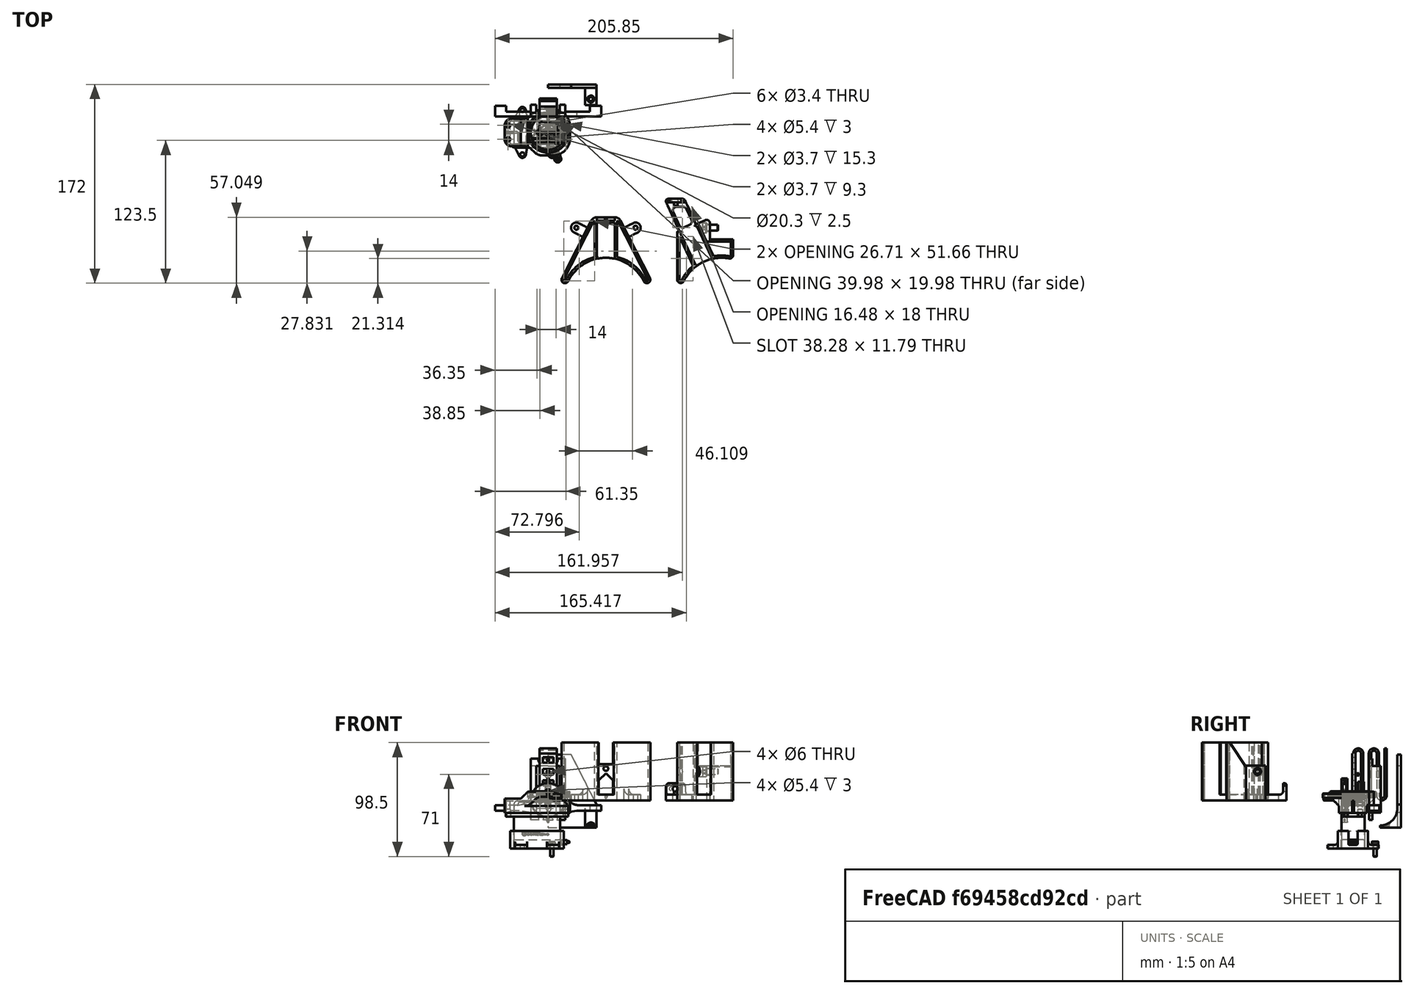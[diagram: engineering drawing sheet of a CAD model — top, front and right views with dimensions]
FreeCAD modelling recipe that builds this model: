
FCSTD DOCUMENT  (FreeCAD 1.0R39109 (Git))
Label: OuterCanMover
License: All rights reserved
LicenseURL: https://en.wikipedia.org/wiki/All_rights_reserved
objects: Sketcher::SketchObject×79, PartDesign::Pocket×47, PartDesign::Pad×34, PartDesign::Body×20, App::Part×11, App::Link×9, PartDesign::Mirrored×9, App::LinkElement×8, PartDesign::Fillet×7, PartDesign::PolarPattern×7, Part::Feature×6, PartDesign::Groove×5, PartDesign::LinearPattern×4, Part::FeaturePython×4, Mesh::Feature×3, PartDesign::Chamfer×3, PartDesign::Revolution×2, PartDesign::SubShapeBinder×1, PartDesign::MultiTransform×1
note: 525 computed .brp shape members not serialized (recipe doc carries the construction recipe); baked Part::Feature solids carry a one-line shape summary decoded from their .brp

FEATURE [Sketcher::SketchObject] Sketch
  ArcFitTolerance = 1e-06
  AttachmentSupport = -> [XY_Plane]
  FullyConstrained = true
  MakeInternals = false
  MapMode = 5
  sketch-geometry (18):
    g0: Circle [constr] CenterX=0 CenterY=-62.5 CenterZ=0 NormalX=0 NormalY=0 NormalZ=1 AngleXU=0 Radius=36.25
    g1: LineSegment [constr] StartX=-10 StartY=10 StartZ=0 EndX=-10 EndY=-10 EndZ=0
    g2: LineSegment [constr] StartX=-10 StartY=-10 StartZ=0 EndX=10 EndY=-10 EndZ=0
    g3: LineSegment [constr] StartX=10 StartY=-10 StartZ=0 EndX=10 EndY=10 EndZ=0
    g4: LineSegment [constr] StartX=10 StartY=10 StartZ=0 EndX=-10 EndY=10 EndZ=0
    g5: ArcOfCircle CenterX=0 CenterY=-62.5 CenterZ=0 NormalX=0 NormalY=0 NormalZ=1 AngleXU=0 Radius=36.5 StartAngle=1.39264 EndAngle=2.6779
    g6: LineSegment StartX=10 StartY=-10 StartZ=0 EndX=-10 EndY=-10 EndZ=0
    g7: LineSegment StartX=-10 StartY=-10 StartZ=0 EndX=-10 EndY=10 EndZ=0
    g8: LineSegment StartX=-14 StartY=14 StartZ=0 EndX=-23.3291 EndY=14 EndZ=0
    g9: LineSegment StartX=-38.3291 StartY=-1 StartZ=0 EndX=-38.3291 EndY=-44.8335 EndZ=0
    g10: ArcOfCircle CenterX=-14 CenterY=10 CenterZ=0 NormalX=0 NormalY=0 NormalZ=1 AngleXU=0 Radius=4 StartAngle=0 EndAngle=1.5708
    g11: GeomPoint [constr] X=-10 Y=14 Z=0
    g12: LineSegment StartX=10 StartY=-10 StartZ=0 EndX=10 EndY=-23.6252 EndZ=0
    g13: ArcOfCircle CenterX=-35.3291 CenterY=-44.8335 CenterZ=0 NormalX=0 NormalY=0 NormalZ=1 AngleXU=0 Radius=3 StartAngle=3.14159 EndAngle=5.81949
    g14: ArcOfCircle CenterX=7 CenterY=-23.6252 CenterZ=0 NormalX=0 NormalY=0 NormalZ=1 AngleXU=0 Radius=3 StartAngle=4.53423 EndAngle=6.28319
    g15: LineSegment [constr] StartX=-38.3291 StartY=14 StartZ=0 EndX=-16.3503 EndY=-29.8669 EndZ=0
    g16: ArcOfCircle CenterX=-23.3291 CenterY=-1 CenterZ=0 NormalX=0 NormalY=0 NormalZ=1 AngleXU=0 Radius=15 StartAngle=1.5708 EndAngle=3.14159
    g17: GeomPoint [constr] X=-38.3291 Y=14 Z=0
  constraints (44):
    c: Coincident(g1,g2)
    c: Coincident(g2,g3)
    c: Coincident(g3,g4)
    c: Vertical(g1)
    c: Vertical(g3)
    c: Horizontal(g2)
    c: Horizontal(g4)
    c: Symmetric(g1,g2,g-1)
    c: Equal(g4,g3)
    c: Coincident(g5,g0)
    c: DistanceY(g3,g3) = 20
    c: Diameter(g0) = 72.5
    c: Coincident(g7,g6)
    c: Vertical(g7)
    c: Horizontal(g8)
    c: Vertical(g9)
    c: Coincident(g1,g4)
    c: Distance(g11,g1) = 4
    c: PointOnObject(g11,g7)
    c: PointOnObject(g11,g8)
    c: Tangent(g7,g10) = -1.5708
    c: Tangent(g8,g10) = -1.5708
    c: Radius(g10) = 4
    c: PointOnObject(g0,g-2)
    c: DistanceY(g0,g-1) = 62.5
    c: Coincident(g12,g6)
    c: Vertical(g12)
    c: Coincident(g1,g6)
    c: Tangent(g9,g13) = -1.5708
    c: Tangent(g5,g13) = 1.5708
    c: Tangent(g5,g14) = 1.5708
    c: Tangent(g12,g14) = 1.5708
    c: Equal(g14,g13)
    c: Radius(g13) = 3
    c: Coincident(g15,g17)
    c: PointOnObject(g15,g5)
    c: Symmetric(g14,g13,g15)
    c: Coincident(g6,g2)
    c: PointOnObject(g17,g8)
    c: PointOnObject(g17,g9)
    c: Tangent(g8,g16) = -1.5708
    c: Tangent(g9,g16) = -1.5708
    c: Radius(g16) = 15
    c: Diameter(g5) = 73
FEATURE [PartDesign::Pad] Pad
  Direction = (0,0,1)
  Length = 50
  Length2 = 10
  Profile = -> Sketch
  ReferenceAxis = -> Sketch [N_Axis]
  Suppressed = false
  Type = 0
FEATURE [Sketcher::SketchObject] Sketch001
  ArcFitTolerance = 1e-06
  AttachmentOffset = pos=(0,0,5) rot=(0,0,1;0rad)
  AttachmentSupport = -> [XY_Plane]
  ExternalGeometry = -> [Pad]
  FullyConstrained = true
  MakeInternals = false
  MapMode = 5
  Placement = pos=(0,0,5) rot=(0,0,1;0rad)
  sketch-geometry (25):
    g0: LineSegment [constr] StartX=-44.1685 StartY=14 StartZ=0 EndX=-35.9616 EndY=-3.59975 EndZ=0
    g1: LineSegment StartX=-8.60751 StartY=-25.8214 StartZ=0 EndX=-21.3706 EndY=1.54911 EndZ=0
    g2: LineSegment StartX=-44.1685 StartY=14 StartZ=0 EndX=-27.1765 EndY=14 EndZ=0
    g3: ArcOfCircle CenterX=0 CenterY=-62.5 CenterZ=0 NormalX=0 NormalY=0 NormalZ=1 AngleXU=0 Radius=36.5 StartAngle=1.82252 EndAngle=2.19174
    g4: LineSegment [constr] StartX=0 StartY=-62.5 StartZ=0 EndX=-35.6725 EndY=14 EndZ=0
    g5: LineSegment StartX=-22.5646 StartY=-32.3297 StartZ=0 EndX=-21.6583 EndY=-31.9071 EndZ=0
    g6: LineSegment StartX=-8.60751 StartY=-25.8214 StartZ=0 EndX=-9.51381 EndY=-26.244 EndZ=0
    g7: LineSegment StartX=-21.6583 StartY=-31.9071 StartZ=0 EndX=-21.2357 EndY=-32.8134 EndZ=0
    g8: LineSegment StartX=-9.51381 StartY=-26.244 StartZ=0 EndX=-9.0912 EndY=-27.1503 EndZ=0
    g9: LineSegment [constr] StartX=-22.5646 StartY=-32.3297 StartZ=0 EndX=-8.60751 EndY=-25.8214 EndZ=0
    g10: LineSegment StartX=-35.9616 StartY=-3.59975 StartZ=0 EndX=-34.6022 EndY=-2.96583 EndZ=0
    g11: LineSegment StartX=-21.3706 StartY=1.54911 StartZ=0 EndX=-22.73 EndY=0.915178 EndZ=0
    g12: LineSegment StartX=-34.6022 StartY=-2.96583 StartZ=0 EndX=-33.9683 EndY=-4.32529 EndZ=0
    g13: LineSegment StartX=-23.364 StartY=2.27464 StartZ=0 EndX=-22.73 EndY=0.915178 EndZ=0
    g14: LineSegment StartX=-35.3277 StartY=-4.95922 StartZ=0 EndX=-22.5646 EndY=-32.3297 EndZ=0
    g15: LineSegment [constr] StartX=-22.0045 StartY=2.90857 StartZ=0 EndX=-27.1765 EndY=14 EndZ=0
    g16: LineSegment StartX=-23.364 StartY=2.27464 StartZ=0 EndX=-22.0045 EndY=2.90857 EndZ=0
    g17: LineSegment StartX=-33.9683 StartY=-4.32529 StartZ=0 EndX=-35.3277 EndY=-4.95922 EndZ=0
    g18: LineSegment [constr] StartX=-35.9616 StartY=-3.59975 StartZ=0 EndX=-35.3277 EndY=-4.95922 EndZ=0
    g19: LineSegment [constr] StartX=-22.0045 StartY=2.90857 StartZ=0 EndX=-21.3706 EndY=1.54911 EndZ=0
    g20: ArcOfCircle CenterX=-20.8978 CenterY=10 CenterZ=0 NormalX=0 NormalY=0 NormalZ=1 AngleXU=0 Radius=4 StartAngle=1.5708 EndAngle=3.57792
    g21: LineSegment StartX=-38.3291 StartY=-4.12459 StartZ=0 EndX=-44.1685 EndY=14 EndZ=0
    g22: LineSegment StartX=-24.523 StartY=8.30953 StartZ=0 EndX=-22.0045 EndY=2.90857 EndZ=0
    g23: LineSegment StartX=-27.1765 StartY=14 StartZ=0 EndX=-20.8978 EndY=14 EndZ=0
    g24: ArcOfCircle CenterX=-37.0872 CenterY=-4.12459 CenterZ=0 NormalX=0 NormalY=0 NormalZ=1 AngleXU=0 Radius=1.2419 StartAngle=0.436322 EndAngle=3.14159
  constraints (64):
    c: PointOnObject(g15,g-3)
    c: Coincident(g2,g15)
    c: Parallel(g1,g0)
    c: Coincident(g3,g-5)
    c: Angle(g-2,g1) = 0.436332
    c: Coincident(g4,g3)
    c: Parallel(g4,g1)
    c: Coincident(g2,g0)
    c: Horizontal(g2)
    c: Symmetric(g0,g15,g4)
    c: Coincident(g7,g5)
    c: Coincident(g8,g6)
    c: Coincident(g3,g8)
    c: Symmetric(g6,g5,g4)
    c: Coincident(g9,g5)
    c: Coincident(g9,g6)
    c: PointOnObject(g6,g9)
    c: PointOnObject(g5,g9)
    c: Perpendicular(g5,g7)
    c: Perpendicular(g6,g8)
    c: Coincident(g3,g7)
    c: PointOnObject(g3,g-5)
    c: Distance(g7,g7) = 1
    c: Distance(g5,g5) = 1
    c: Coincident(g14,g5)
    c: Coincident(g1,g6)
    c: Distance(g1,g14) = 15.4
    c: PointOnObject(g16,g15)
    c: Distance(g17,g10) = 1.5
    c: Symmetric(g12,g13,g4)
    c: Perpendicular(g0,g10) = 1.5708
    c: PointOnObject(g14,g11)
    c: Perpendicular(g1,g11) = 1.5708
    c: PointOnObject(g15,g16)
    c: Coincident(g11,g13)
    c: Coincident(g17,g12)
    c: Perpendicular(g10,g12) = 4.71239
    c: Perpendicular(g12,g17)
    c: Perpendicular(g15,g16)
    c: Parallel(g15,g1)
    c: Coincident(g18,g0)
    c: Coincident(g18,g17)
    c: Coincident(g19,g15)
    c: Coincident(g19,g1)
    c: Parallel(g19,g15)
    c: Coincident(g13,g16)
    c: Parallel(g18,g0)
    c: Coincident(g14,g17)
    c: Equal(g11,g17)
    c: Distance(g14,g5) = 30.2
    c: Parallel(g1,g14)
    c: Distance(g10,g10) = 1.5
    c: PointOnObject(g20,g15)
    c: PointOnObject(g20,g-3)
    c: Coincident(g21,g0)
    c: Coincident(g22,g16)
    c: Coincident(g23,g2)
    c: Tangent(g22,g20) = -1.5708
    c: Tangent(g23,g20) = 1.5708
    c: Radius(g20) = 4
    c: Tangent(g24,g-4) = -1.5708
    c: Coincident(g21,g24)
    c: Coincident(g24,g0)
    c: Tangent(g24,g18)
FEATURE [PartDesign::Pocket] Pocket
  BaseFeature = -> Pad
  Direction = (0,0,-1)
  Length = 5
  Length2 = 5
  Profile = -> Sketch001
  ReferenceAxis = -> Sketch001 [N_Axis]
  Reversed = true
  Suppressed = false
  Type = 1
FEATURE [Sketcher::SketchObject] Sketch002
  ArcFitTolerance = 1e-06
  AttachmentSupport = -> [YZ_Plane002]
  FullyConstrained = true
  MakeInternals = false
  MapMode = 5
  Placement = pos=(0,0,0) rot=(0.57735,0.57735,0.57735;2.0944rad)
  sketch-geometry (24):
    g0: LineSegment StartX=0 StartY=0 StartZ=0 EndX=0 EndY=40.625 EndZ=0
    g1: LineSegment StartX=0 StartY=0 StartZ=0 EndX=2 EndY=0 EndZ=0
    g2: LineSegment StartX=2 StartY=0 StartZ=0 EndX=2 EndY=40.625 EndZ=0
    g3: LineSegment StartX=6.75 StartY=40.625 StartZ=0 EndX=6.75 EndY=4.375 EndZ=0
    g4: LineSegment StartX=8.75 StartY=40.625 StartZ=0 EndX=8.75 EndY=4.375 EndZ=0
    g5: LineSegment StartX=13.5 StartY=40.625 StartZ=0 EndX=13.5 EndY=4.375 EndZ=0
    g6: LineSegment StartX=15.5 StartY=40.625 StartZ=0 EndX=15.5 EndY=4.375 EndZ=0
    g7: ArcOfCircle CenterX=4.375 CenterY=40.625 CenterZ=0 NormalX=0 NormalY=0 NormalZ=1 AngleXU=0 Radius=4.375 StartAngle=-9e-16 EndAngle=3.14159
    g8: ArcOfCircle CenterX=4.375 CenterY=40.625 CenterZ=0 NormalX=0 NormalY=0 NormalZ=1 AngleXU=0 Radius=2.375 StartAngle=4e-16 EndAngle=3.14159
    g9: ArcOfCircle CenterX=11.125 CenterY=4.375 CenterZ=0 NormalX=0 NormalY=0 NormalZ=1 AngleXU=0 Radius=4.375 StartAngle=3.14159 EndAngle=6.28319
    g10: ArcOfCircle CenterX=11.125 CenterY=4.375 CenterZ=0 NormalX=0 NormalY=0 NormalZ=1 AngleXU=0 Radius=2.375 StartAngle=3.14159 EndAngle=6.28319
    g11: ArcOfCircle CenterX=17.875 CenterY=40.625 CenterZ=0 NormalX=0 NormalY=0 NormalZ=1 AngleXU=0 Radius=4.375 StartAngle=3e-16 EndAngle=3.14159
    g12: ArcOfCircle CenterX=17.875 CenterY=40.625 CenterZ=0 NormalX=0 NormalY=0 NormalZ=1 AngleXU=0 Radius=2.375 StartAngle=8e-16 EndAngle=3.14159
    g13: LineSegment StartX=20.25 StartY=40.625 StartZ=0 EndX=20.25 EndY=4.375 EndZ=0
    g14: LineSegment StartX=22.25 StartY=40.625 StartZ=0 EndX=22.25 EndY=4.375 EndZ=0
    g15: LineSegment [constr] StartX=0 StartY=45 StartZ=0 EndX=29 EndY=45 EndZ=0
    g16: LineSegment [constr] StartX=0 StartY=0 StartZ=0 EndX=29 EndY=0 EndZ=0
    g17: LineSegment [constr] StartX=0 StartY=4.375 StartZ=0 EndX=29 EndY=4.375 EndZ=0
    g18: LineSegment [constr] StartX=0 StartY=40.625 StartZ=0 EndX=29 EndY=40.625 EndZ=0
    g19: ArcOfCircle CenterX=24.625 CenterY=4.375 CenterZ=0 NormalX=0 NormalY=0 NormalZ=1 AngleXU=0 Radius=4.375 StartAngle=3.14159 EndAngle=6.28319
    g20: ArcOfCircle CenterX=24.625 CenterY=4.375 CenterZ=0 NormalX=0 NormalY=0 NormalZ=1 AngleXU=0 Radius=2.375 StartAngle=3.14159 EndAngle=6.28319
    g21: LineSegment StartX=27 StartY=4.375 StartZ=0 EndX=27 EndY=45 EndZ=0
    g22: LineSegment StartX=29 StartY=4.375 StartZ=0 EndX=29 EndY=45 EndZ=0
    g23: LineSegment StartX=27 StartY=45 StartZ=0 EndX=29 EndY=45 EndZ=0
  constraints (60):
    c: PointOnObject(g0,g-2)
    c: Coincident(g1,g0)
    c: Horizontal(g1)
    c: Coincident(g2,g1)
    c: Vertical(g2)
    c: Vertical(g3)
    c: Vertical(g4)
    c: Vertical(g5)
    c: Vertical(g6)
    c: Tangent(g8,g2) = 1.5708
    c: Tangent(g8,g3) = 1.5708
    c: Tangent(g9,g3) = -1.5708
    c: Tangent(g7,g4) = 1.5708
    c: Tangent(g7,g0) = 1.5708
    c: Tangent(g10,g4) = -1.5708
    c: Tangent(g10,g5) = 1.5708
    c: Tangent(g9,g6) = 1.5708
    c: Tangent(g12,g6) = -1.5708
    c: Tangent(g11,g5) = -1.5708
    c: Vertical(g13)
    c: Vertical(g14)
    c: Tangent(g14,g11) = 1.5708
    c: Tangent(g13,g12) = 1.5708
    c: Horizontal(g15)
    c: Coincident(g16,g0)
    c: Horizontal(g16)
    c: Horizontal(g17)
    c: Coincident(g18,g0)
    c: Horizontal(g18)
    c: Coincident(g11,g12)
    c: PointOnObject(g11,g18)
    c: PointOnObject(g9,g17)
    c: Coincident(g9,g10)
    c: Coincident(g7,g8)
    c: Tangent(g15,g7)
    c: Tangent(g15,g11)
    c: Tangent(g9,g16)
    c: PointOnObject(g19,g17)
    c: Coincident(g20,g19)
    c: Vertical(g21)
    c: Coincident(g23,g21)
    c: Coincident(g23,g22)
    c: Horizontal(g23)
    c: PointOnObject(g21,g15)
    c: Tangent(g21,g20) = -1.5708
    c: Tangent(g22,g19) = -1.5708
    c: Tangent(g19,g16)
    c: Tangent(g20,g14) = -1.5708
    c: Coincident(g19,g17)
    c: Vertical(g17,g18)
    c: Vertical(g18,g15)
    c: Vertical(g15,g16)
    c: Tangent(g19,g13) = -1.5708
    c: Equal(g10,g8)
    c: DistanceY(g0,g15) = 45
    c: Coincident(g0,g-1)
    c: PointOnObject(g15,g-2)
    c: Distance(g1,g1) = 2
    c: DistanceX(g15,g15) = 29
    c: Vertical(g17,g0)
FEATURE [PartDesign::Pad] Pad001
  Direction = (1,0,0)
  Length = 15
  Length2 = 10
  Midplane = true
  Placement = pos=(0,0,0) rot=(1,1,1;2.0944rad)
  Profile = -> Sketch002
  ReferenceAxis = -> Sketch002 [N_Axis]
  Suppressed = false
  Type = 0
FEATURE [Sketcher::SketchObject] Sketch003
  ArcFitTolerance = 1e-06
  AttachmentOffset = pos=(0,0,-3) rot=(0,0,1;0rad)
  AttachmentSupport = -> [XZ_Plane002]
  ExternalGeometry = -> [Pad001]
  FullyConstrained = true
  MakeInternals = false
  MapMode = 5
  Placement = pos=(0,3,-7e-16) rot=(1,0,0;1.5708rad)
  sketch-geometry (2):
    g0: Circle CenterX=0 CenterY=22.5 CenterZ=0 NormalX=0 NormalY=0 NormalZ=1 AngleXU=0 Radius=3
    g1: GeomPoint X=0 Y=45 Z=0
  constraints (4):
    c: PointOnObject(g0,g-2)
    c: PointOnObject(g1,g-3)
    c: Symmetric(g1,g-1,g0)
    c: Diameter(g0) = 6
FEATURE [PartDesign::Pocket] Pocket001
  BaseFeature = -> Pad001
  Direction = (0,1,-2e-16)
  Length = 5
  Length2 = 5
  Placement = pos=(0,0,0) rot=(1,1,1;2.0944rad)
  Profile = -> Sketch003
  ReferenceAxis = -> Sketch003 [N_Axis]
  Suppressed = false
  Type = 1
FEATURE [Sketcher::SketchObject] Sketch004
  ArcFitTolerance = 1e-06
  AttachmentSupport = -> [XY_Plane003]
  FullyConstrained = true
  MakeInternals = false
  MapMode = 5
  sketch-geometry (4):
    g0: LineSegment StartX=4.5 StartY=-2.25 StartZ=0 EndX=4.5 EndY=2.25 EndZ=0
    g1: LineSegment StartX=4.5 StartY=2.25 StartZ=0 EndX=-4.5 EndY=2.25 EndZ=0
    g2: LineSegment StartX=-4.5 StartY=2.25 StartZ=0 EndX=-4.5 EndY=-2.25 EndZ=0
    g3: LineSegment StartX=-4.5 StartY=-2.25 StartZ=0 EndX=4.5 EndY=-2.25 EndZ=0
  constraints (11):
    c: Coincident(g0,g1)
    c: Coincident(g1,g2)
    c: Coincident(g2,g3)
    c: Coincident(g3,g0)
    c: Vertical(g0)
    c: Vertical(g2)
    c: Horizontal(g1)
    c: Horizontal(g3)
    c: Symmetric(g1,g0,g-1)
    c: DistanceX(g1,g1) = 9
    c: Distance(g2,g2) = 4.5
FEATURE [PartDesign::Pad] Pad002
  Direction = (0,0,1)
  Length = 2.5
  Length2 = 10
  Profile = -> Sketch004
  ReferenceAxis = -> Sketch004 [N_Axis]
  Suppressed = false
  Type = 0
FEATURE [PartDesign::Body] Body002  label="aimant"
  AllowCompound = false
  Group = -> [Sketch004,Pad002]
  Origin = -> Origin003
  Tip = -> Pad002
FEATURE [App::LinkElement] Link_i0
  LinkedObject = -> Body002
  _LinkOwner = 3722
FEATURE [App::LinkElement] Link_i1
  LinkPlacement = pos=(0,10,0) rot=(0,0,1;0rad)
  LinkedObject = -> Body002
  Placement = pos=(0,10,0) rot=(0,0,1;0rad)
  _LinkOwner = 3722
FEATURE [App::LinkElement] Link_i2
  LinkPlacement = pos=(0,20,0) rot=(0,0,1;0rad)
  LinkedObject = -> Body002
  Placement = pos=(0,20,0) rot=(0,0,1;0rad)
  _LinkOwner = 3722
FEATURE [App::LinkElement] Link_i3
  LinkPlacement = pos=(0,30,0) rot=(0,0,1;0rad)
  LinkedObject = -> Body002
  Placement = pos=(0,30,0) rot=(0,0,1;0rad)
  _LinkOwner = 3722
FEATURE [App::Link] Link  label="aimant001"
  ElementCount = 4
  ElementList = -> [Link_i0,Link_i1,Link_i2,Link_i3]
  LinkPlacement = pos=(-2.28509e-05,1,5.00001) rot=(1,0,0;1.5708rad)
  LinkedObject = -> Body002
  Placement = pos=(-2.28509e-05,1,5.00001) rot=(1,0,0;1.5708rad)
FEATURE [PartDesign::Pad] Pad003
  BaseFeature = -> Pocket001
  Direction = (-4e-16,-1,2e-16)
  Length = 1
  Length2 = 10
  Placement = pos=(0,0,0) rot=(1,1,1;2.0944rad)
  Profile = -> Pocket001 [Face9]
  Suppressed = false
  Type = 0
FEATURE [Sketcher::SketchObject] Sketch005
  ArcFitTolerance = 1e-06
  AttachmentOffset = pos=(0,0,1.5) rot=(0,0,1;0rad)
  AttachmentSupport = -> [XZ_Plane002]
  FullyConstrained = true
  MakeInternals = false
  MapMode = 5
  Placement = pos=(0,-1.5,3e-16) rot=(1,0,0;1.5708rad)
  sketch-geometry (6):
    g0: LineSegment StartX=-4.6 StartY=2.65 StartZ=0 EndX=4.6 EndY=2.65 EndZ=0
    g1: LineSegment StartX=4.6 StartY=2.65 StartZ=0 EndX=4.6 EndY=7.35 EndZ=0
    g2: LineSegment StartX=4.6 StartY=7.35 StartZ=0 EndX=-4.6 EndY=7.35 EndZ=0
    g3: LineSegment StartX=-4.6 StartY=7.35 StartZ=0 EndX=-4.6 EndY=2.65 EndZ=0
    g4: GeomPoint X=0 Y=5 Z=0
    g5: Circle CenterX=0 CenterY=5 CenterZ=0 NormalX=0 NormalY=0 NormalZ=1 AngleXU=0 Radius=1
  constraints (15):
    c: Coincident(g0,g1)
    c: Coincident(g1,g2)
    c: Coincident(g2,g3)
    c: Coincident(g3,g0)
    c: Horizontal(g2)
    c: Vertical(g1)
    c: Vertical(g3)
    c: Distance(g1,g3) = 9.2
    c: Distance(g0,g2) = 4.7
    c: PointOnObject(g4,g-2)
    c: Symmetric(g1,g0,g4)
    c: Horizontal(g0)
    c: DistanceY(g-1,g4) = 5
    c: Diameter(g5) = 2
    c: Coincident(g5,g4)
FEATURE [PartDesign::Pocket] Pocket002
  BaseFeature = -> Pad003
  Direction = (0,1,-2e-16)
  Length = 3
  Length2 = 5
  Placement = pos=(0,0,0) rot=(1,1,1;2.0944rad)
  Profile = -> Sketch005
  ReferenceAxis = -> Sketch005 [N_Axis]
  Suppressed = false
  Type = 0
FEATURE [PartDesign::LinearPattern] LinearPattern
  BaseFeature = -> Pocket002
  Direction = -> Sketch005 [V_Axis]
  Length = 30
  Mode = 0
  Occurrences = 4
  Offset = 10
  Originals = -> [Pocket002]
  Placement = pos=(0,0,0) rot=(1,1,1;2.0944rad)
  Suppressed = false
  TransformMode = 0
FEATURE [PartDesign::Pocket] Pocket003
  BaseFeature = -> LinearPattern
  Direction = (0,1,-2e-16)
  Length = 8
  Length2 = 5
  Placement = pos=(0,0,0) rot=(1,1,1;2.0944rad)
  Profile = -> Sketch005 [Edge5]
  ReferenceAxis = -> Sketch005 [N_Axis]
  Suppressed = false
  Type = 0
FEATURE [PartDesign::LinearPattern] LinearPattern001
  BaseFeature = -> Pocket003
  Direction = -> Sketch005 [V_Axis]
  Length = 30
  Mode = 0
  Occurrences = 4
  Offset = 10
  Originals = -> [Pocket003]
  Placement = pos=(0,0,0) rot=(1,1,1;2.0944rad)
  Suppressed = false
  TransformMode = 0
FEATURE [Sketcher::SketchObject] Sketch006
  ArcFitTolerance = 1e-06
  AttachmentOffset = pos=(0,0,-2) rot=(0,0,1;0rad)
  AttachmentSupport = -> [XZ_Plane002]
  FullyConstrained = true
  MakeInternals = false
  MapMode = 5
  Placement = pos=(0,2,-4e-16) rot=(1,0,0;1.5708rad)
  sketch-geometry (1):
    g0: Circle CenterX=-1.5 CenterY=22.5 CenterZ=0 NormalX=0 NormalY=0 NormalZ=1 AngleXU=0 Radius=0.75
  constraints (3):
    c: Diameter(g0) = 1.5
    c: Distance(g0,g-2) = 1.5
    c: DistanceY(g-1,g0) = 22.5
FEATURE [Sketcher::SketchObject] Sketch007
  ArcFitTolerance = 1e-06
  AttachmentSupport = -> [Pocket]
  FullyConstrained = true
  MakeInternals = false
  MapMode = 5
  Placement = pos=(-10,0,0) rot=(0.57735,0.57735,0.57735;2.0944rad)
  sketch-geometry (1):
    g0: Circle CenterX=0 CenterY=25 CenterZ=0 NormalX=0 NormalY=0 NormalZ=1 AngleXU=0 Radius=3
  constraints (3):
    c: PointOnObject(g0,g-2)
    c: Diameter(g0) = 6
    c: DistanceY(g-1,g0) = 25
FEATURE [PartDesign::Pocket] Pocket004  label="vis1"
  BaseFeature = -> Pocket
  Direction = (-1,0,0)
  Length = 12
  Length2 = 5
  Profile = -> Sketch007
  ReferenceAxis = -> Sketch007 [N_Axis]
  Suppressed = false
  Type = 0
FEATURE [Sketcher::SketchObject] Sketch008
  ArcFitTolerance = 1e-06
  AttachmentOffset = pos=(0,0,-3) rot=(0,0,1;0rad)
  AttachmentSupport = -> [Pocket004]
  FullyConstrained = true
  MakeInternals = false
  MapMode = 5
  Placement = pos=(-13,0,0) rot=(0.57735,0.57735,0.57735;2.0944rad)
  sketch-geometry (1):
    g0: Circle CenterX=0 CenterY=25 CenterZ=0 NormalX=0 NormalY=0 NormalZ=1 AngleXU=0 Radius=4.25
  constraints (3):
    c: Diameter(g0) = 8.5
    c: PointOnObject(g0,g-2)
    c: DistanceY(g-1,g0) = 25
FEATURE [PartDesign::Pocket] Pocket005  label="vis2"
  BaseFeature = -> Pocket004
  Direction = (-1,0,0)
  Length = 5
  Length2 = 5
  Profile = -> Sketch008
  ReferenceAxis = -> Sketch008 [N_Axis]
  Suppressed = false
  Type = 1
FEATURE [Sketcher::SketchObject] Sketch009
  ArcFitTolerance = 1e-06
  AttachmentSupport = -> [Pocket005]
  ExternalGeometry = -> [Pocket005]
  FullyConstrained = true
  MakeInternals = false
  MapMode = 5
  Placement = pos=(0,0,50) rot=(0,0,1;0rad)
  sketch-geometry (14):
    g0: LineSegment StartX=-36.3291 StartY=-7.54414 StartZ=0 EndX=-36.3291 EndY=-44.8335 EndZ=0
    g1: LineSegment StartX=-36.3291 StartY=-7.54414 StartZ=0 EndX=-24.5371 EndY=-32.8322 EndZ=0
    g2: ArcOfCircle CenterX=0 CenterY=-62.5 CenterZ=0 NormalX=0 NormalY=0 NormalZ=1 AngleXU=0 Radius=38.5 StartAngle=2.26182 EndAngle=2.6779
    g3: ArcOfCircle CenterX=-35.3291 CenterY=-44.8335 CenterZ=0 NormalX=0 NormalY=0 NormalZ=1 AngleXU=0 Radius=1 StartAngle=3.14159 EndAngle=5.81949
    g4: LineSegment StartX=-36.8069 StartY=-1.78714 StartZ=0 EndX=-22.8497 EndY=4.72118 EndZ=0
    g5: LineSegment StartX=-22.8497 StartY=4.72118 StartZ=0 EndX=-22.0045 EndY=2.90857 EndZ=0
    g6: LineSegment StartX=-22.0045 StartY=2.90857 StartZ=0 EndX=-35.9616 EndY=-3.59975 EndZ=0
    g7: LineSegment StartX=-35.9616 StartY=-3.59975 StartZ=0 EndX=-36.8069 EndY=-1.78714 EndZ=0
    g8: LineSegment [constr] StartX=-35.9616 StartY=-3.59975 StartZ=0 EndX=-37.7743 EndY=-4.44499 EndZ=0
    g9: ArcOfCircle CenterX=0 CenterY=-62.5 CenterZ=0 NormalX=0 NormalY=0 NormalZ=1 AngleXU=0 Radius=38.5 StartAngle=1.39264 EndAngle=1.75244
    g10: LineSegment StartX=-12.8458 StartY=-12 StartZ=0 EndX=-6.95473 EndY=-24.6334 EndZ=0
    g11: LineSegment StartX=8 StartY=-23.6252 StartZ=0 EndX=8 EndY=-12 EndZ=0
    g12: LineSegment StartX=8 StartY=-12 StartZ=0 EndX=-12.8458 EndY=-12 EndZ=0
    g13: ArcOfCircle CenterX=7 CenterY=-23.6252 CenterZ=0 NormalX=0 NormalY=0 NormalZ=1 AngleXU=0 Radius=1 StartAngle=4.53423 EndAngle=6.28319
  constraints (36):
    c: Vertical(g0)
    c: Coincident(g2,g1)
    c: Tangent(g3,g2) = 1.5708
    c: Tangent(g3,g0) = -1.5708
    c: Coincident(g5,g4)
    c: Coincident(g6,g5)
    c: Coincident(g7,g6)
    c: Coincident(g7,g4)
    c: Perpendicular(g4,g7)
    c: Perpendicular(g7,g6)
    c: Perpendicular(g5,g6)
    c: Coincident(g6,g-4)
    c: Coincident(g5,g-3)
    c: Coincident(g-6,g3)
    c: Perpendicular(g6,g1)
    c: Coincident(g1,g0)
    c: Distance(g0,g-6) = 2
    c: Coincident(g8,g6)
    c: Parallel(g8,g6)
    c: PointOnObject(g8,g1)
    c: Distance(g8,g8) = 2
    c: Coincident(g2,g-5)
    c: Coincident(g9,g2)
    c: Coincident(g11,g12)
    c: Coincident(g12,g10)
    c: Vertical(g11)
    c: Horizontal(g12)
    c: Coincident(g9,g10)
    c: Tangent(g9,g13) = 1.5708
    c: Tangent(g11,g13) = -1.5708
    c: Parallel(g10,g1)
    c: Coincident(g13,g-9)
    c: Distance(g11,g-9) = 2
    c: DistanceY(g11,g-8) = 2
    c: Distance(g10,g-10) = 2
    c: Distance(g5,g5) = 2
FEATURE [PartDesign::Pocket] Pocket006
  BaseFeature = -> Pocket005
  Direction = (0,0,-1)
  Length = 5
  Length2 = 5
  Profile = -> Sketch009
  ReferenceAxis = -> Sketch009 [N_Axis]
  Suppressed = false
  Type = 1
FEATURE [Part::FeaturePython] Screw  label="M5x10-Vis"  # WARN: FeaturePython — macro-defined, semantics opaque (R4)
  BaseObject = -> Body [Fillet.Edge111]
  Diameter = 3
  Invert = true
  LeftHanded = false
  Length = 1
  LengthCustom = 10
  MatchOuter = false
  OffsetAngle = 0
  Placement = pos=(137,-82.5,25) rot=(0,-1,0;1.5708rad)
  Thread = false
  Type = 37
FEATURE [PartDesign::Pocket] Pocket007
  BaseFeature = -> Pocket006
  Direction = (0,0,-1)
  Length = 5
  Length2 = 5
  Profile = -> Pocket006 [Face48]
  Suppressed = false
  Type = 0
FEATURE [Sketcher::SketchObject] Sketch010
  ArcFitTolerance = 1e-06
  AttachmentOffset = pos=(0,0,22.5) rot=(0,0,1;0rad)
  AttachmentSupport = -> [XY_Plane002]
  ExternalGeometry = -> [LinearPattern001]
  FullyConstrained = true
  MakeInternals = false
  MapMode = 5
  Placement = pos=(0,0,22.5) rot=(0,0,1;0rad)
  sketch-geometry (8):
    g0: LineSegment StartX=-3.5 StartY=2 StartZ=0 EndX=-0.5 EndY=5 EndZ=0
    g1: LineSegment StartX=-0.5 StartY=5 StartZ=0 EndX=0.5 EndY=5 EndZ=0
    g2: LineSegment StartX=0.5 StartY=5 StartZ=0 EndX=3.5 EndY=2 EndZ=0
    g3: LineSegment StartX=2 StartY=2 StartZ=0 EndX=0.5 EndY=3.5 EndZ=0
    g4: LineSegment StartX=0.5 StartY=3.5 StartZ=0 EndX=-0.5 EndY=3.5 EndZ=0
    g5: LineSegment StartX=-0.5 StartY=3.5 StartZ=0 EndX=-2 EndY=2 EndZ=0
    g6: LineSegment StartX=-3.5 StartY=2 StartZ=0 EndX=-2 EndY=2 EndZ=0
    g7: LineSegment StartX=2 StartY=2 StartZ=0 EndX=3.5 EndY=2 EndZ=0
  constraints (22):
    c: PointOnObject(g0,g-3)
    c: Coincident(g1,g0)
    c: Coincident(g2,g1)
    c: PointOnObject(g2,g-3)
    c: PointOnObject(g3,g-3)
    c: Coincident(g4,g3)
    c: Coincident(g5,g4)
    c: Coincident(g6,g0)
    c: PointOnObject(g6,g5)
    c: Horizontal(g6)
    c: Coincident(g7,g3)
    c: Coincident(g7,g2)
    c: Symmetric(g4,g3,g-2)
    c: Symmetric(g0,g1,g-2)
    c: Symmetric(g5,g3,g-2)
    c: Parallel(g0,g5)
    c: Parallel(g3,g2)
    c: Vertical(g0,g4)
    c: Distance(g0,g4) = 1.5
    c: Distance(g6,g6) = 1.5
    c: Distance(g4,g-3) = 1.5
    c: Distance(g4,g4) = 1
FEATURE [PartDesign::Pad] Pad004
  BaseFeature = -> LinearPattern001
  Direction = (0,0,1)
  Length = 2
  Length2 = 10
  Midplane = true
  Placement = pos=(0,0,0) rot=(1,1,1;2.0944rad)
  Profile = -> Sketch010
  ReferenceAxis = -> Sketch010 [N_Axis]
  Suppressed = false
  Type = 0
FEATURE [PartDesign::Body] Body001  label="ressort_d"
  AllowCompound = false
  Group = -> [Sketch002,Pad001,Sketch003,Pocket001,Pad003,Sketch005,Pocket002,LinearPattern,Pocket003,LinearPattern001,Sketch006,Sketch010,Pad004]
  Origin = -> Origin002
  Placement = pos=(0,0.2,0) rot=(0,0,1;0rad)
  Tip = -> Pad004
FEATURE [App::Part] Part001  label="ressort"
  Group = -> [Body001,Link]
  Origin = -> Origin004
  Placement = pos=(134,-110.7,50) rot=(-0.21644,0.976296,0;3.14159rad)
FEATURE [Mesh::Feature] open_tin_can
  Placement = pos=(150,-145,-3.18e-14) rot=(-1,0,0;1.5708rad)
FEATURE [Sketcher::SketchObject] Sketch011
  ArcFitTolerance = 1e-06
  AttachmentSupport = -> [Pocket007]
  ExternalGeometry = -> [Pocket007,Sketch009]
  FullyConstrained = true
  MakeInternals = false
  MapMode = 5
  Placement = pos=(0,0,50) rot=(0,0,1;0rad)
  sketch-geometry (10):
    g0: ArcOfCircle CenterX=-20.8978 CenterY=10 CenterZ=0 NormalX=0 NormalY=0 NormalZ=1 AngleXU=0 Radius=4 StartAngle=1.5708 EndAngle=3.57792
    g1: ArcOfCircle CenterX=-14 CenterY=10 CenterZ=0 NormalX=0 NormalY=0 NormalZ=1 AngleXU=0 Radius=4 StartAngle=0 EndAngle=1.5708
    g2: LineSegment StartX=-24.523 StartY=8.30953 StartZ=0 EndX=-22.0045 EndY=2.90857 EndZ=0
    g3: LineSegment StartX=-10 StartY=-10 StartZ=0 EndX=-10 EndY=10 EndZ=0
    g4: LineSegment StartX=-14 StartY=14 StartZ=0 EndX=-20.8978 EndY=14 EndZ=0
    g5: LineSegment StartX=-22.0045 StartY=2.90857 StartZ=0 EndX=-20.1919 EndY=3.7538 EndZ=0
    g6: LineSegment StartX=-20.1919 StartY=3.7538 StartZ=0 EndX=-12.8458 EndY=-12 EndZ=0
    g7: LineSegment StartX=8 StartY=-10 StartZ=0 EndX=-10 EndY=-10 EndZ=0
    g8: LineSegment StartX=-12.8458 StartY=-12 StartZ=0 EndX=8 EndY=-12 EndZ=0
    g9: LineSegment StartX=8 StartY=-12 StartZ=0 EndX=8 EndY=-10 EndZ=0
  constraints (22):
    c: Coincident(g0,g-6)
    c: Coincident(g1,g-5)
    c: Tangent(g4,g0) = -1.5708
    c: Tangent(g4,g1) = -1.5708
    c: Tangent(g3,g1) = -1.5708
    c: Tangent(g2,g0) = -1.5708
    c: Coincident(g0,g-6)
    c: Coincident(g5,g2)
    c: Coincident(g6,g5)
    c: Perpendicular(g2,g5)
    c: Perpendicular(g5,g6)
    c: Coincident(g2,g-9)
    c: Coincident(g6,g-7)
    c: Coincident(g8,g9)
    c: Coincident(g9,g7)
    c: Horizontal(g7)
    c: Horizontal(g8)
    c: Vertical(g9)
    c: Coincident(g8,g6)
    c: Coincident(g7,g3)
    c: Coincident(g3,g-4)
    c: DistanceX(g7,g7) = 18
FEATURE [PartDesign::Pocket] Pocket008
  BaseFeature = -> Pocket007
  Direction = (0,0,-1)
  Length = 20
  Length2 = 5
  Profile = -> Sketch011
  ReferenceAxis = -> Sketch011 [N_Axis]
  Suppressed = false
  Type = 0
FEATURE [Sketcher::SketchObject] Sketch012
  ArcFitTolerance = 1e-06
  AttachmentSupport = -> [Pocket008]
  ExternalGeometry = -> [Pocket008,Sketch009]
  FullyConstrained = true
  MakeInternals = false
  MapMode = 5
  Placement = pos=(0,0,30) rot=(0,0,1;0rad)
  sketch-geometry (4):
    g0: LineSegment StartX=-27.1765 StartY=14 StartZ=0 EndX=-22.0045 EndY=2.90857 EndZ=0
    g1: LineSegment StartX=-22.0045 StartY=2.90857 StartZ=0 EndX=-10 EndY=8.50636 EndZ=0
    g2: LineSegment StartX=-10 StartY=8.50636 StartZ=0 EndX=-10 EndY=14 EndZ=0
    g3: LineSegment StartX=-10 StartY=14 StartZ=0 EndX=-27.1765 EndY=14 EndZ=0
  constraints (11):
    c: Coincident(g0,g1)
    c: Coincident(g1,g2)
    c: Coincident(g2,g3)
    c: Coincident(g3,g0)
    c: Vertical(g2)
    c: Horizontal(g3)
    c: Coincident(g0,g-4)
    c: Perpendicular(g0,g1)
    c: PointOnObject(g-3,g0)
    c: PointOnObject(g-5,g3)
    c: PointOnObject(g-6,g2)
FEATURE [PartDesign::Pocket] Pocket009
  BaseFeature = -> Pocket008
  Direction = (0,0,-1)
  Length = 5
  Length2 = 5
  Profile = -> Sketch012
  ReferenceAxis = -> Sketch012 [N_Axis]
  Suppressed = false
  Type = 1
FEATURE [PartDesign::Fillet] Fillet
  Base = -> Pocket009 [Edge83]
  BaseFeature = -> Pocket009
  Radius = 3
  SupportTransform = false
  Suppressed = false
  UseAllEdges = false
FEATURE [PartDesign::Chamfer] Chamfer
  Angle = 45
  Base = -> Fillet [Edge42]
  BaseFeature = -> Fillet
  ChamferType = 1
  FlipDirection = false
  Size = 21
  Size2 = 14
  SupportTransform = false
  Suppressed = false
  UseAllEdges = false
FEATURE [Part::Feature] Part__Feature  label="Lever 25T"
  Placement = pos=(0,0,0) rot=(-1,0,0;1.5708rad)
  shape: bbox 18.84 x 33.03 x 6.019 mm, 125 faces (baked)
FEATURE [Part::Feature] Part__Feature001  label="Axis Servo"
  Placement = pos=(0,0,0) rot=(-1,0,0;1.5708rad)
  shape: bbox 5 x 5 x 8 mm, 5 faces (baked)
FEATURE [Part::Feature] Part__Feature002  label="Servo DS3218MG"
  Placement = pos=(0,0,0) rot=(-1,0,0;1.5708rad)
  shape: bbox 55 x 20 x 41 mm, 772 faces (baked)
FEATURE [Part::FeaturePython] Screw002  label="M2x5-Vis"  # WARN: FeaturePython — macro-defined, semantics opaque (R4)
  BaseObject = -> Body003 [Edge6]
  Diameter = 2
  Invert = true
  LeftHanded = false
  Length = 10
  LengthCustom = 5
  MatchOuter = false
  OffsetAngle = 0
  Placement = pos=(0,1e-15,4.8) rot=(0,0,1;0rad)
  Thread = false
  Type = 76
FEATURE [Sketcher::SketchObject] Sketch013
  ArcFitTolerance = 0
  AttachmentSupport = -> [XZ_Plane006]
  FullyConstrained = true
  MakeInternals = false
  MapMode = 5
  Placement = pos=(0,0,0) rot=(1,0,0;1.5708rad)
  expr: Constraints[19] = 19.8 / 2
  sketch-geometry (8):
    g0: LineSegment StartX=2.5 StartY=3.4 StartZ=0 EndX=2.5 EndY=0 EndZ=0
    g1: LineSegment StartX=2.5 StartY=0 StartZ=0 EndX=4.2 EndY=0 EndZ=0
    g2: LineSegment StartX=4.2 StartY=0 StartZ=0 EndX=4.2 EndY=2 EndZ=0
    g3: LineSegment StartX=4.2 StartY=2 StartZ=0 EndX=9.9 EndY=2 EndZ=0
    g4: LineSegment StartX=9.9 StartY=2 StartZ=0 EndX=9.9 EndY=4.4 EndZ=0
    g5: LineSegment StartX=9.9 StartY=4.4 StartZ=0 EndX=1.5 EndY=4.4 EndZ=0
    g6: LineSegment StartX=1.5 StartY=4.4 StartZ=0 EndX=1.5 EndY=3.4 EndZ=0
    g7: LineSegment StartX=1.5 StartY=3.4 StartZ=0 EndX=2.5 EndY=3.4 EndZ=0
  constraints (24):
    c: PointOnObject(g0,g-1)
    c: Vertical(g0)
    c: Coincident(g1,g0)
    c: PointOnObject(g1,g-1)
    c: Coincident(g2,g1)
    c: Vertical(g2)
    c: Coincident(g3,g2)
    c: Horizontal(g3)
    c: Coincident(g4,g3)
    c: Vertical(g4)
    c: Coincident(g5,g4)
    c: Horizontal(g5)
    c: Coincident(g6,g5)
    c: Coincident(g7,g6)
    c: Coincident(g7,g0)
    c: Horizontal(g7)
    c: Vertical(g6)
    c: DistanceY(g4,g4) = 2.4
    c: DistanceY(g2,g2) = 2
    c: DistanceX(g-1,g4) = 9.9
    c: DistanceX(g-1,g6) = 1.5
    c: DistanceY(g0,g0) = 3.4
    c: DistanceX(g-1,g0) = 2.5
    c: DistanceX(g1,g1) = 1.7
FEATURE [PartDesign::Revolution] Revolution
  Angle = 360
  Angle2 = 60
  Axis = (0,2e-16,1)
  Base = (0,0,0)
  Placement = pos=(0,0,0) rot=(1,0,0;1.5708rad)
  Profile = -> Sketch013
  ReferenceAxis = -> Sketch013 [V_Axis]
  Reversed = true
  Suppressed = false
  Type = 0
FEATURE [Sketcher::SketchObject] Sketch014
  ArcFitTolerance = 0
  AttachmentSupport = -> [XY_Plane006]
  FullyConstrained = true
  MakeInternals = false
  MapMode = 5
  sketch-geometry (1):
    g0: Circle CenterX=-7 CenterY=0 CenterZ=0 NormalX=0 NormalY=0 NormalZ=1 AngleXU=0 Radius=1.2
  constraints (3):
    c: PointOnObject(g0,g-1)
    c: Diameter(g0) = 2.4
    c: DistanceX(g0,g-1) = 7
FEATURE [PartDesign::Pocket] Pocket010
  BaseFeature = -> Revolution
  Direction = (0,0,-1)
  Length = 5
  Length2 = 5
  Midplane = true
  Placement = pos=(0,0,0) rot=(1,0,0;1.5708rad)
  Profile = -> Sketch014
  ReferenceAxis = -> Sketch014 [N_Axis]
  Suppressed = false
  Type = 1
FEATURE [PartDesign::PolarPattern] PolarPattern
  Angle = 360
  Axis = -> Sketch014 [N_Axis]
  BaseFeature = -> Pocket010
  Mode = 0
  Occurrences = 4
  Offset = 120
  Originals = -> [Pocket010]
  Placement = pos=(0,0,0) rot=(1,0,0;1.5708rad)
  Suppressed = false
  TransformMode = 0
FEATURE [PartDesign::Body] Body003  label="Corps"
  AllowCompound = false
  Group = -> [Sketch013,Revolution,Sketch014,Pocket010,PolarPattern]
  Origin = -> Origin006
  Placement = pos=(0,0,0.4) rot=(0,0,1;0rad)
  Tip = -> PolarPattern
FEATURE [App::Part] Part002  label="servo_DS3218MG"
  Group = -> [Part__Feature,Part__Feature001,Part__Feature002,Body003,Screw002]
  Origin = -> Origin005
  Placement = pos=(0,0,0) rot=(-0.57735,-0.57735,0.57735;4.18879rad)
FEATURE [Sketcher::SketchObject] Sketch015
  ArcFitTolerance = 1e-06
  AttachmentSupport = -> [XZ_Plane008]
  FullyConstrained = true
  MakeInternals = false
  MapMode = 5
  Placement = pos=(0,0,0) rot=(1,0,0;1.5708rad)
  expr: Constraints[2] = 5.5
  expr: Constraints[5] = 3.4
  sketch-geometry (6):
    g0: Circle CenterX=0 CenterY=0 CenterZ=0 NormalX=0 NormalY=0 NormalZ=1 AngleXU=0 Radius=15
    g1: Circle CenterX=0 CenterY=0 CenterZ=0 NormalX=0 NormalY=0 NormalZ=1 AngleXU=0 Radius=2.75
    g2: Circle CenterX=0 CenterY=7 CenterZ=0 NormalX=0 NormalY=0 NormalZ=1 AngleXU=0 Radius=1.7
    g3: Circle CenterX=-7 CenterY=0 CenterZ=0 NormalX=0 NormalY=0 NormalZ=1 AngleXU=0 Radius=1.7
    g4: Circle CenterX=0 CenterY=-7 CenterZ=0 NormalX=0 NormalY=0 NormalZ=1 AngleXU=0 Radius=1.7
    g5: Circle CenterX=7 CenterY=0 CenterZ=0 NormalX=0 NormalY=0 NormalZ=1 AngleXU=0 Radius=1.7
  constraints (14):
    c: Diameter(g0) = 30
    c: Coincident(g0,g-1)
    c: Diameter(g1) = 5.5
    c: Coincident(g1,g0)
    c: PointOnObject(g2,g-2)
    c: Diameter(g2) = 3.4
    c: DistanceY(g-1,g2) = 7
    c: PointOnObject(g3,g-1)
    c: Symmetric(g5,g3,g0)
    c: Symmetric(g2,g4,g0)
    c: DistanceX(g3,g-1) = 7
    c: Equal(g5,g4)
    c: Equal(g4,g3)
    c: Equal(g3,g2)
FEATURE [PartDesign::Pad] Pad005
  Direction = (0,-1,2e-16)
  Length = 5
  Length2 = 10
  Placement = pos=(0,0,0) rot=(1,0,0;1.5708rad)
  Profile = -> Sketch015
  ReferenceAxis = -> Sketch015 [N_Axis]
  Suppressed = false
  Type = 0
FEATURE [Sketcher::SketchObject] Sketch016
  ArcFitTolerance = 1e-06
  AttachmentOffset = pos=(0,0,2) rot=(0,0,1;0rad)
  AttachmentSupport = -> [XZ_Plane008]
  FullyConstrained = true
  MakeInternals = false
  MapMode = 5
  Placement = pos=(0,-2,4e-16) rot=(1,0,0;1.5708rad)
  expr: Constraints[1] = 2.7 * 2
  sketch-geometry (1):
    g0: Circle CenterX=0 CenterY=7 CenterZ=0 NormalX=0 NormalY=0 NormalZ=1 AngleXU=0 Radius=2.7
  constraints (3):
    c: PointOnObject(g0,g-2)
    c: Diameter(g0) = 5.4
    c: DistanceY(g-1,g0) = 7
FEATURE [PartDesign::Pocket] Pocket011
  BaseFeature = -> Pad005
  Direction = (0,1,-2e-16)
  Length = 1
  Length2 = 5
  Placement = pos=(0,0,0) rot=(1,0,0;1.5708rad)
  Profile = -> Sketch016
  ReferenceAxis = -> Sketch016 [N_Axis]
  Reversed = true
  Suppressed = false
  Type = 1
FEATURE [PartDesign::Pad] Pad006
  BaseFeature = -> Chamfer
  Direction = (-0.422618,0.906308,0)
  Length = 40
  Length2 = 10
  Profile = -> Chamfer [Face15]
  Suppressed = false
  Type = 0
FEATURE [Sketcher::SketchObject] Sketch017
  ArcFitTolerance = 1e-06
  AttachmentOffset = pos=(0,0,25) rot=(0,0,1;0rad)
  AttachmentSupport = -> [XZ_Plane]
  ExternalGeometry = -> [Pad006]
  FullyConstrained = true
  MakeInternals = false
  MapMode = 5
  Placement = pos=(0,25,-5.6e-15) rot=(0,0.707107,0.707107;3.14159rad)
  sketch-geometry (4):
    g0: LineSegment StartX=22.8664 StartY=5 StartZ=0 EndX=22.8664 EndY=7.1e-15 EndZ=0
    g1: LineSegment StartX=22.8664 StartY=7.1e-15 StartZ=0 EndX=52.8664 EndY=7.1e-15 EndZ=0
    g2: LineSegment StartX=52.8664 StartY=7.1e-15 StartZ=0 EndX=52.8664 EndY=5 EndZ=0
    g3: LineSegment StartX=52.8664 StartY=5 StartZ=0 EndX=22.8664 EndY=5 EndZ=0
  constraints (10):
    c: Coincident(g0,g1)
    c: Coincident(g1,g2)
    c: Coincident(g2,g3)
    c: Coincident(g3,g0)
    c: Vertical(g0)
    c: Horizontal(g1)
    c: Horizontal(g3)
    c: Coincident(g1,g-3)
    c: Coincident(g2,g-3)
    c: DistanceX(g3,g3) = 30
FEATURE [PartDesign::Pocket] Pocket012
  BaseFeature = -> Pad006
  Direction = (0,-1,2e-16)
  Length = 5
  Length2 = 5
  Profile = -> Sketch017
  ReferenceAxis = -> Sketch017 [N_Axis]
  Reversed = true
  Suppressed = false
  Type = 0
FEATURE [Sketcher::SketchObject] Sketch018
  ArcFitTolerance = 1e-06
  AttachmentOffset = pos=(0,0,5) rot=(0,0,1;0rad)
  AttachmentSupport = -> [XY_Plane]
  ExternalGeometry = -> [Pocket012]
  FullyConstrained = true
  MakeInternals = false
  MapMode = 5
  Placement = pos=(0,0,5) rot=(0,0,1;0rad)
  sketch-geometry (4):
    g0: LineSegment StartX=-49.2979 StartY=25 StartZ=0 EndX=-47.899 EndY=22 EndZ=0
    g1: LineSegment StartX=-49.2979 StartY=25 StartZ=0 EndX=-32.3059 EndY=25 EndZ=0
    g2: LineSegment StartX=-32.3059 StartY=25 StartZ=0 EndX=-30.907 EndY=22 EndZ=0
    g3: LineSegment StartX=-30.907 StartY=22 StartZ=0 EndX=-47.899 EndY=22 EndZ=0
  constraints (10):
    c: Coincident(g0,g-5)
    c: PointOnObject(g0,g-5)
    c: Coincident(g1,g0)
    c: Coincident(g1,g-4)
    c: Coincident(g2,g1)
    c: Coincident(g3,g2)
    c: Coincident(g3,g0)
    c: Parallel(g3,g1)
    c: Parallel(g2,g0)
    c: DistanceY(g2,g2) = 3
FEATURE [PartDesign::Pad] Pad007
  BaseFeature = -> Pocket012
  Direction = (0,0,1)
  Length = 10
  Length2 = 10
  Profile = -> Sketch018
  ReferenceAxis = -> Sketch018 [N_Axis]
  Suppressed = false
  Type = 0
FEATURE [Sketcher::SketchObject] Sketch019
  ArcFitTolerance = 1e-06
  AttachmentOffset = pos=(-40,10,-23) rot=(0,1,0;0.436332rad)
  AttachmentSupport = -> [XZ_Plane]
  FullyConstrained = false
  MakeInternals = false
  MapMode = 5
  Placement = pos=(-40,23,10) rot=(0.954201,0.211541,0.211541;1.61766rad)
  sketch-geometry (2):
    g0: Circle CenterX=0 CenterY=0 CenterZ=0 NormalX=0 NormalY=0 NormalZ=1 AngleXU=0 Radius=2.5
    g1: LineSegment [constr] StartX=-9 StartY=3.11249 StartZ=0 EndX=-9 EndY=-2.45643 EndZ=0
  constraints (4):
    c: Coincident(g0,g-1)
    c: Diameter(g0) = 5
    c: Vertical(g1)
    c: Distance(g1,g-2) = 9
FEATURE [PartDesign::Groove] Groove
  Angle = 360
  Angle2 = 60
  Axis = (0,-1e-15,-5.56892)
  Base = (-48.1568,19.1964,13.1125)
  BaseFeature = -> Pad007
  Profile = -> Sketch019
  ReferenceAxis = -> Sketch019 [Axis]
  Reversed = true
  Suppressed = false
  Type = 0
FEATURE [Sketcher::SketchObject] Sketch020
  ArcFitTolerance = 1e-06
  AttachmentOffset = pos=(0,0,0) rot=(0,0,1;0.436332rad)
  AttachmentSupport = -> [Groove]
  ExternalGeometry = -> [Groove]
  FullyConstrained = true
  MakeInternals = false
  MapMode = 5
  Placement = pos=(0,0,5) rot=(0,0,1;0.436332rad)
  sketch-geometry (8):
    g0: ArcOfCircle CenterX=-29.1136 CenterY=30.1818 CenterZ=0 NormalX=0 NormalY=0 NormalZ=1 AngleXU=0 Radius=3 StartAngle=1.13446 EndAngle=3.14159
    g1: ArcOfCircle CenterX=-23.7136 CenterY=27.6637 CenterZ=0 NormalX=0 NormalY=0 NormalZ=1 AngleXU=0 Radius=3 StartAngle=0 EndAngle=1.13446
    g2: ArcOfCircle CenterX=-29.1136 CenterY=16.9356 CenterZ=0 NormalX=0 NormalY=0 NormalZ=1 AngleXU=0 Radius=3 StartAngle=3.14159 EndAngle=4.71239
    g3: ArcOfCircle CenterX=-23.7136 CenterY=16.9356 CenterZ=0 NormalX=0 NormalY=0 NormalZ=1 AngleXU=0 Radius=3 StartAngle=4.71239 EndAngle=6.28319
    g4: LineSegment StartX=-32.1136 StartY=30.1818 StartZ=0 EndX=-32.1136 EndY=16.9356 EndZ=0
    g5: LineSegment StartX=-29.1136 StartY=13.9356 StartZ=0 EndX=-23.7136 EndY=13.9356 EndZ=0
    g6: LineSegment StartX=-20.7136 StartY=16.9356 StartZ=0 EndX=-20.7136 EndY=27.6637 EndZ=0
    g7: LineSegment StartX=-22.4458 StartY=30.3826 StartZ=0 EndX=-27.8458 EndY=32.9007 EndZ=0
  constraints (20):
    c: Tangent(g7,g0) = -1.5708
    c: Vertical(g4)
    c: Vertical(g6)
    c: Horizontal(g5)
    c: Tangent(g5,g2) = -1.5708
    c: Tangent(g4,g2) = -1.5708
    c: Tangent(g5,g3) = -1.5708
    c: Tangent(g6,g3) = -1.5708
    c: Tangent(g6,g1) = -1.5708
    c: Tangent(g7,g1) = -1.5708
    c: DistanceX(g1,g-4) = 2
    c: Distance(g0,g-3) = 2
    c: Angle(g7,g-1) = 0.436332
    c: Tangent(g4,g0) = -1.5708
    c: Equal(g0,g1)
    c: Equal(g1,g3)
    c: Equal(g3,g2)
    c: Radius(g2) = 3
    c: DistanceY(g-4,g3) = 2
    c: DistanceY(g0,g-3) = 10
FEATURE [PartDesign::Pocket] Pocket013
  BaseFeature = -> Groove
  Direction = (0,0,-1)
  Length = 5
  Length2 = 5
  Profile = -> Sketch020
  ReferenceAxis = -> Sketch020 [N_Axis]
  Suppressed = false
  Type = 0
FEATURE [PartDesign::Fillet] Fillet001
  Base = -> Pocket013 [Edge179,Edge185,Edge188]
  BaseFeature = -> Pocket013
  Radius = 3
  SupportTransform = false
  Suppressed = false
  UseAllEdges = false
FEATURE [PartDesign::Fillet] Fillet002
  Base = -> Fillet001 [Edge36,Edge10]
  BaseFeature = -> Fillet001
  Radius = 2
  SupportTransform = false
  Suppressed = false
  UseAllEdges = false
FEATURE [PartDesign::Body] Body  label="Partie_fixe_d"
  AllowCompound = false
  Group = -> [Sketch,Pad,Sketch001,Pocket,Sketch007,Pocket004,Sketch008,Pocket005,Sketch009,Pocket006,Pocket007,Sketch011,Pocket008,Sketch012,Pocket009,Fillet,Chamfer,Pad006,Sketch017,Pocket012,Sketch018,Pad007,Sketch019,Groove,Sketch020,Pocket013,Fillet001,Fillet002]
  Origin = -> Origin
  Placement = pos=(150,-82.5,0) rot=(0,0,1;0rad)
  Tip = -> Fillet002
FEATURE [PartDesign::PolarPattern] PolarPattern001
  Angle = 360
  Axis = -> Sketch016 [N_Axis]
  BaseFeature = -> Pocket011
  Mode = 0
  Occurrences = 4
  Offset = 120
  Originals = -> [Pocket011]
  Placement = pos=(0,0,0) rot=(1,0,0;1.5708rad)
  Suppressed = false
  TransformMode = 0
FEATURE [Sketcher::SketchObject] Sketch021
  ArcFitTolerance = 1e-06
  AttachmentSupport = -> [YZ_Plane008]
  ExternalGeometry = -> [PolarPattern001]
  FullyConstrained = true
  MakeInternals = false
  MapMode = 5
  Placement = pos=(0,0,0) rot=(0.57735,0.57735,0.57735;2.0944rad)
  sketch-geometry (4):
    g0: ArcOfCircle CenterX=-2.5 CenterY=16 CenterZ=0 NormalX=0 NormalY=0 NormalZ=1 AngleXU=0 Radius=1.80278 StartAngle=3.7296 EndAngle=5.69518
    g1: LineSegment [constr] StartX=-5 StartY=15 StartZ=0 EndX=3.6e-15 EndY=15 EndZ=0
    g2: LineSegment [constr] StartX=-2.5 StartY=16 StartZ=0 EndX=-2.5 EndY=15 EndZ=0
    g3: LineSegment StartX=-4 StartY=15 StartZ=0 EndX=-1 EndY=15 EndZ=0
  constraints (11):
    c: Coincident(g1,g-3)
    c: Coincident(g1,g-4)
    c: PointOnObject(g0,g1)
    c: PointOnObject(g0,g1)
    c: Coincident(g2,g0)
    c: Symmetric(g1,g1,g2)
    c: Vertical(g2)
    c: DistanceY(g2,g2) = 1
    c: Coincident(g3,g0)
    c: Coincident(g3,g0)
    c: Distance(g1,g0) = 1
FEATURE [PartDesign::Groove] Groove001
  Angle = 360
  Angle2 = 60
  Axis = (1e-16,1,-1e-16)
  Base = (0,0,0)
  BaseFeature = -> PolarPattern001
  Placement = pos=(0,0,0) rot=(1,0,0;1.5708rad)
  Profile = -> Sketch021
  ReferenceAxis = -> Y_Axis008
  Reversed = true
  Suppressed = false
  Type = 0
FEATURE [Sketcher::SketchObject] Sketch022
  ArcFitTolerance = 1e-06
  AttachmentSupport = -> [Groove001]
  FullyConstrained = true
  MakeInternals = false
  MapMode = 5
  Placement = pos=(0,-5,0) rot=(1,0,0;1.5708rad)
  sketch-geometry (4):
    g0: ArcOfCircle CenterX=0 CenterY=18 CenterZ=0 NormalX=0 NormalY=0 NormalZ=1 AngleXU=0 Radius=1 StartAngle=0 EndAngle=3.14159
    g1: LineSegment StartX=-1 StartY=18 StartZ=0 EndX=-1 EndY=10 EndZ=0
    g2: LineSegment StartX=-1 StartY=10 StartZ=0 EndX=1 EndY=10 EndZ=0
    g3: LineSegment StartX=1 StartY=10 StartZ=0 EndX=1 EndY=18 EndZ=0
  constraints (11):
    c: PointOnObject(g0,g-2)
    c: Vertical(g1)
    c: Coincident(g2,g1)
    c: Horizontal(g2)
    c: Vertical(g3)
    c: Coincident(g2,g3)
    c: DistanceY(g-1,g0) = 18
    c: Tangent(g1,g0) = -1.5708
    c: Tangent(g3,g0) = -1.5708
    c: Distance(g2,g2) = 2
    c: DistanceY(g-1,g1) = 10
FEATURE [PartDesign::Pad] Pad008
  BaseFeature = -> Groove001
  Direction = (0,-1,2e-16)
  Length = 5
  Length2 = 10
  Placement = pos=(0,0,0) rot=(1,0,0;1.5708rad)
  Profile = -> Sketch022
  ReferenceAxis = -> Sketch022 [N_Axis]
  Reversed = true
  Suppressed = false
  Type = 0
FEATURE [Sketcher::SketchObject] Sketch023
  ArcFitTolerance = 1e-06
  AttachmentSupport = -> [Pad008]
  ExternalGeometry = -> [Pad008]
  FullyConstrained = true
  MakeInternals = false
  MapMode = 5
  Placement = pos=(1,0,0) rot=(0.707107,0,0.707107;3.14159rad)
  sketch-geometry (3):
    g0: GeomPoint X=19 Y=2.5 Z=0
    g1: GeomPoint X=19 Y=0 Z=0
    g2: Circle CenterX=17 CenterY=2.5 CenterZ=0 NormalX=0 NormalY=0 NormalZ=1 AngleXU=0 Radius=0.75
  constraints (6):
    c: PointOnObject(g1,g-1)
    c: Symmetric(g1,g-3,g0)
    c: Horizontal(g2,g0)
    c: DistanceX(g2,g-3) = 2
    c: Diameter(g2) = 1.5
    c: Vertical(g0,g1)
FEATURE [PartDesign::Pocket] Pocket014
  BaseFeature = -> Pad008
  Direction = (-1,0,2e-16)
  Length = 5
  Length2 = 5
  Placement = pos=(0,0,0) rot=(1,0,0;1.5708rad)
  Profile = -> Sketch023
  ReferenceAxis = -> Sketch023 [N_Axis]
  Suppressed = false
  Type = 0
FEATURE [PartDesign::PolarPattern] PolarPattern002
  Angle = 360
  Axis = -> Sketch022 [N_Axis]
  BaseFeature = -> Pocket014
  Mode = 0
  Occurrences = 2
  Offset = 120
  Originals = -> [Pad008,Pocket014]
  Placement = pos=(0,0,0) rot=(1,0,0;1.5708rad)
  Suppressed = false
  TransformMode = 0
FEATURE [PartDesign::Body] Body004  label="devidoire"
  AllowCompound = false
  Group = -> [Sketch015,Pad005,Sketch016,Pocket011,PolarPattern001,Sketch021,Groove001,Sketch022,Pad008,Sketch023,Pocket014,PolarPattern002]
  Origin = -> Origin008
  Placement = pos=(0,-4.8,0) rot=(0,0,1;0rad)
  Tip = -> PolarPattern002
FEATURE [Sketcher::SketchObject] Sketch024
  ArcFitTolerance = 1e-06
  AttachmentSupport = -> [XZ_Plane009]
  FullyConstrained = true
  MakeInternals = false
  MapMode = 5
  Placement = pos=(0,0,0) rot=(1,0,0;1.5708rad)
  sketch-geometry (18):
    g0: LineSegment StartX=-10.15 StartY=29.65 StartZ=0 EndX=-10.15 EndY=-10.65 EndZ=0
    g1: LineSegment [constr] StartX=-10.15 StartY=-10.65 StartZ=0 EndX=10.15 EndY=-10.65 EndZ=0
    g2: LineSegment [constr] StartX=10.15 StartY=-10.65 StartZ=0 EndX=10.15 EndY=29.65 EndZ=0
    g3: LineSegment [constr] StartX=10.15 StartY=29.65 StartZ=0 EndX=-10.15 EndY=29.65 EndZ=0
    g4: LineSegment StartX=-14.85 StartY=37 StartZ=0 EndX=-14.85 EndY=-18 EndZ=0
    g5: LineSegment [constr] StartX=-14.85 StartY=-18 StartZ=0 EndX=14.85 EndY=-18 EndZ=0
    g6: LineSegment [constr] StartX=14.85 StartY=-18 StartZ=0 EndX=14.85 EndY=37 EndZ=0
    g7: LineSegment [constr] StartX=14.85 StartY=37 StartZ=0 EndX=-14.85 EndY=37 EndZ=0
    g8: GeomPoint X=-10.15 Y=9.5 Z=0
    g9: GeomPoint X=-14.85 Y=9.5 Z=0
    g10: LineSegment StartX=-14.85 StartY=37 StartZ=0 EndX=0 EndY=37 EndZ=0
    g11: LineSegment StartX=0 StartY=37 StartZ=0 EndX=0 EndY=29.65 EndZ=0
    g12: LineSegment StartX=0 StartY=29.65 StartZ=0 EndX=-10.15 EndY=29.65 EndZ=0
    g13: LineSegment StartX=-10.15 StartY=-10.65 StartZ=0 EndX=0 EndY=-10.65 EndZ=0
    g14: LineSegment StartX=0 StartY=-18 StartZ=0 EndX=-14.85 EndY=-18 EndZ=0
    g15: Circle CenterX=-6 CenterY=34.45 CenterZ=0 NormalX=0 NormalY=0 NormalZ=1 AngleXU=0 Radius=2.25
    g16: Circle CenterX=-6 CenterY=-15.5 CenterZ=0 NormalX=0 NormalY=0 NormalZ=1 AngleXU=0 Radius=2.25
    g17: LineSegment StartX=0 StartY=-10.65 StartZ=0 EndX=0 EndY=-18 EndZ=0
  constraints (44):
    c: Coincident(g0,g1)
    c: Coincident(g1,g2)
    c: Coincident(g2,g3)
    c: Coincident(g3,g0)
    c: Vertical(g0)
    c: Vertical(g2)
    c: Horizontal(g1)
    c: Coincident(g4,g5)
    c: Coincident(g5,g6)
    c: Coincident(g6,g7)
    c: Coincident(g7,g4)
    c: Vertical(g4)
    c: Vertical(g6)
    c: Horizontal(g5)
    c: DistanceX(g7,g7) = 29.7
    c: Symmetric(g4,g6,g-2)
    c: Symmetric(g0,g2,g-2)
    c: DistanceX(g3,g3) = 20.3
    c: DistanceY(g0,g0) = 40.3
    c: Symmetric(g0,g0,g8)
    c: DistanceY(g-1,g8) = 9.5
    c: Symmetric(g4,g4,g9)
    c: Horizontal(g9,g8)
    c: DistanceY(g4,g4) = 55
    c: Coincident(g10,g4)
    c: PointOnObject(g10,g-2)
    c: Coincident(g11,g10)
    c: PointOnObject(g11,g-2)
    c: Coincident(g12,g11)
    c: Horizontal(g12)
    c: Coincident(g13,g0)
    c: Symmetric(g1,g1,g13)
    c: Symmetric(g5,g5,g14)
    c: Coincident(g14,g4)
    c: Horizontal(g10)
    c: Coincident(g0,g12)
    c: Diameter(g15) = 4.5
    c: DistanceY(g-1,g15) = 34.45
    c: DistanceX(g15,g-1) = 6
    c: Vertical(g16,g15)
    c: Equal(g15,g16)
    c: DistanceY(g16,g-1) = 15.5
    c: Coincident(g17,g13)
    c: Coincident(g17,g14)
FEATURE [PartDesign::Pad] Pad009
  Direction = (0,-1,2e-16)
  Length = 10
  Length2 = 10
  Placement = pos=(0,0,0) rot=(1,0,0;1.5708rad)
  Profile = -> Sketch024
  ReferenceAxis = -> Sketch024 [N_Axis]
  Reversed = true
  Suppressed = false
  Type = 0
FEATURE [Sketcher::SketchObject] Sketch025
  ArcFitTolerance = 1e-06
  AttachmentSupport = -> [Pad009]
  ExternalGeometry = -> [Pad009]
  FullyConstrained = true
  MakeInternals = false
  MapMode = 5
  Placement = pos=(-14.85,0,0) rot=(0.707107,0,-0.707107;3.14159rad)
  sketch-geometry (4):
    g0: LineSegment StartX=4.15 StartY=0 StartZ=0 EndX=4.15 EndY=-4 EndZ=0
    g1: LineSegment StartX=4.15 StartY=-4 StartZ=0 EndX=8.85 EndY=-4 EndZ=0
    g2: LineSegment StartX=8.85 StartY=-4 StartZ=0 EndX=8.85 EndY=0 EndZ=0
    g3: LineSegment StartX=8.85 StartY=0 StartZ=0 EndX=4.15 EndY=0 EndZ=0
  constraints (12):
    c: Coincident(g0,g1)
    c: Coincident(g1,g2)
    c: Coincident(g2,g3)
    c: Coincident(g3,g0)
    c: Vertical(g0)
    c: Vertical(g2)
    c: Horizontal(g1)
    c: Horizontal(g3)
    c: PointOnObject(g0,g-1)
    c: DistanceX(g3,g3) = 4.7
    c: DistanceY(g2,g2) = 4
    c: DistanceX(g2,g-3) = 9.15
FEATURE [PartDesign::Pad] Pad010
  BaseFeature = -> Pad009
  Direction = (-1,0,-2e-16)
  Length = 31
  Length2 = 10
  Placement = pos=(0,0,0) rot=(1,0,0;1.5708rad)
  Profile = -> Sketch025
  ReferenceAxis = -> Sketch025 [N_Axis]
  Suppressed = false
  Type = 0
FEATURE [Sketcher::SketchObject] Sketch026
  ArcFitTolerance = 1e-06
  AttachmentSupport = -> [Pad010]
  ExternalGeometry = -> [Pad010]
  FullyConstrained = true
  MakeInternals = false
  MapMode = 5
  Placement = pos=(0,4,-9e-16) rot=(-1,0,0;1.5708rad)
  sketch-geometry (4):
    g0: LineSegment StartX=-45.85 StartY=8.85 StartZ=0 EndX=-45.85 EndY=4.15 EndZ=0
    g1: LineSegment StartX=-45.85 StartY=4.15 StartZ=0 EndX=-36.15 EndY=4.15 EndZ=0
    g2: LineSegment StartX=-36.15 StartY=4.15 StartZ=0 EndX=-36.15 EndY=8.85 EndZ=0
    g3: LineSegment StartX=-36.15 StartY=8.85 StartZ=0 EndX=-45.85 EndY=8.85 EndZ=0
  constraints (10):
    c: Coincident(g0,g1)
    c: Coincident(g1,g2)
    c: Coincident(g2,g3)
    c: Coincident(g3,g0)
    c: Vertical(g2)
    c: Horizontal(g1)
    c: Horizontal(g3)
    c: Coincident(g0,g-3)
    c: Coincident(g0,g-3)
    c: DistanceX(g3,g3) = 9.7
FEATURE [PartDesign::Pad] Pad011
  BaseFeature = -> Pad010
  Direction = (0,1,2e-16)
  Length = 5
  Length2 = 10
  Placement = pos=(0,0,0) rot=(1,0,0;1.5708rad)
  Profile = -> Sketch026
  ReferenceAxis = -> Sketch026 [N_Axis]
  Suppressed = false
  Type = 0
FEATURE [Sketcher::SketchObject] Sketch027
  ArcFitTolerance = 1e-06
  AttachmentSupport = -> [Pad011]
  ExternalGeometry = -> [Pad011]
  FullyConstrained = true
  MakeInternals = false
  MapMode = 5
  Placement = pos=(0,10,0) rot=(-1,0,0;1.5708rad)
  sketch-geometry (8):
    g0: LineSegment StartX=-14.85 StartY=18 StartZ=0 EndX=-14.85 EndY=10.65 EndZ=0
    g1: LineSegment StartX=-14.85 StartY=10.65 StartZ=0 EndX=0 EndY=10.65 EndZ=0
    g2: LineSegment StartX=0 StartY=10.65 StartZ=0 EndX=0 EndY=18 EndZ=0
    g3: LineSegment StartX=0 StartY=18 StartZ=0 EndX=-14.85 EndY=18 EndZ=0
    g4: LineSegment StartX=-14.85 StartY=-37 StartZ=0 EndX=0 EndY=-37 EndZ=0
    g5: LineSegment StartX=0 StartY=-37 StartZ=0 EndX=0 EndY=-29.65 EndZ=0
    g6: LineSegment StartX=0 StartY=-29.65 StartZ=0 EndX=-14.85 EndY=-29.65 EndZ=0
    g7: LineSegment StartX=-14.85 StartY=-29.65 StartZ=0 EndX=-14.85 EndY=-37 EndZ=0
  constraints (21):
    c: Coincident(g0,g1)
    c: Coincident(g1,g2)
    c: Coincident(g2,g3)
    c: Coincident(g3,g0)
    c: Vertical(g0)
    c: Vertical(g2)
    c: Horizontal(g1)
    c: Horizontal(g3)
    c: Coincident(g0,g-3)
    c: PointOnObject(g1,g-2)
    c: PointOnObject(g-4,g1)
    c: Coincident(g4,g5)
    c: Coincident(g5,g6)
    c: Coincident(g6,g7)
    c: Coincident(g7,g4)
    c: Horizontal(g4)
    c: Horizontal(g6)
    c: Vertical(g5)
    c: Vertical(g7)
    c: Coincident(g4,g-6)
    c: Coincident(g5,g-5)
FEATURE [PartDesign::Pocket] Pocket015
  BaseFeature = -> Pad011
  Direction = (0,-1,-2e-16)
  Length = 7
  Length2 = 5
  Placement = pos=(0,0,0) rot=(1,0,0;1.5708rad)
  Profile = -> Sketch027
  ReferenceAxis = -> Sketch027 [N_Axis]
  Suppressed = false
  Type = 0
FEATURE [PartDesign::Pocket] Pocket016
  BaseFeature = -> Pocket015
  Direction = (0,-2e-16,-1)
  Length = 1
  Length2 = 5
  Placement = pos=(0,0,0) rot=(1,0,0;1.5708rad)
  Profile = -> Pocket015 [Face1]
  Suppressed = false
  Type = 0
FEATURE [PartDesign::Pocket] Pocket017
  BaseFeature = -> Pocket016
  Direction = (0,2e-16,1)
  Length = 1
  Length2 = 5
  Placement = pos=(0,0,0) rot=(1,0,0;1.5708rad)
  Profile = -> Pocket016 [Face4]
  Suppressed = false
  Type = 0
FEATURE [PartDesign::Fillet] Fillet003
  Base = -> Pocket017 [Edge17]
  BaseFeature = -> Pocket017
  Placement = pos=(0,0,0) rot=(1,0,0;1.5708rad)
  Radius = 12
  SupportTransform = false
  Suppressed = false
  UseAllEdges = false
FEATURE [PartDesign::Chamfer] Chamfer001
  Angle = 45
  Base = -> Fillet003 [Edge24]
  BaseFeature = -> Fillet003
  ChamferType = 1
  FlipDirection = false
  Placement = pos=(0,0,0) rot=(1,0,0;1.5708rad)
  Size = 1.7
  Size2 = 10
  SupportTransform = false
  Suppressed = false
  UseAllEdges = false
FEATURE [PartDesign::Mirrored] Mirrored
  BaseFeature = -> Chamfer001
  MirrorPlane = -> YZ_Plane009
  Placement = pos=(0,0,0) rot=(1,0,0;1.5708rad)
  Suppressed = false
  TransformMode = 1
FEATURE [PartDesign::Body] Body005  label="support_servo"
  AllowCompound = false
  Group = -> [Sketch024,Pad009,Sketch025,Pad010,Sketch026,Pad011,Sketch027,Pocket015,Pocket016,Pocket017,Fillet003,Chamfer001,Mirrored]
  Origin = -> Origin009
  Placement = pos=(0,13.9,0) rot=(0,0,1;0rad)
  Tip = -> Mirrored
FEATURE [App::Link] Link003  label="open_tin_can001"
  LinkPlacement = pos=(-100,0,0) rot=(0,0,1;0rad)
  LinkTransform = true
  LinkedObject = -> open_tin_can
  Placement = pos=(-100,0,0) rot=(0,0,1;0rad)
FEATURE [App::Part] Part  label="OuterCanMover_D"
  Group = -> [Body,Part001,open_tin_can,Screw,Link003]
  Origin = -> Origin001
  Placement = pos=(0,0,2) rot=(0,0,1;0rad)
FEATURE [App::LinkElement] Link_i004
  LinkedObject = -> Body008
  _LinkOwner = 3722
FEATURE [App::LinkElement] Link_i005
  LinkPlacement = pos=(0,10,0) rot=(0,0,1;0rad)
  LinkedObject = -> Body008
  Placement = pos=(0,10,0) rot=(0,0,1;0rad)
  _LinkOwner = 3722
FEATURE [App::LinkElement] Link_i006
  LinkPlacement = pos=(0,20,0) rot=(0,0,1;0rad)
  LinkedObject = -> Body008
  Placement = pos=(0,20,0) rot=(0,0,1;0rad)
  _LinkOwner = 3722
FEATURE [App::LinkElement] Link_i007
  LinkPlacement = pos=(0,30,0) rot=(0,0,1;0rad)
  LinkedObject = -> Body008
  Placement = pos=(0,30,0) rot=(0,0,1;0rad)
  _LinkOwner = 3722
FEATURE [App::Link] Link004  label="aimant003"
  ElementCount = 4
  ElementList = -> [Link_i004,Link_i005,Link_i006,Link_i007]
  LinkPlacement = pos=(-2.28509e-05,1,5.00001) rot=(1,0,0;1.5708rad)
  LinkedObject = -> Body008
  Placement = pos=(-2.28509e-05,1,5.00001) rot=(1,0,0;1.5708rad)
FEATURE [Sketcher::SketchObject] Sketch028
  ArcFitTolerance = 1e-06
  AttachmentSupport = -> [XY_Plane011]
  FullyConstrained = true
  MakeInternals = false
  MapMode = 5
  sketch-geometry (10):
    g0: Circle [constr] CenterX=0 CenterY=-62.5 CenterZ=0 NormalX=0 NormalY=0 NormalZ=1 AngleXU=0 Radius=36.25
    g1: ArcOfCircle CenterX=0 CenterY=-62.5 CenterZ=0 NormalX=0 NormalY=0 NormalZ=1 AngleXU=0 Radius=36.5 StartAngle=0.458985 EndAngle=2.68261
    g2: LineSegment StartX=8.05039 StartY=9 StartZ=0 EndX=-8.05039 EndY=9 EndZ=0
    g3: LineSegment StartX=-12.5 StartY=6.28057 StartZ=0 EndX=-38.0816 EndY=-43.6317 EndZ=0
    g4: ArcOfCircle CenterX=8.05039 CenterY=4 CenterZ=0 NormalX=0 NormalY=0 NormalZ=1 AngleXU=0 Radius=5 StartAngle=0.473623 EndAngle=1.5708
    g5: LineSegment StartX=12.5 StartY=6.28057 StartZ=0 EndX=38.0816 EndY=-43.6317 EndZ=0
    g6: ArcOfCircle CenterX=-35.4119 CenterY=-45 CenterZ=0 NormalX=0 NormalY=0 NormalZ=1 AngleXU=0 Radius=3 StartAngle=2.66797 EndAngle=5.8242
    g7: ArcOfCircle CenterX=35.4119 CenterY=-45 CenterZ=0 NormalX=0 NormalY=0 NormalZ=1 AngleXU=0 Radius=3 StartAngle=3.60058 EndAngle=6.75681
    g8: LineSegment [constr] StartX=-1.8e-15 StartY=9 StartZ=0 EndX=-1.8e-15 EndY=-26 EndZ=0
    g9: ArcOfCircle CenterX=-8.05039 CenterY=4 CenterZ=0 NormalX=0 NormalY=0 NormalZ=1 AngleXU=0 Radius=5 StartAngle=1.5708 EndAngle=2.66797
  constraints (25):
    c: Coincident(g1,g0)
    c: Diameter(g0) = 72.5
    c: Horizontal(g2)
    c: Tangent(g2,g4) = -1.5708
    c: PointOnObject(g0,g-2)
    c: DistanceY(g0,g-1) = 62.5
    c: Tangent(g3,g6) = -1.5708
    c: Tangent(g1,g6) = 1.5708
    c: Tangent(g1,g7) = 1.5708
    c: Tangent(g5,g7) = 1.5708
    c: Equal(g7,g6)
    c: Radius(g6) = 3
    c: PointOnObject(g8,g1)
    c: Symmetric(g7,g6,g8)
    c: Tangent(g2,g9) = -1.5708
    c: Tangent(g3,g9) = -1.5708
    c: Radius(g9) = 5
    c: Diameter(g1) = 73
    c: Tangent(g5,g4) = 1.5708
    c: Equal(g4,g9)
    c: Distance(g3,g4) = 25
    c: DistanceY(g8,g2) = 35
    c: DistanceY(g7,g-1) = 45
    c: Symmetric(g2,g2,g8)
    c: PointOnObject(g8,g2)
FEATURE [PartDesign::Pad] Pad012
  Direction = (0,0,1)
  Length = 50
  Length2 = 10
  Profile = -> Sketch028
  ReferenceAxis = -> Sketch028 [N_Axis]
  Suppressed = false
  Type = 0
FEATURE [Sketcher::SketchObject] Sketch029
  ArcFitTolerance = 1e-06
  AttachmentOffset = pos=(0,0,5) rot=(0,0,1;0rad)
  AttachmentSupport = -> [XY_Plane011]
  ExternalGeometry = -> [Pad012]
  FullyConstrained = true
  MakeInternals = false
  MapMode = 5
  Placement = pos=(0,0,5) rot=(0,0,1;0rad)
  sketch-geometry (22):
    g0: LineSegment [constr] StartX=-7.7 StartY=11.0798 StartZ=0 EndX=-7.7 EndY=6.0798 EndZ=0
    g1: LineSegment StartX=7.7 StartY=-25.6202 StartZ=0 EndX=7.7 EndY=4.5798 EndZ=0
    g2: LineSegment StartX=-7.7 StartY=11.0798 StartZ=0 EndX=7.7 EndY=11.0798 EndZ=0
    g3: ArcOfCircle CenterX=0 CenterY=-62.5 CenterZ=0 NormalX=0 NormalY=0 NormalZ=1 AngleXU=0 Radius=36.5 StartAngle=1.38619 EndAngle=1.7554
    g4: LineSegment [constr] StartX=0 StartY=-62.5 StartZ=0 EndX=0 EndY=11.0798 EndZ=0
    g5: LineSegment StartX=-7.7 StartY=-25.6202 StartZ=0 EndX=-6.7 EndY=-25.6202 EndZ=0
    g6: LineSegment StartX=7.7 StartY=-25.6202 StartZ=0 EndX=6.7 EndY=-25.6202 EndZ=0
    g7: LineSegment StartX=-6.7 StartY=-25.6202 StartZ=0 EndX=-6.7 EndY=-26.6202 EndZ=0
    g8: LineSegment StartX=6.7 StartY=-25.6202 StartZ=0 EndX=6.7 EndY=-26.6202 EndZ=0
    g9: LineSegment [constr] StartX=-7.7 StartY=-25.6202 StartZ=0 EndX=7.7 EndY=-25.6202 EndZ=0
    g10: LineSegment StartX=-7.7 StartY=6.0798 StartZ=0 EndX=-6.2 EndY=6.0798 EndZ=0
    g11: LineSegment StartX=7.7 StartY=4.5798 StartZ=0 EndX=6.2 EndY=4.5798 EndZ=0
    g12: LineSegment StartX=-6.2 StartY=6.0798 StartZ=0 EndX=-6.2 EndY=4.5798 EndZ=0
    g13: LineSegment StartX=6.2 StartY=6.0798 StartZ=0 EndX=6.2 EndY=4.5798 EndZ=0
    g14: LineSegment StartX=-7.7 StartY=4.5798 StartZ=0 EndX=-7.7 EndY=-25.6202 EndZ=0
    g15: LineSegment [constr] StartX=7.7 StartY=6.0798 StartZ=0 EndX=7.7 EndY=11.0798 EndZ=0
    g16: LineSegment StartX=6.2 StartY=6.0798 StartZ=0 EndX=7.7 EndY=6.0798 EndZ=0
    g17: LineSegment StartX=-6.2 StartY=4.5798 StartZ=0 EndX=-7.7 EndY=4.5798 EndZ=0
    g18: LineSegment [constr] StartX=-7.7 StartY=6.0798 StartZ=0 EndX=-7.7 EndY=4.5798 EndZ=0
    g19: LineSegment [constr] StartX=7.7 StartY=6.0798 StartZ=0 EndX=7.7 EndY=4.5798 EndZ=0
    g20: LineSegment StartX=7.7 StartY=11.0798 StartZ=0 EndX=7.7 EndY=6.0798 EndZ=0
    g21: LineSegment StartX=-7.7 StartY=11.0798 StartZ=0 EndX=-7.7 EndY=6.0798 EndZ=0
  constraints (56):
    c: Coincident(g2,g15)
    c: Parallel(g1,g0)
    c: Coincident(g4,g3)
    c: Parallel(g4,g1)
    c: Coincident(g2,g0)
    c: Horizontal(g2)
    c: Symmetric(g0,g15,g4)
    c: Coincident(g7,g5)
    c: Coincident(g8,g6)
    c: Coincident(g3,g8)
    c: Symmetric(g6,g5,g4)
    c: Coincident(g9,g5)
    c: Coincident(g9,g6)
    c: PointOnObject(g6,g9)
    c: PointOnObject(g5,g9)
    c: Perpendicular(g5,g7)
    c: Perpendicular(g6,g8)
    c: Coincident(g3,g7)
    c: Distance(g7,g7) = 1
    c: Distance(g5,g5) = 1
    c: Coincident(g14,g5)
    c: Coincident(g1,g6)
    c: Distance(g1,g14) = 15.4
    c: PointOnObject(g16,g15)
    c: Distance(g17,g10) = 1.5
    c: Symmetric(g12,g13,g4)
    c: Perpendicular(g0,g10) = 1.5708
    c: PointOnObject(g14,g11)
    c: Perpendicular(g1,g11) = 1.5708
    c: PointOnObject(g15,g16)
    c: Coincident(g11,g13)
    c: Coincident(g17,g12)
    c: Perpendicular(g10,g12) = 4.71239
    c: Perpendicular(g12,g17)
    c: Perpendicular(g15,g16)
    c: Parallel(g15,g1)
    c: Coincident(g18,g0)
    c: Coincident(g18,g17)
    c: Coincident(g19,g15)
    c: Coincident(g19,g1)
    c: Parallel(g19,g15)
    c: Coincident(g13,g16)
    c: Parallel(g18,g0)
    c: Coincident(g14,g17)
    c: Equal(g11,g17)
    c: Distance(g14,g5) = 30.2
    c: Parallel(g1,g14)
    c: Distance(g10,g10) = 1.5
    c: Coincident(g20,g16)
    c: Coincident(g2,g20)
    c: Coincident(g21,g0)
    c: Coincident(g21,g0)
    c: Vertical(g21)
    c: PointOnObject(g3,g-3)
    c: Distance(g21,g21) = 5
    c: Coincident(g3,g-3)
FEATURE [PartDesign::Pocket] Pocket018
  BaseFeature = -> Pad012
  Direction = (0,0,-1)
  Length = 5
  Length2 = 5
  Profile = -> Sketch029
  ReferenceAxis = -> Sketch029 [N_Axis]
  Reversed = true
  Suppressed = false
  Type = 1
FEATURE [Sketcher::SketchObject] Sketch030
  ArcFitTolerance = 1e-06
  AttachmentSupport = -> [YZ_Plane013]
  FullyConstrained = true
  MakeInternals = false
  MapMode = 5
  Placement = pos=(0,0,0) rot=(0.57735,0.57735,0.57735;2.0944rad)
  sketch-geometry (24):
    g0: LineSegment StartX=0 StartY=0 StartZ=0 EndX=0 EndY=40.625 EndZ=0
    g1: LineSegment StartX=0 StartY=0 StartZ=0 EndX=2 EndY=0 EndZ=0
    g2: LineSegment StartX=2 StartY=0 StartZ=0 EndX=2 EndY=40.625 EndZ=0
    g3: LineSegment StartX=6.75 StartY=40.625 StartZ=0 EndX=6.75 EndY=4.375 EndZ=0
    g4: LineSegment StartX=8.75 StartY=40.625 StartZ=0 EndX=8.75 EndY=4.375 EndZ=0
    g5: LineSegment StartX=13.5 StartY=40.625 StartZ=0 EndX=13.5 EndY=4.375 EndZ=0
    g6: LineSegment StartX=15.5 StartY=40.625 StartZ=0 EndX=15.5 EndY=4.375 EndZ=0
    g7: ArcOfCircle CenterX=4.375 CenterY=40.625 CenterZ=0 NormalX=0 NormalY=0 NormalZ=1 AngleXU=0 Radius=4.375 StartAngle=-9e-16 EndAngle=3.14159
    g8: ArcOfCircle CenterX=4.375 CenterY=40.625 CenterZ=0 NormalX=0 NormalY=0 NormalZ=1 AngleXU=0 Radius=2.375 StartAngle=4e-16 EndAngle=3.14159
    g9: ArcOfCircle CenterX=11.125 CenterY=4.375 CenterZ=0 NormalX=0 NormalY=0 NormalZ=1 AngleXU=0 Radius=4.375 StartAngle=3.14159 EndAngle=6.28319
    g10: ArcOfCircle CenterX=11.125 CenterY=4.375 CenterZ=0 NormalX=0 NormalY=0 NormalZ=1 AngleXU=0 Radius=2.375 StartAngle=3.14159 EndAngle=6.28319
    g11: ArcOfCircle CenterX=17.875 CenterY=40.625 CenterZ=0 NormalX=0 NormalY=0 NormalZ=1 AngleXU=0 Radius=4.375 StartAngle=3e-16 EndAngle=3.14159
    g12: ArcOfCircle CenterX=17.875 CenterY=40.625 CenterZ=0 NormalX=0 NormalY=0 NormalZ=1 AngleXU=0 Radius=2.375 StartAngle=8e-16 EndAngle=3.14159
    g13: LineSegment StartX=20.25 StartY=40.625 StartZ=0 EndX=20.25 EndY=4.375 EndZ=0
    g14: LineSegment StartX=22.25 StartY=40.625 StartZ=0 EndX=22.25 EndY=4.375 EndZ=0
    g15: LineSegment [constr] StartX=0 StartY=45 StartZ=0 EndX=29 EndY=45 EndZ=0
    g16: LineSegment [constr] StartX=0 StartY=0 StartZ=0 EndX=29 EndY=0 EndZ=0
    g17: LineSegment [constr] StartX=0 StartY=4.375 StartZ=0 EndX=29 EndY=4.375 EndZ=0
    g18: LineSegment [constr] StartX=0 StartY=40.625 StartZ=0 EndX=29 EndY=40.625 EndZ=0
    g19: ArcOfCircle CenterX=24.625 CenterY=4.375 CenterZ=0 NormalX=0 NormalY=0 NormalZ=1 AngleXU=0 Radius=4.375 StartAngle=3.14159 EndAngle=6.28319
    g20: ArcOfCircle CenterX=24.625 CenterY=4.375 CenterZ=0 NormalX=0 NormalY=0 NormalZ=1 AngleXU=0 Radius=2.375 StartAngle=3.14159 EndAngle=6.28319
    g21: LineSegment StartX=27 StartY=4.375 StartZ=0 EndX=27 EndY=45 EndZ=0
    g22: LineSegment StartX=29 StartY=4.375 StartZ=0 EndX=29 EndY=45 EndZ=0
    g23: LineSegment StartX=27 StartY=45 StartZ=0 EndX=29 EndY=45 EndZ=0
  constraints (60):
    c: PointOnObject(g0,g-2)
    c: Coincident(g1,g0)
    c: Horizontal(g1)
    c: Coincident(g2,g1)
    c: Vertical(g2)
    c: Vertical(g3)
    c: Vertical(g4)
    c: Vertical(g5)
    c: Vertical(g6)
    c: Tangent(g8,g2) = 1.5708
    c: Tangent(g8,g3) = 1.5708
    c: Tangent(g9,g3) = -1.5708
    c: Tangent(g7,g4) = 1.5708
    c: Tangent(g7,g0) = 1.5708
    c: Tangent(g10,g4) = -1.5708
    c: Tangent(g10,g5) = 1.5708
    c: Tangent(g9,g6) = 1.5708
    c: Tangent(g12,g6) = -1.5708
    c: Tangent(g11,g5) = -1.5708
    c: Vertical(g13)
    c: Vertical(g14)
    c: Tangent(g14,g11) = 1.5708
    c: Tangent(g13,g12) = 1.5708
    c: Horizontal(g15)
    c: Coincident(g16,g0)
    c: Horizontal(g16)
    c: Horizontal(g17)
    c: Coincident(g18,g0)
    c: Horizontal(g18)
    c: Coincident(g11,g12)
    c: PointOnObject(g11,g18)
    c: PointOnObject(g9,g17)
    c: Coincident(g9,g10)
    c: Coincident(g7,g8)
    c: Tangent(g15,g7)
    c: Tangent(g15,g11)
    c: Tangent(g9,g16)
    c: PointOnObject(g19,g17)
    c: Coincident(g20,g19)
    c: Vertical(g21)
    c: Coincident(g23,g21)
    c: Coincident(g23,g22)
    c: Horizontal(g23)
    c: PointOnObject(g21,g15)
    c: Tangent(g21,g20) = -1.5708
    c: Tangent(g22,g19) = -1.5708
    c: Tangent(g19,g16)
    c: Tangent(g20,g14) = -1.5708
    c: Coincident(g19,g17)
    c: Vertical(g17,g18)
    c: Vertical(g18,g15)
    c: Vertical(g15,g16)
    c: Tangent(g19,g13) = -1.5708
    c: Equal(g10,g8)
    c: DistanceY(g0,g15) = 45
    c: Coincident(g0,g-1)
    c: PointOnObject(g15,g-2)
    c: Distance(g1,g1) = 2
    c: DistanceX(g15,g15) = 29
    c: Vertical(g17,g0)
FEATURE [PartDesign::Pad] Pad013
  Direction = (1,0,0)
  Length = 15
  Length2 = 10
  Midplane = true
  Placement = pos=(0,0,0) rot=(1,1,1;2.0944rad)
  Profile = -> Sketch030
  ReferenceAxis = -> Sketch030 [N_Axis]
  Suppressed = false
  Type = 0
FEATURE [Sketcher::SketchObject] Sketch031
  ArcFitTolerance = 1e-06
  AttachmentOffset = pos=(0,0,-3) rot=(0,0,1;0rad)
  AttachmentSupport = -> [XZ_Plane013]
  ExternalGeometry = -> [Pad013]
  FullyConstrained = true
  MakeInternals = false
  MapMode = 5
  Placement = pos=(0,3,-7e-16) rot=(1,0,0;1.5708rad)
  sketch-geometry (2):
    g0: Circle CenterX=0 CenterY=22.5 CenterZ=0 NormalX=0 NormalY=0 NormalZ=1 AngleXU=0 Radius=3
    g1: GeomPoint X=0 Y=45 Z=0
  constraints (4):
    c: PointOnObject(g0,g-2)
    c: PointOnObject(g1,g-3)
    c: Symmetric(g1,g-1,g0)
    c: Diameter(g0) = 6
FEATURE [PartDesign::Pocket] Pocket019
  BaseFeature = -> Pad013
  Direction = (0,1,-2e-16)
  Length = 5
  Length2 = 5
  Placement = pos=(0,0,0) rot=(1,1,1;2.0944rad)
  Profile = -> Sketch031
  ReferenceAxis = -> Sketch031 [N_Axis]
  Suppressed = false
  Type = 1
FEATURE [PartDesign::Pad] Pad015
  BaseFeature = -> Pocket019
  Direction = (-4e-16,-1,2e-16)
  Length = 1
  Length2 = 10
  Placement = pos=(0,0,0) rot=(1,1,1;2.0944rad)
  Profile = -> Pocket019 [Face9]
  Suppressed = false
  Type = 0
FEATURE [Sketcher::SketchObject] Sketch032
  ArcFitTolerance = 1e-06
  AttachmentSupport = -> [XY_Plane014]
  FullyConstrained = true
  MakeInternals = false
  MapMode = 5
  sketch-geometry (4):
    g0: LineSegment StartX=4.5 StartY=-2.25 StartZ=0 EndX=4.5 EndY=2.25 EndZ=0
    g1: LineSegment StartX=4.5 StartY=2.25 StartZ=0 EndX=-4.5 EndY=2.25 EndZ=0
    g2: LineSegment StartX=-4.5 StartY=2.25 StartZ=0 EndX=-4.5 EndY=-2.25 EndZ=0
    g3: LineSegment StartX=-4.5 StartY=-2.25 StartZ=0 EndX=4.5 EndY=-2.25 EndZ=0
  constraints (11):
    c: Coincident(g0,g1)
    c: Coincident(g1,g2)
    c: Coincident(g2,g3)
    c: Coincident(g3,g0)
    c: Vertical(g0)
    c: Vertical(g2)
    c: Horizontal(g1)
    c: Horizontal(g3)
    c: Symmetric(g1,g0,g-1)
    c: DistanceX(g1,g1) = 9
    c: Distance(g2,g2) = 4.5
FEATURE [PartDesign::Pad] Pad014
  Direction = (0,0,1)
  Length = 2.5
  Length2 = 10
  Profile = -> Sketch032
  ReferenceAxis = -> Sketch032 [N_Axis]
  Suppressed = false
  Type = 0
FEATURE [PartDesign::Body] Body008  label="aimant002"
  AllowCompound = false
  Group = -> [Sketch032,Pad014]
  Origin = -> Origin014
  Tip = -> Pad014
FEATURE [Sketcher::SketchObject] Sketch033
  ArcFitTolerance = 1e-06
  AttachmentOffset = pos=(0,0,1.5) rot=(0,0,1;0rad)
  AttachmentSupport = -> [XZ_Plane013]
  FullyConstrained = true
  MakeInternals = false
  MapMode = 5
  Placement = pos=(0,-1.5,3e-16) rot=(1,0,0;1.5708rad)
  sketch-geometry (6):
    g0: LineSegment StartX=-4.6 StartY=2.65 StartZ=0 EndX=4.6 EndY=2.65 EndZ=0
    g1: LineSegment StartX=4.6 StartY=2.65 StartZ=0 EndX=4.6 EndY=7.35 EndZ=0
    g2: LineSegment StartX=4.6 StartY=7.35 StartZ=0 EndX=-4.6 EndY=7.35 EndZ=0
    g3: LineSegment StartX=-4.6 StartY=7.35 StartZ=0 EndX=-4.6 EndY=2.65 EndZ=0
    g4: GeomPoint X=0 Y=5 Z=0
    g5: Circle CenterX=0 CenterY=5 CenterZ=0 NormalX=0 NormalY=0 NormalZ=1 AngleXU=0 Radius=1
  constraints (15):
    c: Coincident(g0,g1)
    c: Coincident(g1,g2)
    c: Coincident(g2,g3)
    c: Coincident(g3,g0)
    c: Horizontal(g2)
    c: Vertical(g1)
    c: Vertical(g3)
    c: Distance(g1,g3) = 9.2
    c: Distance(g0,g2) = 4.7
    c: PointOnObject(g4,g-2)
    c: Symmetric(g1,g0,g4)
    c: Horizontal(g0)
    c: DistanceY(g-1,g4) = 5
    c: Diameter(g5) = 2
    c: Coincident(g5,g4)
FEATURE [PartDesign::Pocket] Pocket020
  BaseFeature = -> Pad015
  Direction = (0,1,-2e-16)
  Length = 3
  Length2 = 5
  Placement = pos=(0,0,0) rot=(1,1,1;2.0944rad)
  Profile = -> Sketch033
  ReferenceAxis = -> Sketch033 [N_Axis]
  Suppressed = false
  Type = 0
FEATURE [PartDesign::LinearPattern] LinearPattern002
  BaseFeature = -> Pocket020
  Direction = -> Sketch033 [V_Axis]
  Length = 30
  Mode = 0
  Occurrences = 4
  Offset = 10
  Originals = -> [Pocket020]
  Placement = pos=(0,0,0) rot=(1,1,1;2.0944rad)
  Suppressed = false
  TransformMode = 0
FEATURE [PartDesign::Pocket] Pocket021
  BaseFeature = -> LinearPattern002
  Direction = (0,1,-2e-16)
  Length = 8
  Length2 = 5
  Placement = pos=(0,0,0) rot=(1,1,1;2.0944rad)
  Profile = -> Sketch033 [Edge5]
  ReferenceAxis = -> Sketch033 [N_Axis]
  Suppressed = false
  Type = 0
FEATURE [PartDesign::LinearPattern] LinearPattern003
  BaseFeature = -> Pocket021
  Direction = -> Sketch033 [V_Axis]
  Length = 30
  Mode = 0
  Occurrences = 4
  Offset = 10
  Originals = -> [Pocket021]
  Placement = pos=(0,0,0) rot=(1,1,1;2.0944rad)
  Suppressed = false
  TransformMode = 0
FEATURE [Sketcher::SketchObject] Sketch034
  ArcFitTolerance = 1e-06
  AttachmentOffset = pos=(0,0,-2) rot=(0,0,1;0rad)
  AttachmentSupport = -> [XZ_Plane013]
  FullyConstrained = true
  MakeInternals = false
  MapMode = 5
  Placement = pos=(0,2,-4e-16) rot=(1,0,0;1.5708rad)
  sketch-geometry (1):
    g0: Circle CenterX=-1.5 CenterY=22.5 CenterZ=0 NormalX=0 NormalY=0 NormalZ=1 AngleXU=0 Radius=0.75
  constraints (3):
    c: Diameter(g0) = 1.5
    c: Distance(g0,g-2) = 1.5
    c: DistanceY(g-1,g0) = 22.5
FEATURE [Sketcher::SketchObject] Sketch038
  ArcFitTolerance = 1e-06
  AttachmentOffset = pos=(0,0,22.5) rot=(0,0,1;0rad)
  AttachmentSupport = -> [XY_Plane013]
  ExternalGeometry = -> [LinearPattern003]
  FullyConstrained = true
  MakeInternals = false
  MapMode = 5
  Placement = pos=(0,0,22.5) rot=(0,0,1;0rad)
  sketch-geometry (8):
    g0: LineSegment StartX=-3.5 StartY=2 StartZ=0 EndX=-0.5 EndY=5 EndZ=0
    g1: LineSegment StartX=-0.5 StartY=5 StartZ=0 EndX=0.5 EndY=5 EndZ=0
    g2: LineSegment StartX=0.5 StartY=5 StartZ=0 EndX=3.5 EndY=2 EndZ=0
    g3: LineSegment StartX=2 StartY=2 StartZ=0 EndX=0.5 EndY=3.5 EndZ=0
    g4: LineSegment StartX=0.5 StartY=3.5 StartZ=0 EndX=-0.5 EndY=3.5 EndZ=0
    g5: LineSegment StartX=-0.5 StartY=3.5 StartZ=0 EndX=-2 EndY=2 EndZ=0
    g6: LineSegment StartX=-3.5 StartY=2 StartZ=0 EndX=-2 EndY=2 EndZ=0
    g7: LineSegment StartX=2 StartY=2 StartZ=0 EndX=3.5 EndY=2 EndZ=0
  constraints (22):
    c: PointOnObject(g0,g-3)
    c: Coincident(g1,g0)
    c: Coincident(g2,g1)
    c: PointOnObject(g2,g-3)
    c: PointOnObject(g3,g-3)
    c: Coincident(g4,g3)
    c: Coincident(g5,g4)
    c: Coincident(g6,g0)
    c: PointOnObject(g6,g5)
    c: Horizontal(g6)
    c: Coincident(g7,g3)
    c: Coincident(g7,g2)
    c: Symmetric(g4,g3,g-2)
    c: Symmetric(g0,g1,g-2)
    c: Symmetric(g5,g3,g-2)
    c: Parallel(g0,g5)
    c: Parallel(g3,g2)
    c: Vertical(g0,g4)
    c: Distance(g0,g4) = 1.5
    c: Distance(g6,g6) = 1.5
    c: Distance(g4,g-3) = 1.5
    c: Distance(g4,g4) = 1
FEATURE [PartDesign::Pad] Pad016
  BaseFeature = -> LinearPattern003
  Direction = (0,0,1)
  Length = 2
  Length2 = 10
  Midplane = true
  Placement = pos=(0,0,0) rot=(1,1,1;2.0944rad)
  Profile = -> Sketch038
  ReferenceAxis = -> Sketch038 [N_Axis]
  Suppressed = false
  Type = 0
FEATURE [PartDesign::Body] Body007  label="ressort_d001"
  AllowCompound = false
  Group = -> [Sketch030,Pad013,Sketch031,Pocket019,Pad015,Sketch033,Pocket020,LinearPattern002,Pocket021,LinearPattern003,Sketch034,Sketch038,Pad016]
  Origin = -> Origin013
  Placement = pos=(0,0.2,0) rot=(0,0,1;0rad)
  Tip = -> Pad016
FEATURE [App::Part] Part006  label="ressort001"
  Group = -> [Body007,Link004]
  Origin = -> Origin015
  Placement = pos=(50,-107.2,50) rot=(0,1,0;3.14159rad)
FEATURE [Mesh::Feature] open_tin_can001  label="open_tin_can003"
  Placement = pos=(50,-145,0) rot=(-1,0,0;1.5708rad)
FEATURE [Sketcher::SketchObject] Sketch039
  ArcFitTolerance = 1e-06
  AttachmentSupport = -> [XZ_Plane016]
  FullyConstrained = true
  MakeInternals = false
  MapMode = 5
  Placement = pos=(0,0,0) rot=(1,0,0;1.5708rad)
  expr: Constraints[8] = 20.3 mm / 2
  sketch-geometry (10):
    g0: LineSegment StartX=0 StartY=-10.65 StartZ=0 EndX=10.15 EndY=-10.65 EndZ=0
    g1: LineSegment StartX=10.15 StartY=-10.65 StartZ=0 EndX=10.15 EndY=29.65 EndZ=0
    g2: LineSegment StartX=10.15 StartY=29.65 StartZ=0 EndX=0 EndY=29.65 EndZ=0
    g3: GeomPoint X=0 Y=9.5 Z=0
    g4: LineSegment StartX=0 StartY=39.65 StartZ=0 EndX=0 EndY=29.65 EndZ=0
    g5: LineSegment StartX=0 StartY=-23.65 StartZ=0 EndX=42 EndY=-23.65 EndZ=0
    g6: LineSegment StartX=42 StartY=-3.65 StartZ=0 EndX=20 EndY=39.65 EndZ=0
    g7: LineSegment StartX=20 StartY=39.65 StartZ=0 EndX=0 EndY=39.65 EndZ=0
    g8: LineSegment StartX=0 StartY=-10.65 StartZ=0 EndX=0 EndY=-23.65 EndZ=0
    g9: LineSegment StartX=42 StartY=-3.65 StartZ=0 EndX=42 EndY=-23.65 EndZ=0
  constraints (28):
    c: Coincident(g0,g1)
    c: Coincident(g1,g2)
    c: Vertical(g1)
    c: Horizontal(g0)
    c: PointOnObject(g3,g-2)
    c: Horizontal(g2)
    c: DistanceY(g-1,g3) = 9.5
    c: DistanceY(g1,g1) = 40.3
    c: DistanceX(g2,g2) = 10.15
    c: Coincident(g6,g7)
    c: Coincident(g7,g4)
    c: Vertical(g4)
    c: Horizontal(g5)
    c: Horizontal(g7)
    c: Symmetric(g2,g0,g3)
    c: Coincident(g4,g2)
    c: Coincident(g8,g0)
    c: Coincident(g8,g5)
    c: PointOnObject(g4,g-2)
    c: Vertical(g8)
    c: DistanceY(g8,g8) = 13
    c: DistanceY(g4,g4) = 10
    c: Distance(g5,g5) = 42
    c: DistanceX(g7,g7) = 20
    c: Coincident(g9,g6)
    c: Coincident(g9,g5)
    c: Vertical(g9)
    c: DistanceY(g9,g9) = 20
FEATURE [PartDesign::Pad] Pad017
  Direction = (0,-1,2e-16)
  Length = 3
  Length2 = 10
  Placement = pos=(0,0,0) rot=(1,0,0;1.5708rad)
  Profile = -> Sketch039
  ReferenceAxis = -> Sketch039 [N_Axis]
  Suppressed = false
  Type = 0
FEATURE [Sketcher::SketchObject] Sketch040
  ArcFitTolerance = 1e-06
  AttachmentSupport = -> [XY_Plane011]
  ExternalGeometry = -> [Pocket018]
  FullyConstrained = true
  MakeInternals = false
  MapMode = 5
  sketch-geometry (6):
    g0: LineSegment StartX=-10.7202 StartY=5.36834 StartZ=0 EndX=-36.3018 EndY=-44.5439 EndZ=0
    g1: ArcOfCircle CenterX=-35.4119 CenterY=-45 CenterZ=0 NormalX=0 NormalY=0 NormalZ=1 AngleXU=0 Radius=1 StartAngle=2.66797 EndAngle=5.8242
    g2: ArcOfCircle CenterX=0 CenterY=-62.5 CenterZ=0 NormalX=0 NormalY=0 NormalZ=1 AngleXU=0 Radius=38.5 StartAngle=1.82549 EndAngle=2.68261
    g3: LineSegment StartX=-9.7 StartY=-25.242 StartZ=0 EndX=-9.7 EndY=5.12214 EndZ=0
    g4: ArcOfCircle CenterX=-10.2398 CenterY=5.12214 CenterZ=0 NormalX=0 NormalY=0 NormalZ=1 AngleXU=0 Radius=0.539788 StartAngle=-5.51e-14 EndAngle=2.66797
    g5: LineSegment [constr] StartX=-12.5 StartY=6.28057 StartZ=0 EndX=-10.7202 EndY=5.36834 EndZ=0
  constraints (14):
    c: Tangent(g0,g1) = -1.5708
    c: Tangent(g1,g2) = 1.5708
    c: Coincident(g2,g3)
    c: Parallel(g0,g-3)
    c: Vertical(g3)
    c: Distance(g-7,g3) = 2
    c: Distance(g0,g-3) = 2
    c: Coincident(g1,g-6)
    c: Coincident(g2,g-4)
    c: Tangent(g4,g0) = -1.5708
    c: Tangent(g4,g3) = -1.5708
    c: Coincident(g5,g-5)
    c: Coincident(g5,g0)
    c: Perpendicular(g-3,g5)
FEATURE [PartDesign::Pocket] Pocket022
  BaseFeature = -> Pocket018
  Direction = (0,0,-1)
  Length = 5
  Length2 = 5
  Profile = -> Sketch040
  ReferenceAxis = -> Sketch040 [N_Axis]
  Reversed = true
  Suppressed = false
  Type = 1
FEATURE [Sketcher::SketchObject] Sketch041
  ArcFitTolerance = 1e-06
  AttachmentOffset = pos=(0,0,32) rot=(0,0,1;0rad)
  AttachmentSupport = -> [YZ_Plane016]
  FullyConstrained = true
  MakeInternals = false
  MapMode = 5
  Placement = pos=(32,0,0) rot=(0.57735,0.57735,0.57735;2.0944rad)
  sketch-geometry (4):
    g0: LineSegment StartX=-3 StartY=-23.65 StartZ=0 EndX=-18 EndY=-23.65 EndZ=0
    g1: LineSegment StartX=-18 StartY=-23.65 StartZ=0 EndX=-18 EndY=-21.65 EndZ=0
    g2: ArcOfCircle CenterX=-18 CenterY=-6.65 CenterZ=0 NormalX=0 NormalY=0 NormalZ=1 AngleXU=0 Radius=15 StartAngle=4.71239 EndAngle=6.28319
    g3: LineSegment StartX=-3 StartY=-6.64997 StartZ=0 EndX=-3 EndY=-23.65 EndZ=0
  constraints (11):
    c: Horizontal(g0)
    c: Coincident(g0,g1)
    c: Vertical(g1)
    c: Perpendicular(g1,g2) = 4.71239
    c: Coincident(g2,g3)
    c: Coincident(g3,g0)
    c: Vertical(g3)
    c: DistanceY(g1,g1) = 2
    c: Coincident(g0,g-3)
    c: DistanceX(g0,g0) = 15
    c: Radius(g2) = 15
FEATURE [PartDesign::Pad] Pad018
  BaseFeature = -> Pad017
  Direction = (1,0,0)
  Length = 10
  Length2 = 10
  Placement = pos=(0,0,0) rot=(1,0,0;1.5708rad)
  Profile = -> Sketch041
  ReferenceAxis = -> Sketch041 [N_Axis]
  Suppressed = false
  Type = 0
FEATURE [Sketcher::SketchObject] Sketch042
  ArcFitTolerance = 1e-06
  AttachmentOffset = pos=(0,0,-10) rot=(0,0,1;0rad)
  AttachmentSupport = -> [XY_Plane016]
  ExternalGeometry = -> [Pad018]
  FullyConstrained = true
  MakeInternals = false
  MapMode = 5
  Placement = pos=(0,0,-10) rot=(0,0,1;0rad)
  sketch-geometry (3):
    g0: Circle CenterX=37 CenterY=-12.7 CenterZ=0 NormalX=0 NormalY=0 NormalZ=1 AngleXU=0 Radius=3
    g1: Circle CenterX=37 CenterY=-12.7 CenterZ=0 NormalX=0 NormalY=0 NormalZ=1 AngleXU=0 Radius=1.75
    g2: LineSegment [constr] StartX=37 StartY=-12.7 StartZ=0 EndX=37 EndY=-18 EndZ=0
  constraints (7):
    c: Coincident(g1,g0)
    c: Diameter(g1) = 3.5
    c: Diameter(g0) = 6
    c: Coincident(g2,g0)
    c: Symmetric(g-3,g-3,g2)
    c: Vertical(g2)
    c: DistanceY(g2,g2) = 5.3
FEATURE [PartDesign::Pocket] Pocket023
  BaseFeature = -> Pad018
  Direction = (0,0,-1)
  Length = 5
  Length2 = 5
  Placement = pos=(0,0,0) rot=(1,0,0;1.5708rad)
  Profile = -> Sketch042 [Edge2]
  ReferenceAxis = -> Sketch042 [N_Axis]
  Suppressed = false
  Type = 1
FEATURE [PartDesign::Pocket] Pocket024
  BaseFeature = -> Pocket023
  Direction = (0,0,-1)
  Length = 11.5
  Length2 = 5
  Placement = pos=(0,0,0) rot=(1,0,0;1.5708rad)
  Profile = -> Sketch042 [Edge1]
  ReferenceAxis = -> Sketch042 [N_Axis]
  Suppressed = false
  Type = 0
FEATURE [PartDesign::Body] Body009  label="support_devidoire"
  AllowCompound = false
  Group = -> [Sketch039,Pad017,Sketch041,Pad018,Sketch042,Pocket023,Pocket024]
  Origin = -> Origin016
  Placement = pos=(0,41.5,0) rot=(0,0,1;0rad)
  Tip = -> Pocket024
FEATURE [App::Part] Part003  label="CanMover_Enrouleur"
  Group = -> [Part002,Body004,Body005,Body009]
  Origin = -> Origin007
  Placement = pos=(0,-55,41.5) rot=(0,0.707107,-0.707107;3.14159rad)
FEATURE [Sketcher::SketchObject] Sketch044
  ArcFitTolerance = 1e-06
  FullyConstrained = true
  MakeInternals = false
  MapMode = 5
  Placement = pos=(0,9,0) rot=(0,0.707107,0.707107;3.14159rad)
  sketch-geometry (8):
    g0: LineSegment StartX=-4.625 StartY=5 StartZ=0 EndX=-2.96 EndY=7.22 EndZ=0
    g1: LineSegment StartX=2.96 StartY=7.22 StartZ=0 EndX=4.625 EndY=5 EndZ=0
    g2: LineSegment StartX=4.625 StartY=5 StartZ=0 EndX=3.125 EndY=5 EndZ=0
    g3: LineSegment StartX=3.125 StartY=5 StartZ=0 EndX=2 EndY=6.5 EndZ=0
    g4: LineSegment StartX=-2 StartY=6.5 StartZ=0 EndX=-3.125 EndY=5 EndZ=0
    g5: LineSegment StartX=-3.125 StartY=5 StartZ=0 EndX=-4.625 EndY=5 EndZ=0
    g6: ArcOfCircle CenterX=2e-16 CenterY=5 CenterZ=0 NormalX=0 NormalY=0 NormalZ=1 AngleXU=0 Radius=2.5 StartAngle=0.643501 EndAngle=2.49809
    g7: ArcOfCircle CenterX=-3e-16 CenterY=5 CenterZ=0 NormalX=0 NormalY=0 NormalZ=1 AngleXU=0 Radius=3.7 StartAngle=0.643501 EndAngle=2.49809
  constraints (22):
    c: PointOnObject(g0,g-3)
    c: PointOnObject(g1,g-3)
    c: Coincident(g1,g2)
    c: PointOnObject(g2,g-3)
    c: Coincident(g2,g3)
    c: PointOnObject(g4,g-3)
    c: Coincident(g4,g5)
    c: Coincident(g5,g0)
    c: Symmetric(g4,g3,g-2)
    c: Equal(g4,g3)
    c: Equal(g0,g1)
    c: Symmetric(g1,g0,g-2)
    c: Distance(g3,g-3) = 1.5
    c: Coincident(g6,g3)
    c: Tangent(g6,g4) = -1.5708
    c: Tangent(g0,g7) = 1.5708
    c: Coincident(g1,g7)
    c: DistanceX(g5,g5) = 1.5
    c: PointOnObject(g7,g-3)
    c: Coincident(g6,g7)
    c: Parallel(g3,g1)
    c: Distance(g3,g1) = 1.2
FEATURE [Sketcher::SketchObject] Sketch045
  ArcFitTolerance = 1e-06
  FullyConstrained = true
  MakeInternals = false
  MapMode = 5
  Placement = pos=(0,0,5) rot=(0,0,1;0rad)
  sketch-geometry (1):
    g0: Circle CenterX=0 CenterY=7 CenterZ=0 NormalX=0 NormalY=0 NormalZ=1 AngleXU=0 Radius=1
  constraints (3):
    c: Diameter(g0) = 2
    c: PointOnObject(g0,g-2)
    c: Distance(g0,g-3) = 2
FEATURE [PartDesign::Groove] Groove002
  Angle = 360
  Angle2 = 60
  Axis = (-1,0,0)
  Base = (4.0252,9,5)
  BaseFeature = -> Pocket022
  Profile = -> Sketch045
  Reversed = true
  Suppressed = false
  Type = 0
FEATURE [Sketcher::SketchObject] Sketch046
  ArcFitTolerance = 1e-06
  AttachmentSupport = -> [Groove002]
  ExternalGeometry = -> [Groove002]
  FullyConstrained = true
  MakeInternals = false
  MapMode = 5
  Placement = pos=(0,6.0798,0) rot=(0,0.707107,0.707107;3.14159rad)
  sketch-geometry (6):
    g0: LineSegment StartX=6e-16 StartY=31.5 StartZ=0 EndX=6.2 EndY=31.5 EndZ=0
    g1: LineSegment StartX=6.2 StartY=31.5 StartZ=0 EndX=6.2 EndY=17.3 EndZ=0
    g2: LineSegment StartX=6.2 StartY=17.3 StartZ=0 EndX=0 EndY=23.5 EndZ=0
    g3: LineSegment StartX=6e-16 StartY=31.5 StartZ=0 EndX=6e-16 EndY=29.5 EndZ=0
    g4: LineSegment StartX=-4e-16 StartY=25.5 StartZ=0 EndX=0 EndY=23.5 EndZ=0
    g5: ArcOfCircle CenterX=0 CenterY=27.5 CenterZ=0 NormalX=0 NormalY=0 NormalZ=1 AngleXU=0 Radius=2 StartAngle=4.71239 EndAngle=7.85398
  constraints (19):
    c: PointOnObject(g0,g-2)
    c: PointOnObject(g0,g-3)
    c: Horizontal(g0)
    c: Coincident(g0,g1)
    c: PointOnObject(g1,g-3)
    c: Coincident(g1,g2)
    c: PointOnObject(g2,g-2)
    c: PointOnObject(g4,g-2)
    c: Coincident(g3,g0)
    c: Vertical(g3)
    c: Coincident(g4,g2)
    c: PointOnObject(g5,g-2)
    c: Coincident(g5,g3)
    c: Coincident(g5,g4)
    c: Equal(g3,g4)
    c: Angle(g1,g2) = 0.785398
    c: DistanceY(g-1,g5) = 27.5
    c: Radius(g5) = 2
    c: DistanceY(g3,g3) = 2
FEATURE [PartDesign::Pad] Pad019
  BaseFeature = -> Groove002
  Direction = (0,1,-2e-16)
  Length = 1.5
  Length2 = 10
  Profile = -> Sketch046
  ReferenceAxis = -> Sketch046 [N_Axis]
  Reversed = true
  Suppressed = false
  Type = 0
FEATURE [App::Link] Link006  label="OuterCanMover_G"
  LinkTransform = true
  LinkedObject = -> Part
  ScaleVector = (-1,1,1)
FEATURE [App::Link] Link007  label="InnerCanMover_G"
  LinkTransform = true
  LinkedObject = -> Part005
  ScaleVector = (-1,1,1)
FEATURE [Sketcher::SketchObject] Sketch047
  ArcFitTolerance = 1e-06
  AttachmentSupport = -> [XY_Plane011]
  ExternalGeometry = -> [Pad019]
  FullyConstrained = true
  MakeInternals = false
  MapMode = 5
  sketch-geometry (5):
    g0: ArcOfCircle CenterX=-25.585 CenterY=0 CenterZ=0 NormalX=0 NormalY=0 NormalZ=1 AngleXU=0 Radius=4.5 StartAngle=1.09717 EndAngle=4.23877
    g1: Circle CenterX=-25.585 CenterY=0 CenterZ=0 NormalX=0 NormalY=0 NormalZ=1 AngleXU=0 Radius=1.75
    g2: LineSegment StartX=-27.6375 StartY=-4.00465 StartZ=0 EndX=-19.824 EndY=-8.00929 EndZ=0
    g3: LineSegment StartX=-19.824 StartY=-8.00929 StartZ=0 EndX=-15.719 EndY=0 EndZ=0
    g4: LineSegment StartX=-15.719 StartY=0 StartZ=0 EndX=-23.5324 EndY=4.00465 EndZ=0
  constraints (13):
    c: Coincident(g0,g1)
    c: Tangent(g0,g2) = -1.5708
    c: Coincident(g2,g3)
    c: PointOnObject(g3,g-3)
    c: Coincident(g3,g4)
    c: Tangent(g4,g0) = -1.5708
    c: Equal(g2,g4)
    c: PointOnObject(g2,g-3)
    c: Perpendicular(g3,g2)
    c: Diameter(g1) = 3.5
    c: Radius(g0) = 4.5
    c: PointOnObject(g0,g-1)
    c: PointOnObject(g3,g-1)
FEATURE [PartDesign::Pad] Pad020
  BaseFeature = -> Pad019
  Direction = (0,0,1)
  Length = 5
  Length2 = 10
  Profile = -> Sketch047
  ReferenceAxis = -> Sketch047 [N_Axis]
  Suppressed = false
  Type = 0
FEATURE [PartDesign::Fillet] Fillet004
  Base = -> Pad020 [Edge72]
  BaseFeature = -> Pad020
  Radius = 5
  SupportTransform = false
  Suppressed = false
  UseAllEdges = false
FEATURE [PartDesign::Mirrored] Mirrored001
  BaseFeature = -> Fillet004
  MirrorPlane = -> Sketch040 [V_Axis]
  Originals = -> [Pocket022,Pad019,Pad020,Fillet004]
  Suppressed = false
  TransformMode = 0
FEATURE [PartDesign::Body] Body006  label="Partie_fixe_d001"
  AllowCompound = false
  Group = -> [Sketch028,Pad012,Sketch029,Pocket018,Sketch040,Pocket022,Sketch044,Sketch045,Groove002,Sketch046,Pad019,Sketch047,Pad020,Fillet004,Mirrored001]
  Origin = -> Origin011
  Placement = pos=(50,-82.5,0) rot=(0,0,1;0rad)
  Tip = -> Mirrored001
FEATURE [App::Part] Part005  label="InnerCanMover_D"
  Group = -> [open_tin_can001,Body006,Part006]
  Origin = -> Origin012
  Placement = pos=(0,0,2) rot=(0,0,1;0rad)
FEATURE [Part::Feature] Part__Feature003  label="Lever 25T001"
  Placement = pos=(0,0,0) rot=(-1,0,0;1.5708rad)
  shape: bbox 18.84 x 33.03 x 6.019 mm, 125 faces (baked)
FEATURE [Part::Feature] Part__Feature004  label="Axis Servo001"
  Placement = pos=(0,0,0) rot=(-1,0,0;1.5708rad)
  shape: bbox 5 x 5 x 8 mm, 5 faces (baked)
FEATURE [Part::Feature] Part__Feature005  label="Servo DS3218MG001"
  Placement = pos=(0,0,0) rot=(-1,0,0;1.5708rad)
  shape: bbox 55 x 20 x 41 mm, 772 faces (baked)
FEATURE [Part::FeaturePython] Screw004  label="M2x5-Vis001"  # WARN: FeaturePython — macro-defined, semantics opaque (R4)
  BaseObject = -> Body010 [Edge6]
  Diameter = 2
  Invert = true
  LeftHanded = false
  Length = 10
  LengthCustom = 5
  MatchOuter = false
  OffsetAngle = 0
  Placement = pos=(0,1e-15,4.8) rot=(0,0,1;0rad)
  Thread = false
  Type = 76
FEATURE [Sketcher::SketchObject] Sketch048
  ArcFitTolerance = 0
  AttachmentSupport = -> [XZ_Plane018]
  FullyConstrained = true
  MakeInternals = false
  MapMode = 5
  Placement = pos=(0,0,0) rot=(1,0,0;1.5708rad)
  expr: Constraints[19] = 19.8 / 2
  sketch-geometry (8):
    g0: LineSegment StartX=2.5 StartY=3.4 StartZ=0 EndX=2.5 EndY=0 EndZ=0
    g1: LineSegment StartX=2.5 StartY=0 StartZ=0 EndX=4.2 EndY=0 EndZ=0
    g2: LineSegment StartX=4.2 StartY=0 StartZ=0 EndX=4.2 EndY=2 EndZ=0
    g3: LineSegment StartX=4.2 StartY=2 StartZ=0 EndX=9.9 EndY=2 EndZ=0
    g4: LineSegment StartX=9.9 StartY=2 StartZ=0 EndX=9.9 EndY=4.4 EndZ=0
    g5: LineSegment StartX=9.9 StartY=4.4 StartZ=0 EndX=1.5 EndY=4.4 EndZ=0
    g6: LineSegment StartX=1.5 StartY=4.4 StartZ=0 EndX=1.5 EndY=3.4 EndZ=0
    g7: LineSegment StartX=1.5 StartY=3.4 StartZ=0 EndX=2.5 EndY=3.4 EndZ=0
  constraints (24):
    c: PointOnObject(g0,g-1)
    c: Vertical(g0)
    c: Coincident(g1,g0)
    c: PointOnObject(g1,g-1)
    c: Coincident(g2,g1)
    c: Vertical(g2)
    c: Coincident(g3,g2)
    c: Horizontal(g3)
    c: Coincident(g4,g3)
    c: Vertical(g4)
    c: Coincident(g5,g4)
    c: Horizontal(g5)
    c: Coincident(g6,g5)
    c: Coincident(g7,g6)
    c: Coincident(g7,g0)
    c: Horizontal(g7)
    c: Vertical(g6)
    c: DistanceY(g4,g4) = 2.4
    c: DistanceY(g2,g2) = 2
    c: DistanceX(g-1,g4) = 9.9
    c: DistanceX(g-1,g6) = 1.5
    c: DistanceY(g0,g0) = 3.4
    c: DistanceX(g-1,g0) = 2.5
    c: DistanceX(g1,g1) = 1.7
FEATURE [PartDesign::Revolution] Revolution001
  Angle = 360
  Angle2 = 60
  Axis = (0,2e-16,1)
  Base = (0,0,0)
  Placement = pos=(0,0,0) rot=(1,0,0;1.5708rad)
  Profile = -> Sketch048
  ReferenceAxis = -> Sketch048 [V_Axis]
  Reversed = true
  Suppressed = false
  Type = 0
FEATURE [Sketcher::SketchObject] Sketch049
  ArcFitTolerance = 0
  AttachmentSupport = -> [XY_Plane018]
  FullyConstrained = true
  MakeInternals = false
  MapMode = 5
  sketch-geometry (1):
    g0: Circle CenterX=-7 CenterY=0 CenterZ=0 NormalX=0 NormalY=0 NormalZ=1 AngleXU=0 Radius=1.2
  constraints (3):
    c: PointOnObject(g0,g-1)
    c: Diameter(g0) = 2.4
    c: DistanceX(g0,g-1) = 7
FEATURE [PartDesign::Pocket] Pocket025
  BaseFeature = -> Revolution001
  Direction = (0,0,-1)
  Length = 5
  Length2 = 5
  Midplane = true
  Placement = pos=(0,0,0) rot=(1,0,0;1.5708rad)
  Profile = -> Sketch049
  ReferenceAxis = -> Sketch049 [N_Axis]
  Suppressed = false
  Type = 1
FEATURE [PartDesign::PolarPattern] PolarPattern003
  Angle = 360
  Axis = -> Sketch049 [N_Axis]
  BaseFeature = -> Pocket025
  Mode = 0
  Occurrences = 4
  Offset = 120
  Originals = -> [Pocket025]
  Placement = pos=(0,0,0) rot=(1,0,0;1.5708rad)
  Suppressed = false
  TransformMode = 0
FEATURE [PartDesign::Body] Body010  label="Corps001"
  AllowCompound = false
  Group = -> [Sketch048,Revolution001,Sketch049,Pocket025,PolarPattern003]
  Origin = -> Origin018
  Placement = pos=(0,0,0.4) rot=(0,0,1;0rad)
  Tip = -> PolarPattern003
FEATURE [App::Part] Part007  label="servo_DS3218MG001"
  Group = -> [Part__Feature003,Part__Feature004,Part__Feature005,Body010,Screw004]
  Origin = -> Origin017
FEATURE [Sketcher::SketchObject] Sketch050
  ArcFitTolerance = 1e-06
  AttachmentSupport = -> [XZ_Plane020]
  FullyConstrained = true
  MakeInternals = false
  MapMode = 5
  Placement = pos=(0,0,0) rot=(1,0,0;1.5708rad)
  expr: Constraints[2] = 5.5
  expr: Constraints[5] = 3.4
  sketch-geometry (6):
    g0: Circle CenterX=0 CenterY=0 CenterZ=0 NormalX=0 NormalY=0 NormalZ=1 AngleXU=0 Radius=15
    g1: Circle CenterX=0 CenterY=0 CenterZ=0 NormalX=0 NormalY=0 NormalZ=1 AngleXU=0 Radius=2.75
    g2: Circle CenterX=0 CenterY=7 CenterZ=0 NormalX=0 NormalY=0 NormalZ=1 AngleXU=0 Radius=1.7
    g3: Circle CenterX=-7 CenterY=0 CenterZ=0 NormalX=0 NormalY=0 NormalZ=1 AngleXU=0 Radius=1.7
    g4: Circle CenterX=0 CenterY=-7 CenterZ=0 NormalX=0 NormalY=0 NormalZ=1 AngleXU=0 Radius=1.7
    g5: Circle CenterX=7 CenterY=0 CenterZ=0 NormalX=0 NormalY=0 NormalZ=1 AngleXU=0 Radius=1.7
  constraints (14):
    c: Diameter(g0) = 30
    c: Coincident(g0,g-1)
    c: Diameter(g1) = 5.5
    c: Coincident(g1,g0)
    c: PointOnObject(g2,g-2)
    c: Diameter(g2) = 3.4
    c: DistanceY(g-1,g2) = 7
    c: PointOnObject(g3,g-1)
    c: Symmetric(g5,g3,g0)
    c: Symmetric(g2,g4,g0)
    c: DistanceX(g3,g-1) = 7
    c: Equal(g5,g4)
    c: Equal(g4,g3)
    c: Equal(g3,g2)
FEATURE [PartDesign::Pad] Pad021
  Direction = (0,-1,2e-16)
  Length = 5
  Length2 = 10
  Placement = pos=(0,0,0) rot=(1,0,0;1.5708rad)
  Profile = -> Sketch050
  ReferenceAxis = -> Sketch050 [N_Axis]
  Suppressed = false
  Type = 0
FEATURE [Sketcher::SketchObject] Sketch051
  ArcFitTolerance = 1e-06
  AttachmentOffset = pos=(0,0,2) rot=(0,0,1;0rad)
  AttachmentSupport = -> [XZ_Plane020]
  FullyConstrained = true
  MakeInternals = false
  MapMode = 5
  Placement = pos=(0,-2,4e-16) rot=(1,0,0;1.5708rad)
  expr: Constraints[1] = 2.7 * 2
  sketch-geometry (1):
    g0: Circle CenterX=0 CenterY=7 CenterZ=0 NormalX=0 NormalY=0 NormalZ=1 AngleXU=0 Radius=2.7
  constraints (3):
    c: PointOnObject(g0,g-2)
    c: Diameter(g0) = 5.4
    c: DistanceY(g-1,g0) = 7
FEATURE [PartDesign::Pocket] Pocket026
  BaseFeature = -> Pad021
  Direction = (0,1,-2e-16)
  Length = 1
  Length2 = 5
  Placement = pos=(0,0,0) rot=(1,0,0;1.5708rad)
  Profile = -> Sketch051
  ReferenceAxis = -> Sketch051 [N_Axis]
  Reversed = true
  Suppressed = false
  Type = 1
FEATURE [PartDesign::PolarPattern] PolarPattern004
  Angle = 360
  Axis = -> Sketch051 [N_Axis]
  BaseFeature = -> Pocket026
  Mode = 0
  Occurrences = 4
  Offset = 120
  Originals = -> [Pocket026]
  Placement = pos=(0,0,0) rot=(1,0,0;1.5708rad)
  Suppressed = false
  TransformMode = 0
FEATURE [Sketcher::SketchObject] Sketch052
  ArcFitTolerance = 1e-06
  AttachmentSupport = -> [YZ_Plane020]
  ExternalGeometry = -> [PolarPattern004]
  FullyConstrained = true
  MakeInternals = false
  MapMode = 5
  Placement = pos=(0,0,0) rot=(0.57735,0.57735,0.57735;2.0944rad)
  sketch-geometry (4):
    g0: ArcOfCircle CenterX=-2.5 CenterY=16 CenterZ=0 NormalX=0 NormalY=0 NormalZ=1 AngleXU=0 Radius=1.80278 StartAngle=3.7296 EndAngle=5.69518
    g1: LineSegment [constr] StartX=-5 StartY=15 StartZ=0 EndX=3.6e-15 EndY=15 EndZ=0
    g2: LineSegment [constr] StartX=-2.5 StartY=16 StartZ=0 EndX=-2.5 EndY=15 EndZ=0
    g3: LineSegment StartX=-4 StartY=15 StartZ=0 EndX=-1 EndY=15 EndZ=0
  constraints (11):
    c: Coincident(g1,g-3)
    c: Coincident(g1,g-4)
    c: PointOnObject(g0,g1)
    c: PointOnObject(g0,g1)
    c: Coincident(g2,g0)
    c: Symmetric(g1,g1,g2)
    c: Vertical(g2)
    c: DistanceY(g2,g2) = 1
    c: Coincident(g3,g0)
    c: Coincident(g3,g0)
    c: Distance(g1,g0) = 1
FEATURE [PartDesign::Groove] Groove003
  Angle = 360
  Angle2 = 60
  Axis = (1e-16,1,-1e-16)
  Base = (0,0,0)
  BaseFeature = -> PolarPattern004
  Placement = pos=(0,0,0) rot=(1,0,0;1.5708rad)
  Profile = -> Sketch052
  ReferenceAxis = -> Y_Axis020
  Reversed = true
  Suppressed = false
  Type = 0
FEATURE [Sketcher::SketchObject] Sketch053
  ArcFitTolerance = 1e-06
  AttachmentSupport = -> [Groove003]
  FullyConstrained = true
  MakeInternals = false
  MapMode = 5
  Placement = pos=(0,-5,0) rot=(1,0,0;1.5708rad)
  sketch-geometry (4):
    g0: ArcOfCircle CenterX=0 CenterY=18 CenterZ=0 NormalX=0 NormalY=0 NormalZ=1 AngleXU=0 Radius=1 StartAngle=0 EndAngle=3.14159
    g1: LineSegment StartX=-1 StartY=18 StartZ=0 EndX=-1 EndY=10 EndZ=0
    g2: LineSegment StartX=-1 StartY=10 StartZ=0 EndX=1 EndY=10 EndZ=0
    g3: LineSegment StartX=1 StartY=10 StartZ=0 EndX=1 EndY=18 EndZ=0
  constraints (11):
    c: PointOnObject(g0,g-2)
    c: Vertical(g1)
    c: Coincident(g2,g1)
    c: Horizontal(g2)
    c: Vertical(g3)
    c: Coincident(g2,g3)
    c: DistanceY(g-1,g0) = 18
    c: Tangent(g1,g0) = -1.5708
    c: Tangent(g3,g0) = -1.5708
    c: Distance(g2,g2) = 2
    c: DistanceY(g-1,g1) = 10
FEATURE [PartDesign::Pad] Pad022
  BaseFeature = -> Groove003
  Direction = (0,-1,2e-16)
  Length = 5
  Length2 = 10
  Placement = pos=(0,0,0) rot=(1,0,0;1.5708rad)
  Profile = -> Sketch053
  ReferenceAxis = -> Sketch053 [N_Axis]
  Reversed = true
  Suppressed = false
  Type = 0
FEATURE [Sketcher::SketchObject] Sketch054
  ArcFitTolerance = 1e-06
  AttachmentSupport = -> [Pad022]
  ExternalGeometry = -> [Pad022]
  FullyConstrained = true
  MakeInternals = false
  MapMode = 5
  Placement = pos=(1,0,0) rot=(0.707107,0,0.707107;3.14159rad)
  sketch-geometry (3):
    g0: GeomPoint X=19 Y=2.5 Z=0
    g1: GeomPoint X=19 Y=0 Z=0
    g2: Circle CenterX=17 CenterY=2.5 CenterZ=0 NormalX=0 NormalY=0 NormalZ=1 AngleXU=0 Radius=0.75
  constraints (6):
    c: PointOnObject(g1,g-1)
    c: Symmetric(g1,g-3,g0)
    c: Horizontal(g2,g0)
    c: DistanceX(g2,g-3) = 2
    c: Diameter(g2) = 1.5
    c: Vertical(g0,g1)
FEATURE [PartDesign::Pocket] Pocket027
  BaseFeature = -> Pad022
  Direction = (-1,0,2e-16)
  Length = 5
  Length2 = 5
  Placement = pos=(0,0,0) rot=(1,0,0;1.5708rad)
  Profile = -> Sketch054
  ReferenceAxis = -> Sketch054 [N_Axis]
  Suppressed = false
  Type = 0
FEATURE [PartDesign::PolarPattern] PolarPattern005
  Angle = 360
  Axis = -> Sketch053 [N_Axis]
  BaseFeature = -> Pocket027
  Mode = 0
  Occurrences = 2
  Offset = 120
  Originals = -> [Pad022,Pocket027]
  Placement = pos=(0,0,0) rot=(1,0,0;1.5708rad)
  Suppressed = false
  TransformMode = 0
FEATURE [PartDesign::Body] Body011  label="devidoire001"
  AllowCompound = false
  Group = -> [Sketch050,Pad021,Sketch051,Pocket026,PolarPattern004,Sketch052,Groove003,Sketch053,Pad022,Sketch054,Pocket027,PolarPattern005]
  Origin = -> Origin020
  Placement = pos=(0,0,2.8) rot=(1,0,0;4.71239rad)
  Tip = -> PolarPattern005
FEATURE [Sketcher::SketchObject] Sketch055
  ArcFitTolerance = 1e-06
  AttachmentSupport = -> [XZ_Plane021]
  FullyConstrained = true
  MakeInternals = false
  MapMode = 5
  Placement = pos=(0,0,0) rot=(1,0,0;1.5708rad)
  sketch-geometry (18):
    g0: LineSegment StartX=-10.15 StartY=29.65 StartZ=0 EndX=-10.15 EndY=-10.65 EndZ=0
    g1: LineSegment [constr] StartX=-10.15 StartY=-10.65 StartZ=0 EndX=10.15 EndY=-10.65 EndZ=0
    g2: LineSegment [constr] StartX=10.15 StartY=-10.65 StartZ=0 EndX=10.15 EndY=29.65 EndZ=0
    g3: LineSegment [constr] StartX=10.15 StartY=29.65 StartZ=0 EndX=-10.15 EndY=29.65 EndZ=0
    g4: LineSegment StartX=-14.85 StartY=37 StartZ=0 EndX=-14.85 EndY=-18 EndZ=0
    g5: LineSegment [constr] StartX=-14.85 StartY=-18 StartZ=0 EndX=14.85 EndY=-18 EndZ=0
    g6: LineSegment [constr] StartX=14.85 StartY=-18 StartZ=0 EndX=14.85 EndY=37 EndZ=0
    g7: LineSegment [constr] StartX=14.85 StartY=37 StartZ=0 EndX=-14.85 EndY=37 EndZ=0
    g8: GeomPoint X=-10.15 Y=9.5 Z=0
    g9: GeomPoint X=-14.85 Y=9.5 Z=0
    g10: LineSegment StartX=-14.85 StartY=37 StartZ=0 EndX=0 EndY=37 EndZ=0
    g11: LineSegment StartX=0 StartY=37 StartZ=0 EndX=0 EndY=29.65 EndZ=0
    g12: LineSegment StartX=0 StartY=29.65 StartZ=0 EndX=-10.15 EndY=29.65 EndZ=0
    g13: LineSegment StartX=-10.15 StartY=-10.65 StartZ=0 EndX=0 EndY=-10.65 EndZ=0
    g14: LineSegment StartX=0 StartY=-18 StartZ=0 EndX=-14.85 EndY=-18 EndZ=0
    g15: Circle CenterX=-6 CenterY=34.45 CenterZ=0 NormalX=0 NormalY=0 NormalZ=1 AngleXU=0 Radius=2.25
    g16: Circle CenterX=-6 CenterY=-15.5 CenterZ=0 NormalX=0 NormalY=0 NormalZ=1 AngleXU=0 Radius=2.25
    g17: LineSegment StartX=0 StartY=-10.65 StartZ=0 EndX=0 EndY=-18 EndZ=0
  constraints (44):
    c: Coincident(g0,g1)
    c: Coincident(g1,g2)
    c: Coincident(g2,g3)
    c: Coincident(g3,g0)
    c: Vertical(g0)
    c: Vertical(g2)
    c: Horizontal(g1)
    c: Coincident(g4,g5)
    c: Coincident(g5,g6)
    c: Coincident(g6,g7)
    c: Coincident(g7,g4)
    c: Vertical(g4)
    c: Vertical(g6)
    c: Horizontal(g5)
    c: DistanceX(g7,g7) = 29.7
    c: Symmetric(g4,g6,g-2)
    c: Symmetric(g0,g2,g-2)
    c: DistanceX(g3,g3) = 20.3
    c: DistanceY(g0,g0) = 40.3
    c: Symmetric(g0,g0,g8)
    c: DistanceY(g-1,g8) = 9.5
    c: Symmetric(g4,g4,g9)
    c: Horizontal(g9,g8)
    c: DistanceY(g4,g4) = 55
    c: Coincident(g10,g4)
    c: PointOnObject(g10,g-2)
    c: Coincident(g11,g10)
    c: PointOnObject(g11,g-2)
    c: Coincident(g12,g11)
    c: Horizontal(g12)
    c: Coincident(g13,g0)
    c: Symmetric(g1,g1,g13)
    c: Symmetric(g5,g5,g14)
    c: Coincident(g14,g4)
    c: Horizontal(g10)
    c: Coincident(g0,g12)
    c: Diameter(g15) = 4.5
    c: DistanceY(g-1,g15) = 34.45
    c: DistanceX(g15,g-1) = 6
    c: Vertical(g16,g15)
    c: Equal(g15,g16)
    c: DistanceY(g16,g-1) = 15.5
    c: Coincident(g17,g13)
    c: Coincident(g17,g14)
FEATURE [PartDesign::Pad] Pad023
  Direction = (0,-1,2e-16)
  Length = 10
  Length2 = 10
  Placement = pos=(0,0,0) rot=(1,0,0;1.5708rad)
  Profile = -> Sketch055
  ReferenceAxis = -> Sketch055 [N_Axis]
  Reversed = true
  Suppressed = false
  Type = 0
FEATURE [Sketcher::SketchObject] Sketch056
  ArcFitTolerance = 1e-06
  AttachmentSupport = -> [Pad023]
  ExternalGeometry = -> [Pad023]
  FullyConstrained = true
  MakeInternals = false
  MapMode = 5
  Placement = pos=(-14.85,0,0) rot=(0.707107,0,-0.707107;3.14159rad)
  sketch-geometry (4):
    g0: LineSegment StartX=4.15 StartY=0 StartZ=0 EndX=4.15 EndY=-4 EndZ=0
    g1: LineSegment StartX=4.15 StartY=-4 StartZ=0 EndX=8.85 EndY=-4 EndZ=0
    g2: LineSegment StartX=8.85 StartY=-4 StartZ=0 EndX=8.85 EndY=0 EndZ=0
    g3: LineSegment StartX=8.85 StartY=0 StartZ=0 EndX=4.15 EndY=0 EndZ=0
  constraints (12):
    c: Coincident(g0,g1)
    c: Coincident(g1,g2)
    c: Coincident(g2,g3)
    c: Coincident(g3,g0)
    c: Vertical(g0)
    c: Vertical(g2)
    c: Horizontal(g1)
    c: Horizontal(g3)
    c: PointOnObject(g0,g-1)
    c: DistanceX(g3,g3) = 4.7
    c: DistanceY(g2,g2) = 4
    c: DistanceX(g2,g-3) = 9.15
FEATURE [PartDesign::Pad] Pad024
  BaseFeature = -> Pad023
  Direction = (-1,0,-2e-16)
  Length = 31
  Length2 = 10
  Placement = pos=(0,0,0) rot=(1,0,0;1.5708rad)
  Profile = -> Sketch056
  ReferenceAxis = -> Sketch056 [N_Axis]
  Suppressed = false
  Type = 0
FEATURE [Sketcher::SketchObject] Sketch057
  ArcFitTolerance = 1e-06
  AttachmentSupport = -> [Pad024]
  ExternalGeometry = -> [Pad024]
  FullyConstrained = true
  MakeInternals = false
  MapMode = 5
  Placement = pos=(0,4,-9e-16) rot=(-1,0,0;1.5708rad)
  sketch-geometry (4):
    g0: LineSegment StartX=-45.85 StartY=8.85 StartZ=0 EndX=-45.85 EndY=4.15 EndZ=0
    g1: LineSegment StartX=-45.85 StartY=4.15 StartZ=0 EndX=-36.15 EndY=4.15 EndZ=0
    g2: LineSegment StartX=-36.15 StartY=4.15 StartZ=0 EndX=-36.15 EndY=8.85 EndZ=0
    g3: LineSegment StartX=-36.15 StartY=8.85 StartZ=0 EndX=-45.85 EndY=8.85 EndZ=0
  constraints (10):
    c: Coincident(g0,g1)
    c: Coincident(g1,g2)
    c: Coincident(g2,g3)
    c: Coincident(g3,g0)
    c: Vertical(g2)
    c: Horizontal(g1)
    c: Horizontal(g3)
    c: Coincident(g0,g-3)
    c: Coincident(g0,g-3)
    c: DistanceX(g3,g3) = 9.7
FEATURE [PartDesign::Pad] Pad025
  BaseFeature = -> Pad024
  Direction = (0,1,2e-16)
  Length = 5
  Length2 = 10
  Placement = pos=(0,0,0) rot=(1,0,0;1.5708rad)
  Profile = -> Sketch057
  ReferenceAxis = -> Sketch057 [N_Axis]
  Suppressed = false
  Type = 0
FEATURE [Sketcher::SketchObject] Sketch058
  ArcFitTolerance = 1e-06
  AttachmentSupport = -> [Pad025]
  ExternalGeometry = -> [Pad025]
  FullyConstrained = true
  MakeInternals = false
  MapMode = 5
  Placement = pos=(0,10,0) rot=(-1,0,0;1.5708rad)
  sketch-geometry (8):
    g0: LineSegment StartX=-14.85 StartY=18 StartZ=0 EndX=-14.85 EndY=10.65 EndZ=0
    g1: LineSegment StartX=-14.85 StartY=10.65 StartZ=0 EndX=0 EndY=10.65 EndZ=0
    g2: LineSegment StartX=0 StartY=10.65 StartZ=0 EndX=0 EndY=18 EndZ=0
    g3: LineSegment StartX=0 StartY=18 StartZ=0 EndX=-14.85 EndY=18 EndZ=0
    g4: LineSegment StartX=-14.85 StartY=-37 StartZ=0 EndX=0 EndY=-37 EndZ=0
    g5: LineSegment StartX=0 StartY=-37 StartZ=0 EndX=0 EndY=-29.65 EndZ=0
    g6: LineSegment StartX=0 StartY=-29.65 StartZ=0 EndX=-14.85 EndY=-29.65 EndZ=0
    g7: LineSegment StartX=-14.85 StartY=-29.65 StartZ=0 EndX=-14.85 EndY=-37 EndZ=0
  constraints (21):
    c: Coincident(g0,g1)
    c: Coincident(g1,g2)
    c: Coincident(g2,g3)
    c: Coincident(g3,g0)
    c: Vertical(g0)
    c: Vertical(g2)
    c: Horizontal(g1)
    c: Horizontal(g3)
    c: Coincident(g0,g-3)
    c: PointOnObject(g1,g-2)
    c: PointOnObject(g-4,g1)
    c: Coincident(g4,g5)
    c: Coincident(g5,g6)
    c: Coincident(g6,g7)
    c: Coincident(g7,g4)
    c: Horizontal(g4)
    c: Horizontal(g6)
    c: Vertical(g5)
    c: Vertical(g7)
    c: Coincident(g4,g-6)
    c: Coincident(g5,g-5)
FEATURE [PartDesign::Pocket] Pocket028
  BaseFeature = -> Pad025
  Direction = (0,-1,-2e-16)
  Length = 7
  Length2 = 5
  Placement = pos=(0,0,0) rot=(1,0,0;1.5708rad)
  Profile = -> Sketch058
  ReferenceAxis = -> Sketch058 [N_Axis]
  Suppressed = false
  Type = 0
FEATURE [PartDesign::Pocket] Pocket029
  BaseFeature = -> Pocket028
  Direction = (0,-2e-16,-1)
  Length = 1
  Length2 = 5
  Placement = pos=(0,0,0) rot=(1,0,0;1.5708rad)
  Profile = -> Pocket028 [Face1]
  Suppressed = false
  Type = 0
FEATURE [PartDesign::Pocket] Pocket030
  BaseFeature = -> Pocket029
  Direction = (0,2e-16,1)
  Length = 1
  Length2 = 5
  Placement = pos=(0,0,0) rot=(1,0,0;1.5708rad)
  Profile = -> Pocket029 [Face4]
  Suppressed = false
  Type = 0
FEATURE [PartDesign::Fillet] Fillet005
  Base = -> Pocket030 [Edge17]
  BaseFeature = -> Pocket030
  Placement = pos=(0,0,0) rot=(1,0,0;1.5708rad)
  Radius = 12
  SupportTransform = false
  Suppressed = false
  UseAllEdges = false
FEATURE [PartDesign::Chamfer] Chamfer002
  Angle = 45
  Base = -> Fillet005 [Edge24]
  BaseFeature = -> Fillet005
  ChamferType = 1
  FlipDirection = false
  Placement = pos=(0,0,0) rot=(1,0,0;1.5708rad)
  Size = 1.7
  Size2 = 10
  SupportTransform = false
  Suppressed = false
  UseAllEdges = false
FEATURE [PartDesign::Mirrored] Mirrored002
  BaseFeature = -> Chamfer002
  MirrorPlane = -> YZ_Plane021
  Placement = pos=(0,0,0) rot=(1,0,0;1.5708rad)
  Suppressed = false
  TransformMode = 1
FEATURE [PartDesign::Body] Body012  label="support_servo001"
  AllowCompound = false
  Group = -> [Sketch055,Pad023,Sketch056,Pad024,Sketch057,Pad025,Sketch058,Pocket028,Pocket029,Pocket030,Fillet005,Chamfer002,Mirrored002]
  Origin = -> Origin021
  Placement = pos=(0,13.9,0) rot=(0,0,1;0rad)
  Tip = -> Mirrored002
FEATURE [Sketcher::SketchObject] Sketch059
  ArcFitTolerance = 1e-06
  AttachmentSupport = -> [XZ_Plane022]
  FullyConstrained = true
  MakeInternals = false
  MapMode = 5
  Placement = pos=(0,0,0) rot=(1,0,0;1.5708rad)
  expr: Constraints[8] = 20.3 mm / 2
  sketch-geometry (10):
    g0: LineSegment StartX=0 StartY=-10.65 StartZ=0 EndX=10.15 EndY=-10.65 EndZ=0
    g1: LineSegment StartX=10.15 StartY=-10.65 StartZ=0 EndX=10.15 EndY=29.65 EndZ=0
    g2: LineSegment StartX=10.15 StartY=29.65 StartZ=0 EndX=0 EndY=29.65 EndZ=0
    g3: GeomPoint X=0 Y=9.5 Z=0
    g4: LineSegment StartX=0 StartY=39.65 StartZ=0 EndX=0 EndY=29.65 EndZ=0
    g5: LineSegment StartX=0 StartY=-23.65 StartZ=0 EndX=42 EndY=-23.65 EndZ=0
    g6: LineSegment StartX=42 StartY=-3.65 StartZ=0 EndX=20 EndY=39.65 EndZ=0
    g7: LineSegment StartX=20 StartY=39.65 StartZ=0 EndX=0 EndY=39.65 EndZ=0
    g8: LineSegment StartX=0 StartY=-10.65 StartZ=0 EndX=0 EndY=-23.65 EndZ=0
    g9: LineSegment StartX=42 StartY=-3.65 StartZ=0 EndX=42 EndY=-23.65 EndZ=0
  constraints (28):
    c: Coincident(g0,g1)
    c: Coincident(g1,g2)
    c: Vertical(g1)
    c: Horizontal(g0)
    c: PointOnObject(g3,g-2)
    c: Horizontal(g2)
    c: DistanceY(g-1,g3) = 9.5
    c: DistanceY(g1,g1) = 40.3
    c: DistanceX(g2,g2) = 10.15
    c: Coincident(g6,g7)
    c: Coincident(g7,g4)
    c: Vertical(g4)
    c: Horizontal(g5)
    c: Horizontal(g7)
    c: Symmetric(g2,g0,g3)
    c: Coincident(g4,g2)
    c: Coincident(g8,g0)
    c: Coincident(g8,g5)
    c: PointOnObject(g4,g-2)
    c: Vertical(g8)
    c: DistanceY(g8,g8) = 13
    c: DistanceY(g4,g4) = 10
    c: Distance(g5,g5) = 42
    c: DistanceX(g7,g7) = 20
    c: Coincident(g9,g6)
    c: Coincident(g9,g5)
    c: Vertical(g9)
    c: DistanceY(g9,g9) = 20
FEATURE [PartDesign::Pad] Pad026
  Direction = (0,-1,2e-16)
  Length = 3
  Length2 = 10
  Placement = pos=(0,0,0) rot=(1,0,0;1.5708rad)
  Profile = -> Sketch059
  ReferenceAxis = -> Sketch059 [N_Axis]
  Suppressed = false
  Type = 0
FEATURE [Sketcher::SketchObject] Sketch060
  ArcFitTolerance = 1e-06
  AttachmentOffset = pos=(0,0,32) rot=(0,0,1;0rad)
  AttachmentSupport = -> [YZ_Plane022]
  FullyConstrained = true
  MakeInternals = false
  MapMode = 5
  Placement = pos=(32,0,0) rot=(0.57735,0.57735,0.57735;2.0944rad)
  sketch-geometry (4):
    g0: LineSegment StartX=-3 StartY=-23.65 StartZ=0 EndX=-18 EndY=-23.65 EndZ=0
    g1: LineSegment StartX=-18 StartY=-23.65 StartZ=0 EndX=-18 EndY=-21.65 EndZ=0
    g2: ArcOfCircle CenterX=-18 CenterY=-6.65 CenterZ=0 NormalX=0 NormalY=0 NormalZ=1 AngleXU=0 Radius=15 StartAngle=4.71239 EndAngle=6.28319
    g3: LineSegment StartX=-3 StartY=-6.64997 StartZ=0 EndX=-3 EndY=-23.65 EndZ=0
  constraints (11):
    c: Horizontal(g0)
    c: Coincident(g0,g1)
    c: Vertical(g1)
    c: Perpendicular(g1,g2) = 4.71239
    c: Coincident(g2,g3)
    c: Coincident(g3,g0)
    c: Vertical(g3)
    c: DistanceY(g1,g1) = 2
    c: Coincident(g0,g-3)
    c: DistanceX(g0,g0) = 15
    c: Radius(g2) = 15
FEATURE [PartDesign::Pad] Pad027
  BaseFeature = -> Pad026
  Direction = (1,0,0)
  Length = 10
  Length2 = 10
  Placement = pos=(0,0,0) rot=(1,0,0;1.5708rad)
  Profile = -> Sketch060
  ReferenceAxis = -> Sketch060 [N_Axis]
  Suppressed = false
  Type = 0
FEATURE [Sketcher::SketchObject] Sketch061
  ArcFitTolerance = 1e-06
  AttachmentOffset = pos=(0,0,-10) rot=(0,0,1;0rad)
  AttachmentSupport = -> [XY_Plane022]
  ExternalGeometry = -> [Pad027]
  FullyConstrained = true
  MakeInternals = false
  MapMode = 5
  Placement = pos=(0,0,-10) rot=(0,0,1;0rad)
  sketch-geometry (3):
    g0: Circle CenterX=37 CenterY=-12.7 CenterZ=0 NormalX=0 NormalY=0 NormalZ=1 AngleXU=0 Radius=3
    g1: Circle CenterX=37 CenterY=-12.7 CenterZ=0 NormalX=0 NormalY=0 NormalZ=1 AngleXU=0 Radius=1.75
    g2: LineSegment [constr] StartX=37 StartY=-12.7 StartZ=0 EndX=37 EndY=-18 EndZ=0
  constraints (7):
    c: Coincident(g1,g0)
    c: Diameter(g1) = 3.5
    c: Diameter(g0) = 6
    c: Coincident(g2,g0)
    c: Symmetric(g-3,g-3,g2)
    c: Vertical(g2)
    c: DistanceY(g2,g2) = 5.3
FEATURE [PartDesign::Pocket] Pocket031
  BaseFeature = -> Pad027
  Direction = (0,0,-1)
  Length = 5
  Length2 = 5
  Placement = pos=(0,0,0) rot=(1,0,0;1.5708rad)
  Profile = -> Sketch061 [Edge2]
  ReferenceAxis = -> Sketch061 [N_Axis]
  Suppressed = false
  Type = 1
FEATURE [PartDesign::Pocket] Pocket032
  BaseFeature = -> Pocket031
  Direction = (0,0,-1)
  Length = 11.5
  Length2 = 5
  Placement = pos=(0,0,0) rot=(1,0,0;1.5708rad)
  Profile = -> Sketch061 [Edge1]
  ReferenceAxis = -> Sketch061 [N_Axis]
  Suppressed = false
  Type = 0
FEATURE [PartDesign::Body] Body013  label="support_devidoire001"
  AllowCompound = false
  Group = -> [Sketch059,Pad026,Sketch060,Pad027,Sketch061,Pocket031,Pocket032]
  Origin = -> Origin022
  Placement = pos=(0,41.5,0) rot=(0,0,1;0rad)
  Tip = -> Pocket032
FEATURE [App::Link] Link008  label="servo_DS3218MG002"
  LinkedObject = -> Part007
FEATURE [Sketcher::SketchObject] Sketch063
  ArcFitTolerance = 1e-06
  AttachmentSupport = -> [XZ_Plane027]
  FullyConstrained = true
  MakeInternals = false
  MapMode = 5
  Placement = pos=(0,0,0) rot=(1,0,0;1.5708rad)
  expr: Constraints[89] = .Constraints.bord + .Constraints.marge
  sketch-geometry (48):
    g0: LineSegment StartX=-7.5 StartY=0 StartZ=0 EndX=-7.5 EndY=5 EndZ=0
    g1: LineSegment StartX=-7.5 StartY=5 StartZ=0 EndX=-4.89997 EndY=5 EndZ=0
    g2: LineSegment StartX=-4.89997 StartY=5 StartZ=0 EndX=-4.5 EndY=4.14226 EndZ=0
    g3: ArcOfCircle CenterX=-4.59063 CenterY=4.1 CenterZ=0 NormalX=0 NormalY=0 NormalZ=1 AngleXU=0 Radius=0.1 StartAngle=4.71239 EndAngle=6.71952
    g4: LineSegment StartX=-4.59063 StartY=4 StartZ=0 EndX=-6.5 EndY=4 EndZ=0
    g5: LineSegment StartX=-6.5 StartY=4 StartZ=0 EndX=-6.5 EndY=1 EndZ=0
    g6: LineSegment StartX=-6.5 StartY=1 StartZ=0 EndX=-5 EndY=1 EndZ=0
    g7: LineSegment [constr] StartX=-5 StartY=1 StartZ=0 EndX=-4 EndY=3 EndZ=0
    g8: LineSegment [constr] StartX=-4 StartY=3 StartZ=0 EndX=-3 EndY=1 EndZ=0
    g9: LineSegment [constr] StartX=-3 StartY=1 StartZ=0 EndX=-2 EndY=3 EndZ=0
    g10: LineSegment [constr] StartX=-2 StartY=3 StartZ=0 EndX=-1 EndY=1 EndZ=0
    g11: LineSegment [constr] StartX=-1 StartY=1 StartZ=0 EndX=0 EndY=3 EndZ=0
    g12: LineSegment [constr] StartX=0 StartY=3 StartZ=0 EndX=1 EndY=1 EndZ=0
    g13: LineSegment [constr] StartX=1 StartY=1 StartZ=0 EndX=2 EndY=3 EndZ=0
    g14: LineSegment [constr] StartX=2 StartY=3 StartZ=0 EndX=3 EndY=1 EndZ=0
    g15: LineSegment [constr] StartX=3 StartY=1 StartZ=0 EndX=4 EndY=3 EndZ=0
    g16: LineSegment [constr] StartX=4 StartY=3 StartZ=0 EndX=5 EndY=1 EndZ=0
    g17: LineSegment StartX=5 StartY=1 StartZ=0 EndX=6.5 EndY=1 EndZ=0
    g18: LineSegment StartX=6.5 StartY=1 StartZ=0 EndX=6.5 EndY=3 EndZ=0
    g19: LineSegment StartX=6.5 StartY=3 StartZ=0 EndX=7.5 EndY=3 EndZ=0
    g20: LineSegment StartX=5.5 StartY=0 StartZ=0 EndX=-7.5 EndY=0 EndZ=0
    g21: LineSegment [constr] StartX=5 StartY=1 StartZ=0 EndX=-5 EndY=1 EndZ=0
    g22: LineSegment [constr] StartX=-5 StartY=3 StartZ=0 EndX=5 EndY=3 EndZ=0
    g23: GeomPoint [constr] X=-6.5 Y=0 Z=0
    g24: LineSegment [constr] StartX=-5 StartY=2 StartZ=0 EndX=5 EndY=2 EndZ=0
    g25: LineSegment [constr] StartX=-5 StartY=3 StartZ=0 EndX=-6.5 EndY=3 EndZ=0
    g26: LineSegment [constr] StartX=-6.5 StartY=4 StartZ=0 EndX=-7.5 EndY=4 EndZ=0
    g27: LineSegment StartX=5.5 StartY=0 StartZ=0 EndX=5.5 EndY=0.2 EndZ=0
    g28: LineSegment StartX=5.5 StartY=0.2 StartZ=0 EndX=7.5 EndY=0.2 EndZ=0
    g29: LineSegment StartX=7.5 StartY=3 StartZ=0 EndX=7.5 EndY=0.2 EndZ=0
    g30: LineSegment [constr] StartX=5 StartY=1 StartZ=0 EndX=6 EndY=3 EndZ=0
    g31: LineSegment StartX=-4.875 StartY=1 StartZ=0 EndX=-4 EndY=2.75 EndZ=0
    g32: LineSegment StartX=-4 StartY=2.75 StartZ=0 EndX=-3.125 EndY=1 EndZ=0
    g33: LineSegment StartX=-3.125 StartY=1 StartZ=0 EndX=-2.875 EndY=1 EndZ=0
    g34: LineSegment StartX=-2.875 StartY=1 StartZ=0 EndX=-2 EndY=2.75 EndZ=0
    g35: LineSegment StartX=-2 StartY=2.75 StartZ=0 EndX=-1.125 EndY=1 EndZ=0
    g36: LineSegment StartX=-1.125 StartY=1 StartZ=0 EndX=-0.875 EndY=1 EndZ=0
    g37: LineSegment StartX=-0.875 StartY=1 StartZ=0 EndX=0 EndY=2.75 EndZ=0
    g38: LineSegment StartX=0 StartY=2.75 StartZ=0 EndX=0.875 EndY=1 EndZ=0
    g39: LineSegment StartX=0.875 StartY=1 StartZ=0 EndX=1.125 EndY=1 EndZ=0
    g40: LineSegment StartX=1.125 StartY=1 StartZ=0 EndX=2 EndY=2.75 EndZ=0
    g41: LineSegment StartX=2 StartY=2.75 StartZ=0 EndX=2.875 EndY=1 EndZ=0
    g42: LineSegment StartX=2.875 StartY=1 StartZ=0 EndX=3.125 EndY=1 EndZ=0
    g43: LineSegment StartX=3.125 StartY=1 StartZ=0 EndX=4 EndY=2.75 EndZ=0
    g44: LineSegment StartX=4 StartY=2.75 StartZ=0 EndX=4.875 EndY=1 EndZ=0
    g45: LineSegment StartX=4.875 StartY=1 StartZ=0 EndX=5 EndY=1 EndZ=0
    g46: LineSegment StartX=-4.875 StartY=1 StartZ=0 EndX=-5 EndY=1 EndZ=0
    g47: LineSegment [constr] StartX=-5 StartY=2.75 StartZ=0 EndX=5 EndY=2.75 EndZ=0
  constraints (141):
    c: PointOnObject(g0,g-1)
    c: Vertical(g0)
    c: Coincident(g0,g1)
    c: Horizontal(g1)
    c: Coincident(g1,g2)
    c: Tangent(g2,g3) = 1.5708
    c: Horizontal(g4)
    c: Coincident(g4,g5)
    c: Vertical(g5)
    c: Coincident(g5,g6)
    c: Horizontal(g6)
    c: Coincident(g6,g7)
    c: Coincident(g7,g8)
    c: Coincident(g8,g9)
    c: Coincident(g9,g10)
    c: Coincident(g10,g11)
    c: Coincident(g11,g12)
    c: Coincident(g12,g13)
    c: Coincident(g13,g14)
    c: Coincident(g14,g15)
    c: Coincident(g15,g16)
    c: Coincident(g16,g17)
    c: Coincident(g17,g18)
    c: Vertical(g18)
    c: Coincident(g18,g19)
    c: Coincident(g20,g0)
    c: Horizontal(g19)
    c: Coincident(g21,g16)
    c: Coincident(g21,g6)
    c: Horizontal(g21)
    c: PointOnObject(g8,g21)
    c: PointOnObject(g10,g21)
    c: PointOnObject(g12,g21)
    c: PointOnObject(g14,g21)
    c: PointOnObject(g7,g22)
    c: PointOnObject(g9,g22)
    c: PointOnObject(g11,g22)
    c: PointOnObject(g13,g22)
    c: PointOnObject(g15,g22)
    c: Vertical(g22,g16)
    c: Vertical(g22,g6)
    c: Equal(g7,g8)
    c: Equal(g8,g9)
    c: Equal(g9,g10)
    c: Equal(g10,g11)
    c: Equal(g11,g12)
    c: Equal(g12,g13)
    c: Equal(g13,g14)
    c: Equal(g14,g15)
    c: Equal(g15,g16)
    c: Horizontal(g17)
    c: Angle(g2,g1) = 1.13446
    c: Tangent(g3,g4) = 1.5708
    c: DistanceY(g18,g18) = 2
    c: PointOnObject(g11,g-2)
    c: DistanceX(g9,g11) = 2  'espacement_triangle'
    c: PointOnObject(g23,g20)
    c: Horizontal(g18,g22)
    c: Horizontal(g22)
    c: DistanceY(g0,g5) = 1
    c: Horizontal(g24)
    c: Symmetric(g22,g6,g24)
    c: Vertical(g24,g22)
    c: Symmetric(g4,g23,g24)
    c: Coincident(g25,g22)
    c: PointOnObject(g25,g5)
    c: Horizontal(g25)
    c: Horizontal(g20)
    c: DistanceX(g19,g19) = 1  'bord'
    c: PointOnObject(g26,g0)
    c: Horizontal(g26)
    c: Coincident(g4,g26)
    c: Equal(g26,g19)
    c: Radius(g3) = 0.1
    c: DistanceX(g4,g2) = 2
    c: DistanceY(g26,g0) = 1
    c: Vertical(g27)
    c: Coincident(g28,g27)
    c: Horizontal(g28)
    c: DistanceX(g28,g28) = 2
    c: Distance(g27,g27) = 0.2
    c: Coincident(g20,g27)
    c: Coincident(g29,g19)
    c: Coincident(g29,g28)
    c: Vertical(g29)
    c: Coincident(g30,g16)
    c: PointOnObject(g30,g22)
    c: Equal(g30,g16)
    c: Distance(g18,g30) = 0.5  'marge'
    c: Distance(g25,g25) = 1.5
    c: PointOnObject(g31,g21)
    c: Coincident(g31,g32)
    c: PointOnObject(g32,g21)
    c: Coincident(g32,g33)
    c: PointOnObject(g33,g21)
    c: Coincident(g33,g34)
    c: Coincident(g34,g35)
    c: PointOnObject(g35,g21)
    c: Coincident(g35,g36)
    c: PointOnObject(g36,g21)
    c: Coincident(g36,g37)
    c: PointOnObject(g37,g-2)
    c: Coincident(g37,g38)
    c: PointOnObject(g38,g21)
    c: Coincident(g38,g39)
    c: PointOnObject(g39,g21)
    c: Coincident(g39,g40)
    c: Coincident(g40,g41)
    c: PointOnObject(g41,g21)
    c: Coincident(g41,g42)
    c: PointOnObject(g42,g21)
    c: Coincident(g42,g43)
    c: Coincident(g43,g44)
    c: PointOnObject(g44,g21)
    c: Coincident(g44,g45)
    c: Coincident(g45,g16)
    c: Coincident(g31,g46)
    c: Coincident(g46,g6)
    c: Horizontal(g47)
    c: PointOnObject(g43,g47)
    c: PointOnObject(g40,g47)
    c: PointOnObject(g37,g47)
    c: PointOnObject(g34,g47)
    c: PointOnObject(g31,g47)
    c: Equal(g44,g43)
    c: Equal(g43,g41)
    c: Equal(g41,g40)
    c: Equal(g40,g38)
    c: Equal(g38,g37)
    c: Equal(g37,g35)
    c: Equal(g35,g34)
    c: Equal(g34,g32)
    c: Equal(g32,g31)
    c: Vertical(g31,g7)
    c: Parallel(g7,g31)
    c: Distance(g31,g7) = 0.25
    c: Vertical(g34,g9)
    c: Vertical(g13,g40)
    c: Vertical(g43,g15)
    c: Vertical(g47,g22)
    c: Vertical(g47,g22)
FEATURE [PartDesign::Pad] Pad028
  Direction = (0,-1,2e-16)
  Length = 5
  Length2 = 10
  Midplane = true
  Placement = pos=(0,0,0) rot=(1,0,0;1.5708rad)
  Profile = -> Sketch063
  ReferenceAxis = -> Sketch063 [N_Axis]
  Suppressed = false
  Type = 0
FEATURE [Sketcher::SketchObject] Sketch062
  ArcFitTolerance = 1e-06
  AttachmentSupport = -> [Pad028]
  ExternalGeometry = -> [Pad028]
  FullyConstrained = true
  MakeInternals = false
  MapMode = 5
  Placement = pos=(7.5,0,0) rot=(0.707107,0,0.707107;3.14159rad)
  sketch-geometry (6):
    g0: ArcOfCircle CenterX=2 CenterY=0.75 CenterZ=0 NormalX=0 NormalY=0 NormalZ=1 AngleXU=0 Radius=0.3 StartAngle=1e-16 EndAngle=3.14159
    g1: ArcOfCircle CenterX=2 CenterY=-0.75 CenterZ=0 NormalX=0 NormalY=0 NormalZ=1 AngleXU=0 Radius=0.3 StartAngle=3.14159 EndAngle=6.28319
    g2: LineSegment StartX=2.3 StartY=0.75 StartZ=0 EndX=2.3 EndY=-0.75 EndZ=0
    g3: LineSegment StartX=1.7 StartY=0.75 StartZ=0 EndX=1.7 EndY=-0.75 EndZ=0
    g4: LineSegment [constr] StartX=1 StartY=-1e-16 StartZ=0 EndX=3 EndY=-3e-16 EndZ=0
    g5: LineSegment [constr] StartX=2 StartY=0.75 StartZ=0 EndX=2 EndY=-0.75 EndZ=0
  constraints (13):
    c: Tangent(g0,g2) = 1.5708
    c: Tangent(g0,g3) = -1.5708
    c: Tangent(g1,g2) = 1.5708
    c: Tangent(g1,g3) = -1.5708
    c: Equal(g0,g1)
    c: Symmetric(g1,g0,g-1)
    c: Symmetric(g-3,g-3,g4)
    c: Symmetric(g-4,g-4,g4)
    c: Coincident(g5,g0)
    c: Coincident(g5,g1)
    c: Symmetric(g4,g4,g5)
    c: DistanceX(g0,g0) = 0.6
    c: DistanceY(g5,g5) = 1.5
FEATURE [App::Link] Link009  label="Corps003"
  LinkPlacement = pos=(1,4.76837e-07,4) rot=(0,1,0;3.14159rad)
  LinkedObject = -> Body015
  Placement = pos=(1,4.76837e-07,4) rot=(0,1,0;3.14159rad)
FEATURE [PartDesign::Pocket] Pocket033
  BaseFeature = -> Pad028
  Direction = (-1,0,2e-16)
  Length = 2
  Length2 = 5
  Placement = pos=(0,0,0) rot=(1,0,0;1.5708rad)
  Profile = -> Sketch062
  ReferenceAxis = -> Sketch062 [N_Axis]
  Suppressed = false
  Type = 0
FEATURE [PartDesign::Mirrored] Mirrored003
  BaseFeature = -> Pocket033
  MirrorPlane = -> YZ_Plane027
  Originals = -> [Pocket033]
  Placement = pos=(0,0,0) rot=(1,0,0;1.5708rad)
  Suppressed = false
  TransformMode = 0
FEATURE [PartDesign::Body] Body015  label="clip_fil_nylon_1"
  AllowCompound = false
  Group = -> [Sketch062,Sketch063,Pad028,Pocket033,Mirrored003]
  Origin = -> Origin027
  Tip = -> Mirrored003
FEATURE [PartDesign::SubShapeBinder] Binder
  BindCopyOnChange = 0
  BindMode = 0
  ClaimChildren = false
  Context = -> Part011 [Body016.Binder.]
  Fuse = false
  MakeFace = true
  OffsetFill = false
  OffsetIntersection = false
  OffsetJoinType = 0
  OffsetOpenResult = false
  PartialLoad = false
  Relative = true
  Support = -> [Body015,Link009]
  _Version = 2
FEATURE [Sketcher::SketchObject] Sketch064
  ArcFitTolerance = 1e-06
  AttachmentSupport = -> [YZ_Plane028]
  ExternalGeometry = -> [Binder]
  FullyConstrained = true
  MakeInternals = false
  MapMode = 5
  Placement = pos=(0,0,0) rot=(0.57735,0.57735,0.57735;2.0944rad)
  sketch-geometry (8):
    g0: LineSegment StartX=0 StartY=5.1 StartZ=0 EndX=3.6 EndY=5.1 EndZ=0
    g1: LineSegment StartX=3.6 StartY=5.1 StartZ=0 EndX=3.6 EndY=-1.1 EndZ=0
    g2: LineSegment StartX=3.6 StartY=-1.1 StartZ=0 EndX=1.6 EndY=-1.1 EndZ=0
    g3: LineSegment StartX=1.6 StartY=-1.1 StartZ=0 EndX=1.6 EndY=-0.1 EndZ=0
    g4: LineSegment StartX=1.6 StartY=-0.1 StartZ=0 EndX=2.6 EndY=-0.1 EndZ=0
    g5: LineSegment StartX=2.6 StartY=-0.1 StartZ=0 EndX=2.6 EndY=4.1 EndZ=0
    g6: LineSegment StartX=2.6 StartY=4.1 StartZ=0 EndX=0 EndY=4.1 EndZ=0
    g7: LineSegment StartX=0 StartY=5.1 StartZ=0 EndX=0 EndY=4.1 EndZ=0
  constraints (24):
    c: PointOnObject(g0,g-2)
    c: Horizontal(g0)
    c: Coincident(g0,g1)
    c: Vertical(g1)
    c: Coincident(g1,g2)
    c: Horizontal(g2)
    c: Coincident(g2,g3)
    c: Vertical(g3)
    c: Coincident(g3,g4)
    c: Horizontal(g4)
    c: Coincident(g4,g5)
    c: Vertical(g5)
    c: Coincident(g5,g6)
    c: PointOnObject(g6,g-2)
    c: Horizontal(g6)
    c: Coincident(g0,g7)
    c: Coincident(g7,g6)
    c: DistanceY(g7,g7) = 1
    c: Distance(g4,g-1) = 0.1
    c: Distance(g4,g4) = 1
    c: Equal(g3,g7)
    c: DistanceX(g5,g0) = 1
    c: DistanceX(g-3,g5) = 0.1
    c: Distance(g5,g-3) = 0.1
FEATURE [PartDesign::Pad] Pad029
  Direction = (1,0,0)
  Length = 5
  Length2 = 10
  Midplane = true
  Placement = pos=(0,0,0) rot=(1,1,1;2.0944rad)
  Profile = -> Sketch064
  ReferenceAxis = -> Sketch064 [N_Axis]
  Suppressed = false
  Type = 0
FEATURE [PartDesign::Mirrored] Mirrored004
  BaseFeature = -> Pad029
  MirrorPlane = -> Sketch064 [V_Axis]
  Originals = -> [Pad029]
  Placement = pos=(0,0,0) rot=(1,1,1;2.0944rad)
  Refine = true
  Suppressed = false
  TransformMode = 0
FEATURE [PartDesign::Body] Body016  label="clip_securisation_fil_nylon"
  AllowCompound = false
  Group = -> [Sketch064,Binder,Pad029,Mirrored004]
  Origin = -> Origin028
  Tip = -> Mirrored004
FEATURE [App::Part] Part011  label="clip_fil_nylon"
  Group = -> [Body015,Body016,Link009]
  Origin = -> Origin026
FEATURE [Mesh::Feature] Mesh  label="Fillet002 (Meshed)"
FEATURE [Sketcher::SketchObject] Sketch065
  ArcFitTolerance = 1e-06
  AttachmentSupport = -> [XZ_Plane029]
  FullyConstrained = true
  MakeInternals = false
  MapMode = 5
  Placement = pos=(0,0,0) rot=(1,0,0;1.5708rad)
  expr: Constraints[2] = 5.5
  expr: Constraints[5] = 3.4
  sketch-geometry (6):
    g0: Circle CenterX=0 CenterY=0 CenterZ=0 NormalX=0 NormalY=0 NormalZ=1 AngleXU=0 Radius=17.25
    g1: Circle CenterX=0 CenterY=0 CenterZ=0 NormalX=0 NormalY=0 NormalZ=1 AngleXU=0 Radius=2.75
    g2: Circle CenterX=0 CenterY=7 CenterZ=0 NormalX=0 NormalY=0 NormalZ=1 AngleXU=0 Radius=1.7
    g3: Circle CenterX=-7 CenterY=0 CenterZ=0 NormalX=0 NormalY=0 NormalZ=1 AngleXU=0 Radius=1.7
    g4: Circle CenterX=0 CenterY=-7 CenterZ=0 NormalX=0 NormalY=0 NormalZ=1 AngleXU=0 Radius=1.7
    g5: Circle CenterX=7 CenterY=0 CenterZ=0 NormalX=0 NormalY=0 NormalZ=1 AngleXU=0 Radius=1.7
  constraints (14):
    c: Diameter(g0) = 34.5
    c: Coincident(g0,g-1)
    c: Diameter(g1) = 5.5
    c: Coincident(g1,g0)
    c: PointOnObject(g2,g-2)
    c: Diameter(g2) = 3.4
    c: DistanceY(g-1,g2) = 7
    c: PointOnObject(g3,g-1)
    c: Symmetric(g5,g3,g0)
    c: Symmetric(g2,g4,g0)
    c: DistanceX(g3,g-1) = 7
    c: Equal(g5,g4)
    c: Equal(g4,g3)
    c: Equal(g3,g2)
FEATURE [PartDesign::Pad] Pad030
  Direction = (0,-1,2e-16)
  Length = 5
  Length2 = 10
  Placement = pos=(0,0,0) rot=(1,0,0;1.5708rad)
  Profile = -> Sketch065
  ReferenceAxis = -> Sketch065 [N_Axis]
  Suppressed = false
  Type = 0
FEATURE [Sketcher::SketchObject] Sketch066
  ArcFitTolerance = 1e-06
  AttachmentOffset = pos=(0,0,2) rot=(0,0,1;0rad)
  AttachmentSupport = -> [XZ_Plane029]
  FullyConstrained = true
  MakeInternals = false
  MapMode = 5
  Placement = pos=(0,-2,4e-16) rot=(1,0,0;1.5708rad)
  expr: Constraints[1] = 2.7 * 2
  sketch-geometry (1):
    g0: Circle CenterX=0 CenterY=7 CenterZ=0 NormalX=0 NormalY=0 NormalZ=1 AngleXU=0 Radius=2.7
  constraints (3):
    c: PointOnObject(g0,g-2)
    c: Diameter(g0) = 5.4
    c: DistanceY(g-1,g0) = 7
FEATURE [PartDesign::Pocket] Pocket034
  BaseFeature = -> Pad030
  Direction = (0,1,-2e-16)
  Length = 1
  Length2 = 5
  Placement = pos=(0,0,0) rot=(1,0,0;1.5708rad)
  Profile = -> Sketch066
  ReferenceAxis = -> Sketch066 [N_Axis]
  Reversed = true
  Suppressed = false
  Type = 1
FEATURE [PartDesign::PolarPattern] PolarPattern006
  Angle = 360
  Axis = -> Sketch066 [N_Axis]
  BaseFeature = -> Pocket034
  Mode = 0
  Occurrences = 2
  Offset = 120
  Originals = -> [Pocket034]
  Placement = pos=(0,0,0) rot=(1,0,0;1.5708rad)
  Suppressed = false
  TransformMode = 0
FEATURE [Sketcher::SketchObject] Sketch067
  ArcFitTolerance = 1e-06
  AttachmentSupport = -> [YZ_Plane029]
  ExternalGeometry = -> [PolarPattern006]
  FullyConstrained = true
  MakeInternals = false
  MapMode = 5
  Placement = pos=(0,0,0) rot=(0.57735,0.57735,0.57735;2.0944rad)
  sketch-geometry (4):
    g0: ArcOfCircle CenterX=-2.5 CenterY=17.25 CenterZ=0 NormalX=0 NormalY=0 NormalZ=1 AngleXU=0 Radius=1.5 StartAngle=3.14159 EndAngle=6.28319
    g1: LineSegment [constr] StartX=-5 StartY=17.25 StartZ=0 EndX=1.7844e-12 EndY=17.25 EndZ=0
    g2: LineSegment [constr] StartX=-2.5 StartY=17.25 StartZ=0 EndX=-2.5 EndY=17.25 EndZ=0
    g3: LineSegment StartX=-4 StartY=17.25 StartZ=0 EndX=-1 EndY=17.25 EndZ=0
  constraints (11):
    c: Coincident(g1,g-3)
    c: Coincident(g1,g-4)
    c: PointOnObject(g0,g1)
    c: PointOnObject(g0,g1)
    c: Coincident(g2,g0)
    c: Symmetric(g1,g1,g2)
    c: Vertical(g2)
    c: DistanceY(g2,g2) = 0
    c: Coincident(g3,g0)
    c: Coincident(g3,g0)
    c: Distance(g1,g0) = 1
FEATURE [PartDesign::Groove] Groove004
  Angle = 360
  Angle2 = 60
  Axis = (1e-16,1,-1e-16)
  Base = (0,0,0)
  BaseFeature = -> PolarPattern006
  Placement = pos=(0,0,0) rot=(1,0,0;1.5708rad)
  Profile = -> Sketch067
  ReferenceAxis = -> Y_Axis029
  Reversed = true
  Suppressed = false
  Type = 0
FEATURE [Sketcher::SketchObject] Sketch068
  ArcFitTolerance = 1e-06
  AttachmentSupport = -> [XY_Plane029]
  FullyConstrained = true
  MakeInternals = false
  MapMode = 5
  sketch-geometry (1):
    g0: Circle CenterX=0 CenterY=-3 CenterZ=0 NormalX=0 NormalY=0 NormalZ=1 AngleXU=0 Radius=0.75
  constraints (3):
    c: Diameter(g0) = 1.5
    c: PointOnObject(g0,g-2)
    c: DistanceY(g0,g-1) = 3
FEATURE [PartDesign::Pocket] Pocket035
  BaseFeature = -> Groove004
  Direction = (0,0,-1)
  Length = 5
  Length2 = 5
  Midplane = true
  Placement = pos=(0,0,0) rot=(1,0,0;1.5708rad)
  Profile = -> Sketch068
  ReferenceAxis = -> Sketch068 [N_Axis]
  Suppressed = false
  Type = 1
FEATURE [Sketcher::SketchObject] Sketch035
  ArcFitTolerance = 0
  AttachmentSupport = -> [XY_Plane030]
  FullyConstrained = true
  MakeInternals = false
  MapMode = 5
  sketch-geometry (32):
    g0: Circle CenterX=13 CenterY=0 CenterZ=0 NormalX=0 NormalY=0 NormalZ=1 AngleXU=0 Radius=7
    g1: LineSegment StartX=-24.5 StartY=6 StartZ=0 EndX=-24.5 EndY=-6 EndZ=0
    g2: LineSegment StartX=8.14214 StartY=-20 StartZ=0 EndX=17 EndY=-20 EndZ=0
    g3: LineSegment StartX=32 StartY=-5 StartZ=0 EndX=32 EndY=5 EndZ=0
    g4: ArcOfCircle CenterX=-18.5 CenterY=6 CenterZ=0 NormalX=0 NormalY=0 NormalZ=1 AngleXU=0 Radius=6 StartAngle=1.5708 EndAngle=3.14159
    g5: ArcOfCircle CenterX=-18.5 CenterY=-6 CenterZ=0 NormalX=0 NormalY=0 NormalZ=1 AngleXU=0 Radius=6 StartAngle=3.14159 EndAngle=4.71239
    g6: ArcOfCircle CenterX=17 CenterY=-5 CenterZ=0 NormalX=0 NormalY=0 NormalZ=1 AngleXU=0 Radius=15 StartAngle=4.71239 EndAngle=6.28319
    g7: GeomPoint [constr] X=32 Y=-20 Z=0
    g8: LineSegment [constr] StartX=-21.5 StartY=6 StartZ=0 EndX=-21.5 EndY=-6 EndZ=0
    g9: LineSegment [constr] StartX=-21.5 StartY=-6 StartZ=0 EndX=28.5 EndY=-6 EndZ=0
    g10: LineSegment [constr] StartX=28.5 StartY=-6 StartZ=0 EndX=28.5 EndY=6 EndZ=0
    g11: LineSegment [constr] StartX=28.5 StartY=6 StartZ=0 EndX=-21.5 EndY=6 EndZ=0
    g12: LineSegment [constr] StartX=-21.5 StartY=0 StartZ=0 EndX=28.5 EndY=0 EndZ=0
    g13: Circle CenterX=-21.5 CenterY=6 CenterZ=0 NormalX=0 NormalY=0 NormalZ=1 AngleXU=0 Radius=1.85
    g14: Circle CenterX=-21.5 CenterY=-6 CenterZ=0 NormalX=0 NormalY=0 NormalZ=1 AngleXU=0 Radius=1.85
    g15: Circle CenterX=28.5 CenterY=6 CenterZ=0 NormalX=0 NormalY=0 NormalZ=1 AngleXU=0 Radius=1.85
    g16: Circle CenterX=28.5 CenterY=-6 CenterZ=0 NormalX=0 NormalY=0 NormalZ=1 AngleXU=0 Radius=1.85
    g17: ArcOfCircle CenterX=17 CenterY=5 CenterZ=0 NormalX=0 NormalY=0 NormalZ=1 AngleXU=0 Radius=15 StartAngle=0 EndAngle=1.5708
    g18: LineSegment StartX=8.14214 StartY=20 StartZ=0 EndX=17 EndY=20 EndZ=0
    g19: Circle [constr] CenterX=13 CenterY=0 CenterZ=0 NormalX=0 NormalY=0 NormalZ=1 AngleXU=0 Radius=17.5
    g20: LineSegment StartX=-7.31371 StartY=12 StartZ=0 EndX=-18.5 EndY=12 EndZ=0
    g21: LineSegment StartX=-7.31371 StartY=-12 StartZ=0 EndX=-18.5 EndY=-12 EndZ=0
    g22: LineSegment StartX=1.07107 StartY=17.0711 StartZ=0 EndX=-1.65685 EndY=14.3431 EndZ=0
    g23: LineSegment StartX=-1.65685 StartY=-14.3431 StartZ=0 EndX=1.07107 EndY=-17.0711 EndZ=0
    g24: ArcOfCircle CenterX=8.14214 CenterY=10 CenterZ=0 NormalX=0 NormalY=0 NormalZ=1 AngleXU=0 Radius=10 StartAngle=1.5708 EndAngle=2.35619
    g25: GeomPoint [constr] X=4 Y=20 Z=0
    g26: ArcOfCircle CenterX=8.14214 CenterY=-10 CenterZ=0 NormalX=0 NormalY=0 NormalZ=1 AngleXU=0 Radius=10 StartAngle=3.92699 EndAngle=4.71239
    g27: GeomPoint [constr] X=4 Y=-20 Z=0
    g28: ArcOfCircle CenterX=-7.31371 CenterY=-20 CenterZ=0 NormalX=0 NormalY=0 NormalZ=1 AngleXU=0 Radius=8 StartAngle=0.785398 EndAngle=1.5708
    g29: GeomPoint [constr] X=-4 Y=-12 Z=0
    g30: ArcOfCircle CenterX=-7.31371 CenterY=20 CenterZ=0 NormalX=0 NormalY=0 NormalZ=1 AngleXU=0 Radius=8 StartAngle=4.71239 EndAngle=5.49779
    g31: GeomPoint [constr] X=-4 Y=12 Z=0
  constraints (75):
    c: Diameter(g0) = 14
    c: Tangent(g1,g4) = -1.5708
    c: Tangent(g1,g5) = -1.5708
    c: Tangent(g2,g6) = -1.5708
    c: Tangent(g3,g6) = -1.5708
    c: Vertical(g1)
    c: Vertical(g3)
    c: Horizontal(g2)
    c: Equal(g4,g5)
    c: PointOnObject(g7,g2)
    c: PointOnObject(g7,g3)
    c: Coincident(g8,g9)
    c: Coincident(g9,g10)
    c: Coincident(g10,g11)
    c: Coincident(g11,g8)
    c: Vertical(g10)
    c: DistanceX(g11,g11) = 50
    c: DistanceY(g8,g8) = 12
    c: Symmetric(g8,g8,g12)
    c: Symmetric(g10,g10,g12)
    c: PointOnObject(g0,g12)
    c: Diameter(g13) = 3.7
    c: Equal(g16,g15)
    c: Equal(g15,g14)
    c: Equal(g14,g13)
    c: PointOnObject(g-1,g12)
    c: Tangent(g3,g17) = -1.5708
    c: Coincident(g10,g15)
    c: Coincident(g8,g13)
    c: Horizontal(g11)
    c: DistanceX(g-1,g0) = 13
    c: Coincident(g9,g16)
    c: Coincident(g8,g14)
    c: Tangent(g18,g17) = 1.5708
    c: Diameter(g19) = 35
    c: Coincident(g19,g0)
    c: Tangent(g20,g4) = -1.5708
    c: Tangent(g21,g5) = 1.5708
    c: Horizontal(g18)
    c: Horizontal(g20)
    c: Horizontal(g21)
    c: Vertical(g29,g31)
    c: Symmetric(g25,g27,g12)
    c: DistanceX(g31,g-1) = 4
    c: DistanceY(g2,g17) = 40
    c: Vertical(g8)
    c: DistanceX(g8,g-1) = 21.5
    c: PointOnObject(g4,g11)
    c: Symmetric(g5,g4,g12)
    c: DistanceX(g1,g-1) = 24.5
    c: DistanceY(g-1,g31) = 12
    c: Equal(g17,g6)
    c: Radius(g6) = 15
    c: DistanceX(g27,g2) = 13
    c: PointOnObject(g25,g18)
    c: PointOnObject(g25,g22)
    c: Tangent(g18,g24) = 1.5708
    c: Tangent(g22,g24) = -1.5708
    c: PointOnObject(g27,g23)
    c: PointOnObject(g27,g2)
    c: Tangent(g23,g26) = -1.5708
    c: Tangent(g2,g26) = -1.5708
    c: PointOnObject(g29,g21)
    c: PointOnObject(g29,g23)
    c: Tangent(g21,g28) = -1.5708
    c: Tangent(g23,g28) = 1.5708
    c: PointOnObject(g31,g20)
    c: PointOnObject(g31,g22)
    c: Tangent(g20,g30) = 1.5708
    c: Tangent(g22,g30) = 1.5708
    c: Equal(g30,g28)
    c: Equal(g26,g24)
    c: Angle(g22,g20) = 2.35619
    c: Radius(g30) = 8
    c: Radius(g24) = 10
FEATURE [PartDesign::Pad] Pad031
  Direction = (0,0,1)
  Length = 8
  Length2 = 10.3
  Profile = -> Sketch035
  ReferenceAxis = -> Sketch035 [N_Axis]
  Suppressed = false
  Type = 4
FEATURE [Sketcher::SketchObject] Sketch069
  ArcFitTolerance = 1e-06
  AttachmentSupport = -> [XZ_Plane030]
  ExternalGeometry = -> [Pad031]
  FullyConstrained = true
  MakeInternals = false
  MapMode = 5
  Placement = pos=(0,0,0) rot=(1,0,0;1.5708rad)
  sketch-geometry (9):
    g0: LineSegment StartX=-16.5 StartY=-3 StartZ=0 EndX=-16.5 EndY=-20 EndZ=0
    g1: LineSegment StartX=-16.5 StartY=-20 StartZ=0 EndX=23.5 EndY=-20 EndZ=0
    g2: LineSegment StartX=23.5 StartY=-20 StartZ=0 EndX=23.5 EndY=-3 EndZ=0
    g3: LineSegment StartX=20.5 StartY=0 StartZ=0 EndX=-13.5 EndY=0 EndZ=0
    g4: LineSegment [constr] StartX=3.5 StartY=0 StartZ=0 EndX=3.5 EndY=-20 EndZ=0
    g5: ArcOfCircle CenterX=-13.5 CenterY=-3 CenterZ=0 NormalX=0 NormalY=0 NormalZ=1 AngleXU=0 Radius=3 StartAngle=1.5708 EndAngle=3.14159
    g6: GeomPoint [constr] X=-16.5 Y=0 Z=0
    g7: ArcOfCircle CenterX=20.5 CenterY=-3 CenterZ=0 NormalX=0 NormalY=0 NormalZ=1 AngleXU=0 Radius=3 StartAngle=1e-16 EndAngle=1.5708
    g8: GeomPoint [constr] X=23.5 Y=0 Z=0
  constraints (22):
    c: Coincident(g0,g1)
    c: Coincident(g1,g2)
    c: Vertical(g0)
    c: Vertical(g2)
    c: Horizontal(g1)
    c: Horizontal(g3)
    c: PointOnObject(g6,g-1)
    c: DistanceY(g0,g6) = 20
    c: DistanceX(g1,g1) = 40
    c: Symmetric(g8,g6,g4)
    c: Symmetric(g1,g1,g4)
    c: DistanceX(g-1,g4) = 3.5
    c: PointOnObject(g6,g3)
    c: PointOnObject(g6,g0)
    c: Tangent(g3,g5) = -1.5708
    c: Tangent(g0,g5) = -1.5708
    c: PointOnObject(g8,g3)
    c: PointOnObject(g8,g2)
    c: Tangent(g3,g7) = -1.5708
    c: Tangent(g2,g7) = -1.5708
    c: Equal(g7,g5)
    c: Radius(g5) = 3
FEATURE [PartDesign::Pocket] Pocket036
  BaseFeature = -> Pad031
  Direction = (0,1,-2e-16)
  Length = 20.2
  Length2 = 5
  Midplane = true
  Profile = -> Sketch069
  ReferenceAxis = -> Sketch069 [N_Axis]
  Suppressed = false
  Type = 0
FEATURE [Sketcher::SketchObject] Sketch070
  ArcFitTolerance = 1e-06
  AttachmentSupport = -> [Pocket036]
  ExternalGeometry = -> [Pocket036]
  FullyConstrained = true
  MakeInternals = false
  MapMode = 5
  Placement = pos=(-24.5,0,0) rot=(0.57735,-0.57735,-0.57735;2.0944rad)
  sketch-geometry (5):
    g0: LineSegment StartX=-0.85 StartY=0 StartZ=0 EndX=-0.85 EndY=-20 EndZ=0
    g1: LineSegment StartX=-0.85 StartY=-20 StartZ=0 EndX=0.85 EndY=-20 EndZ=0
    g2: LineSegment StartX=0.85 StartY=-20 StartZ=0 EndX=0.85 EndY=0 EndZ=0
    g3: LineSegment StartX=0.85 StartY=0 StartZ=0 EndX=-0.85 EndY=0 EndZ=0
    g4: LineSegment [constr] StartX=-4e-16 StartY=8 StartZ=0 EndX=-4e-16 EndY=0 EndZ=0
  constraints (14):
    c: Coincident(g0,g1)
    c: Coincident(g1,g2)
    c: Coincident(g2,g3)
    c: Coincident(g3,g0)
    c: Vertical(g0)
    c: Vertical(g2)
    c: Horizontal(g1)
    c: Horizontal(g3)
    c: PointOnObject(g0,g-1)
    c: Symmetric(g-3,g-3,g4)
    c: Symmetric(g3,g3,g4)
    c: Vertical(g4)
    c: DistanceY(g2,g2) = 20
    c: DistanceX(g3,g3) = 1.7
FEATURE [PartDesign::Pocket] Pocket037
  BaseFeature = -> Pocket036
  Direction = (1,0,0)
  Length = 5
  Length2 = 5
  Profile = -> Sketch070
  ReferenceAxis = -> Sketch070 [N_Axis]
  Suppressed = false
  Type = 1
FEATURE [Sketcher::SketchObject] Sketch043
  ArcFitTolerance = 1e-06
  AttachmentSupport = -> [Pocket037]
  ExternalGeometry = -> [Pocket037]
  FullyConstrained = true
  MakeInternals = false
  MapMode = 5
  Placement = pos=(0,0,8) rot=(0,0,1;0rad)
  sketch-geometry (1):
    g0: Circle CenterX=13 CenterY=0 CenterZ=0 NormalX=0 NormalY=0 NormalZ=1 AngleXU=0 Radius=17.65
  constraints (2):
    c: Diameter(g0) = 35.3
    c: Coincident(g0,g-3)
FEATURE [PartDesign::Pocket] Pocket038
  BaseFeature = -> Pocket037
  Direction = (0,0,-1)
  Length = 5
  Length2 = 5
  Profile = -> Sketch043
  ReferenceAxis = -> Sketch043 [N_Axis]
  Suppressed = false
  Type = 0
FEATURE [Sketcher::SketchObject] Sketch071
  ArcFitTolerance = 1e-06
  AttachmentSupport = -> [XZ_Plane030]
  ExternalGeometry = -> [Pocket038]
  FullyConstrained = true
  MakeInternals = false
  MapMode = 5
  Placement = pos=(0,0,0) rot=(1,0,0;1.5708rad)
  sketch-geometry (4):
    g0: LineSegment StartX=-24.5 StartY=8 StartZ=0 EndX=-24.5 EndY=2 EndZ=0
    g1: LineSegment StartX=-24.5 StartY=2 StartZ=0 EndX=-10.5 EndY=2 EndZ=0
    g2: LineSegment StartX=-10.5 StartY=2 StartZ=0 EndX=-4.5 EndY=8 EndZ=0
    g3: LineSegment StartX=-4.5 StartY=8 StartZ=0 EndX=-24.5 EndY=8 EndZ=0
  constraints (11):
    c: Coincident(g0,g1)
    c: Coincident(g1,g2)
    c: Coincident(g2,g3)
    c: Coincident(g3,g0)
    c: Vertical(g0)
    c: Horizontal(g1)
    c: Horizontal(g3)
    c: Coincident(g0,g-3)
    c: DistanceX(g3,g3) = 20
    c: DistanceY(g0,g0) = 6
    c: Angle(g2,g1) = 2.35619
FEATURE [PartDesign::Pocket] Pocket039
  BaseFeature = -> Pocket038
  Direction = (0,1,-2e-16)
  Length = 5
  Length2 = 5
  Midplane = true
  Profile = -> Sketch071
  ReferenceAxis = -> Sketch071 [N_Axis]
  Suppressed = false
  Type = 1
FEATURE [Sketcher::SketchObject] Sketch072
  ArcFitTolerance = 1e-06
  AttachmentSupport = -> [YZ_Plane030]
  ExternalGeometry = -> [Pocket039]
  FullyConstrained = true
  MakeInternals = false
  MapMode = 5
  Placement = pos=(0,0,0) rot=(0.57735,0.57735,0.57735;2.0944rad)
  sketch-geometry (4):
    g0: LineSegment StartX=-20 StartY=-10.3 StartZ=0 EndX=-12 EndY=-10.3 EndZ=0
    g1: LineSegment StartX=-12 StartY=-10.3 StartZ=0 EndX=-12 EndY=-4.3 EndZ=0
    g2: LineSegment StartX=-12 StartY=-4.3 StartZ=0 EndX=-20 EndY=3.7 EndZ=0
    g3: LineSegment StartX=-20 StartY=3.7 StartZ=0 EndX=-20 EndY=-10.3 EndZ=0
  constraints (11):
    c: Coincident(g0,g1)
    c: Coincident(g1,g2)
    c: Coincident(g2,g3)
    c: Coincident(g3,g0)
    c: Vertical(g1)
    c: Vertical(g3)
    c: Angle(g2,g1) = 2.35619
    c: DistanceY(g1,g1) = 6
    c: Horizontal(g0)
    c: Coincident(g0,g-3)
    c: DistanceX(g0,g0) = 8
FEATURE [PartDesign::Pocket] Pocket040
  BaseFeature = -> Pocket039
  Direction = (-1,0,0)
  Length = 5
  Length2 = 5
  Midplane = true
  Profile = -> Sketch072
  ReferenceAxis = -> Sketch072 [N_Axis]
  Suppressed = false
  Type = 1
FEATURE [Sketcher::SketchObject] Sketch073
  ArcFitTolerance = 1e-06
  AttachmentSupport = -> [XZ_Plane030]
  FullyConstrained = true
  MakeInternals = false
  MapMode = 5
  Placement = pos=(0,0,0) rot=(1,0,0;1.5708rad)
  sketch-geometry (1):
    g0: Circle CenterX=13 CenterY=6 CenterZ=0 NormalX=0 NormalY=0 NormalZ=1 AngleXU=0 Radius=1
  constraints (3):
    c: Diameter(g0) = 2
    c: DistanceX(g-1,g0) = 13
    c: DistanceY(g-1,g0) = 6
FEATURE [PartDesign::Mirrored] Mirrored005
  BaseFeature = -> Pocket040
  MirrorPlane = -> Sketch072 [V_Axis]
  Originals = -> [Pocket040]
  Suppressed = false
  TransformMode = 0
FEATURE [PartDesign::Pocket] Pocket041
  BaseFeature = -> Mirrored005
  Direction = (0,1,-2e-16)
  Length = 5
  Length2 = 5
  Midplane = true
  Profile = -> Sketch073
  ReferenceAxis = -> Sketch073 [N_Axis]
  Suppressed = false
  Type = 1
FEATURE [PartDesign::Fillet] Fillet006
  Base = -> Pocket041 [Edge141,Edge80]
  BaseFeature = -> Pocket041
  Radius = 2
  SupportTransform = false
  Suppressed = false
  UseAllEdges = false
FEATURE [Sketcher::SketchObject] Sketch074
  ArcFitTolerance = 1e-06
  AttachmentOffset = pos=(0,0,-10.3) rot=(0,0,1;0rad)
  AttachmentSupport = -> [XY_Plane030]
  ExternalGeometry = -> [Fillet006]
  FullyConstrained = true
  MakeInternals = false
  MapMode = 5
  Placement = pos=(0,0,-10.3) rot=(0,0,1;0rad)
  sketch-geometry (4):
    g0: Circle CenterX=-21.5 CenterY=6 CenterZ=0 NormalX=0 NormalY=0 NormalZ=1 AngleXU=0 Radius=2.1
    g1: Circle CenterX=-21.5 CenterY=-6 CenterZ=0 NormalX=0 NormalY=0 NormalZ=1 AngleXU=0 Radius=2.1
    g2: Circle CenterX=28.5 CenterY=-6 CenterZ=0 NormalX=0 NormalY=0 NormalZ=1 AngleXU=0 Radius=2.1
    g3: Circle CenterX=28.5 CenterY=6 CenterZ=0 NormalX=0 NormalY=0 NormalZ=1 AngleXU=0 Radius=2.1
  constraints (8):
    c: Coincident(g0,g-3)
    c: Coincident(g1,g-4)
    c: Coincident(g2,g-6)
    c: Coincident(g3,g-5)
    c: Diameter(g0) = 4.2
    c: Equal(g1,g3)
    c: Equal(g3,g2)
    c: Equal(g2,g0)
FEATURE [PartDesign::Pocket] Pocket042
  BaseFeature = -> Fillet006
  Direction = (0,0,-1)
  Length = 3
  Length2 = 5
  Profile = -> Sketch074
  ReferenceAxis = -> Sketch074 [N_Axis]
  Reversed = true
  Suppressed = false
  Type = 0
FEATURE [PartDesign::Body] Body018  label="devidoire_partie_fixe"
  AllowCompound = false
  Group = -> [Sketch035,Pad031,Sketch069,Pocket036,Sketch070,Pocket037,Sketch043,Pocket038,Sketch071,Pocket039,Sketch072,Pocket040,Sketch073,Mirrored005,Pocket041,Fillet006,Sketch074,Pocket042]
  Origin = -> Origin030
  Placement = pos=(-13,0,-0.5) rot=(0,0,1;0rad)
  Tip = -> Pocket042
FEATURE [App::Link] Link010  label="devidoire003"
  LinkTransform = true
  LinkedObject = -> Body017
FEATURE [App::Link] Link011  label="devidoire_partie_fixe001"
  LinkTransform = true
  LinkedObject = -> Body018
FEATURE [Sketcher::SketchObject] Sketch075
  ArcFitTolerance = 1e-06
  AttachmentSupport = -> [XY_Plane031]
  FullyConstrained = false
  MakeInternals = false
  MapMode = 5
  expr: Constraints[33] = 12.7 * 3 / 2
  sketch-geometry (15):
    g0: LineSegment StartX=-23.1 StartY=9.1 StartZ=0 EndX=-23.1 EndY=0 EndZ=0
    g1: LineSegment StartX=0 StartY=13.1 StartZ=0 EndX=-8.60457 EndY=13.1 EndZ=0
    g2: GeomPoint [constr] X=-23.1 Y=13.1 Z=0
    g3: LineSegment StartX=-20.1 StartY=9.1 StartZ=0 EndX=-20.1 EndY=0 EndZ=0
    g4: LineSegment StartX=0 StartY=10.1 StartZ=0 EndX=-19.1 EndY=10.1 EndZ=0
    g5: ArcOfCircle CenterX=-19.1 CenterY=9.1 CenterZ=0 NormalX=0 NormalY=0 NormalZ=1 AngleXU=0 Radius=1 StartAngle=1.5708 EndAngle=3.14159
    g6: GeomPoint [constr] X=-20.1 Y=10.1 Z=0
    g7: LineSegment StartX=0 StartY=13.1 StartZ=0 EndX=0 EndY=10.1 EndZ=0
    g8: LineSegment StartX=-23.1 StartY=0 StartZ=0 EndX=-20.1 EndY=0 EndZ=0
    g9: Circle CenterX=-12.7 CenterY=19.05 CenterZ=0 NormalX=0 NormalY=0 NormalZ=1 AngleXU=0 Radius=1.85
    g10: ArcOfCircle CenterX=-12.7 CenterY=19.05 CenterZ=0 NormalX=0 NormalY=0 NormalZ=1 AngleXU=0 Radius=3 StartAngle=0.174533 EndAngle=2.67021
    g11: GeomPoint [constr] X=-5.24555 Y=13.1 Z=0
    g12: LineSegment StartX=-8.60457 StartY=13.1 StartZ=0 EndX=-9.74558 EndY=19.5709 EndZ=0
    g13: LineSegment StartX=-15.3728 StartY=20.4124 StartZ=0 EndX=-19.1 EndY=13.1 EndZ=0
    g14: ArcOfCircle CenterX=-19.1 CenterY=9.1 CenterZ=0 NormalX=0 NormalY=0 NormalZ=1 AngleXU=0 Radius=4 StartAngle=1.57079 EndAngle=3.14159
  constraints (37):
    c: Vertical(g0)
    c: Horizontal(g1)
    c: PointOnObject(g2,g0)
    c: PointOnObject(g2,g1)
    c: Tangent(g3,g5) = -1.5708
    c: Tangent(g4,g5) = -1.5708
    c: Vertical(g3)
    c: Horizontal(g4)
    c: PointOnObject(g6,g3)
    c: PointOnObject(g6,g4)
    c: Coincident(g7,g1)
    c: Coincident(g7,g4)
    c: Coincident(g8,g0)
    c: Coincident(g8,g3)
    c: PointOnObject(g0,g-1)
    c: PointOnObject(g3,g-1)
    c: PointOnObject(g1,g-2)
    c: PointOnObject(g4,g-2)
    c: DistanceY(g7,g7) = 3
    c: DistanceY(g-1,g4) = 10.1
    c: DistanceX(g3,g-1) = 20.1
    c: Radius(g5) = 1
    c: Diameter(g9) = 3.7
    c: Equal(g8,g7)
    c: Coincident(g9,g10)
    c: PointOnObject(g11,g1)
    c: Radius(g10) = 3
    c: Coincident(g12,g1)
    c: Coincident(g14,g5)
    c: Coincident(g14,g13)
    c: Tangent(g14,g0) = -1.5708
    c: Tangent(g13,g10) = -1.5708
    c: Tangent(g12,g10) = -1.5708
    c: DistanceY(g-1,g9) = 19.05
    c: DistanceX(g9,g-1) = 12.7
    c: Angle(g1,g12) = 1.74533
    c: Horizontal(g1,g13)
FEATURE [PartDesign::Pad] Pad032
  Direction = (0,0,1)
  Length = 15
  Length2 = 10
  Profile = -> Sketch075
  ReferenceAxis = -> Sketch075 [N_Axis]
  Suppressed = false
  Type = 0
FEATURE [PartDesign::Mirrored] Mirrored006
  MirrorPlane = -> YZ_Plane031
  Suppressed = false
  TransformMode = 0
FEATURE [PartDesign::Mirrored] Mirrored007
  MirrorPlane = -> XZ_Plane031
  Suppressed = false
  TransformMode = 0
FEATURE [Part::FeaturePython] Screw005  label="M3x10-Vis"  # WARN: FeaturePython — macro-defined, semantics opaque (R4)
  Diameter = 4
  Invert = false
  LeftHanded = false
  Length = 3
  LengthCustom = 10
  MatchOuter = false
  OffsetAngle = 0
  Placement = pos=(3.2,19.1,-38.5) rot=(0,0,1;0rad)
  Thread = false
  Type = 75
FEATURE [Sketcher::SketchObject] Sketch076
  ArcFitTolerance = 1e-06
  AttachmentSupport = -> [YZ_Plane031]
  FullyConstrained = true
  MakeInternals = false
  MapMode = 5
  Placement = pos=(0,0,0) rot=(0.57735,0.57735,0.57735;2.0944rad)
  sketch-geometry (11):
    g0: LineSegment StartX=-4 StartY=22 StartZ=0 EndX=-4 EndY=4 EndZ=0
    g1: LineSegment StartX=-3 StartY=3 StartZ=0 EndX=3 EndY=3 EndZ=0
    g2: LineSegment StartX=4 StartY=4 StartZ=0 EndX=4 EndY=22 EndZ=0
    g3: LineSegment StartX=3 StartY=23 StartZ=0 EndX=-3 EndY=23 EndZ=0
    g4: ArcOfCircle CenterX=-3 CenterY=22 CenterZ=0 NormalX=0 NormalY=0 NormalZ=1 AngleXU=0 Radius=1 StartAngle=1.5708 EndAngle=3.14159
    g5: ArcOfCircle CenterX=-3 CenterY=4 CenterZ=0 NormalX=0 NormalY=0 NormalZ=1 AngleXU=0 Radius=1 StartAngle=3.14159 EndAngle=4.71239
    g6: ArcOfCircle CenterX=3 CenterY=4 CenterZ=0 NormalX=0 NormalY=0 NormalZ=1 AngleXU=0 Radius=1 StartAngle=4.71239 EndAngle=6.28319
    g7: ArcOfCircle CenterX=3 CenterY=22 CenterZ=0 NormalX=0 NormalY=0 NormalZ=1 AngleXU=0 Radius=1 StartAngle=-2.1538e-12 EndAngle=1.5708
    g8: GeomPoint [constr] X=-4 Y=23 Z=0
    g9: GeomPoint [constr] X=4 Y=3 Z=0
    g10: GeomPoint X=0 Y=13 Z=0
  constraints (25):
    c: Tangent(g0,g4) = -1.5708
    c: Tangent(g0,g5) = -1.5708
    c: Tangent(g1,g5) = -1.5708
    c: Tangent(g1,g6) = -1.5708
    c: Tangent(g2,g6) = -1.5708
    c: Tangent(g2,g7) = -1.5708
    c: Tangent(g3,g7) = -1.5708
    c: Tangent(g3,g4) = -1.5708
    c: Vertical(g0)
    c: Vertical(g2)
    c: Horizontal(g1)
    c: Horizontal(g3)
    c: Equal(g4,g5)
    c: Equal(g5,g6)
    c: Equal(g6,g7)
    c: PointOnObject(g8,g0)
    c: PointOnObject(g8,g3)
    c: PointOnObject(g9,g1)
    c: PointOnObject(g9,g2)
    c: PointOnObject(g10,g-2)
    c: Symmetric(g8,g9,g10)
    c: DistanceX(g0,g2) = 8
    c: DistanceY(g1,g3) = 20
    c: Radius(g4) = 1
    c: DistanceY(g-1,g1) = 3
FEATURE [Sketcher::SketchObject] Sketch077
  ArcFitTolerance = 1e-06
  AttachmentSupport = -> [YZ_Plane031]
  ExternalGeometry = -> [Pad032]
  FullyConstrained = true
  MakeInternals = false
  MapMode = 5
  Placement = pos=(0,0,0) rot=(0.57735,0.57735,0.57735;2.0944rad)
  sketch-geometry (5):
    g0: ArcOfCircle CenterX=16.1 CenterY=6 CenterZ=0 NormalX=0 NormalY=0 NormalZ=1 AngleXU=0 Radius=3 StartAngle=3.14159 EndAngle=4.71239
    g1: LineSegment StartX=13.1 StartY=15 StartZ=0 EndX=22.1 EndY=15 EndZ=0
    g2: LineSegment StartX=22.1 StartY=15 StartZ=0 EndX=22.1 EndY=3 EndZ=0
    g3: LineSegment StartX=22.1 StartY=3 StartZ=0 EndX=16.1 EndY=3 EndZ=0
    g4: LineSegment StartX=13.1 StartY=15 StartZ=0 EndX=13.1 EndY=6 EndZ=0
  constraints (13):
    c: Coincident(g1,g-3)
    c: Horizontal(g1)
    c: Coincident(g2,g1)
    c: Vertical(g2)
    c: Coincident(g3,g2)
    c: Coincident(g4,g1)
    c: Vertical(g4)
    c: Horizontal(g3)
    c: Tangent(g3,g0) = 1.5708
    c: Tangent(g4,g0) = -1.5708
    c: Distance(g3,g3) = 6
    c: DistanceX(g1,g1) = 9
    c: DistanceY(g-1,g2) = 3
FEATURE [PartDesign::Pocket] Pocket044
  BaseFeature = -> Pad032
  Direction = (-1,0,0)
  Length = 5
  Length2 = 5
  Profile = -> Sketch077
  ReferenceAxis = -> Sketch077 [N_Axis]
  Suppressed = false
  Type = 1
FEATURE [PartDesign::MultiTransform] MultiTransform
  BaseFeature = -> Pocket044
  Refine = true
  Suppressed = false
  TransformMode = 1
  Transformations = -> [Mirrored006,Mirrored007]
FEATURE [PartDesign::Pocket] Pocket043
  BaseFeature = -> MultiTransform
  Direction = (-1,0,0)
  Length = 5
  Length2 = 5
  Profile = -> Sketch076
  ReferenceAxis = -> Sketch076 [N_Axis]
  Reversed = true
  Suppressed = false
  Type = 1
FEATURE [PartDesign::Body] Body019  label="support_servo_bloc_moteur"
  AllowCompound = false
  Group = -> [Sketch075,Pad032,Sketch077,Pocket044,MultiTransform,Mirrored006,Mirrored007,Sketch076,Pocket043]
  Origin = -> Origin031
  Placement = pos=(-9.5,0,-41.5) rot=(0,0,1;0rad)
  Tip = -> Pocket043
FEATURE [App::Part] Part010  label="servo_2"
  Group = -> [Link008,Link010,Link011,Body019,Screw005]
  Origin = -> Origin024
  Placement = pos=(59.2,41,39) rot=(0,0,1;3.14159rad)
FEATURE [Sketcher::SketchObject] Sketch078
  ArcFitTolerance = 1e-06
  AttachmentSupport = -> [XZ_Plane029]
  FullyConstrained = true
  MakeInternals = false
  MapMode = 5
  Placement = pos=(0,0,0) rot=(1,0,0;1.5708rad)
  sketch-geometry (1):
    g0: Circle CenterX=0 CenterY=0 CenterZ=0 NormalX=0 NormalY=0 NormalZ=1 AngleXU=0 Radius=10.15
  constraints (2):
    c: Diameter(g0) = 20.3
    c: Coincident(g0,g-1)
FEATURE [PartDesign::Pocket] Pocket045
  BaseFeature = -> Pocket035
  Direction = (0,1,-2e-16)
  Length = 2.5
  Length2 = 5
  Placement = pos=(0,0,0) rot=(1,0,0;1.5708rad)
  Profile = -> Sketch078
  ReferenceAxis = -> Sketch078 [N_Axis]
  Reversed = true
  Suppressed = false
  Type = 0
FEATURE [Sketcher::SketchObject] Sketch079
  ArcFitTolerance = 1e-06
  AttachmentSupport = -> [XY_Plane032]
  FullyConstrained = true
  MakeInternals = false
  MapMode = 5
  sketch-geometry (2):
    g0: Circle CenterX=0 CenterY=0 CenterZ=0 NormalX=0 NormalY=0 NormalZ=1 AngleXU=0 Radius=1.75
    g1: Circle CenterX=0 CenterY=0 CenterZ=0 NormalX=0 NormalY=0 NormalZ=1 AngleXU=0 Radius=2.5
  constraints (4):
    c: Diameter(g0) = 3.5
    c: Coincident(g0,g-1)
    c: Diameter(g1) = 5
    c: Coincident(g1,g0)
FEATURE [PartDesign::Pad] Pad033
  Direction = (0,0,1)
  Length = 8
  Length2 = 10
  Profile = -> Sketch079
  ReferenceAxis = -> Sketch079 [N_Axis]
  Suppressed = false
  Type = 0
FEATURE [PartDesign::Body] Body020  label="Corps004"
  AllowCompound = false
  Group = -> [Sketch079,Pad033]
  Origin = -> Origin032
  Placement = pos=(0,7,8) rot=(0,0,1;0rad)
  Tip = -> Pad033
FEATURE [Sketcher::SketchObject] Sketch080
  ArcFitTolerance = 1e-06
  AttachmentSupport = -> [XZ_Plane029]
  ExternalGeometry = -> [Pocket045]
  FullyConstrained = true
  MakeInternals = false
  MapMode = 5
  Placement = pos=(0,0,0) rot=(1,0,0;1.5708rad)
  sketch-geometry (4):
    g0: ArcOfCircle CenterX=0 CenterY=4.14669 CenterZ=0 NormalX=0 NormalY=0 NormalZ=1 AngleXU=0 Radius=0.5 StartAngle=3.14159 EndAngle=6.2832
    g1: LineSegment StartX=-0.5 StartY=4.3467 StartZ=0 EndX=-0.5 EndY=4.14669 EndZ=0
    g2: LineSegment StartX=0.5 StartY=4.1467 StartZ=0 EndX=0.5 EndY=4.3467 EndZ=0
    g3: LineSegment StartX=0.5 StartY=4.3467 StartZ=0 EndX=-0.5 EndY=4.3467 EndZ=0
  constraints (11):
    c: PointOnObject(g0,g-2)
    c: Coincident(g2,g3)
    c: Coincident(g3,g1)
    c: Vertical(g1)
    c: Vertical(g2)
    c: PointOnObject(g1,g-3)
    c: Coincident(g0,g2)
    c: Symmetric(g2,g1,g-2)
    c: DistanceX(g3,g3) = 1
    c: DistanceY(g2,g2) = 0.2
    c: Tangent(g0,g1) = -1.5708
FEATURE [PartDesign::Pocket] Pocket046
  BaseFeature = -> Pocket045
  Direction = (0,1,-2e-16)
  Length = 5
  Length2 = 5
  Placement = pos=(0,0,0) rot=(1,0,0;1.5708rad)
  Profile = -> Sketch080
  ReferenceAxis = -> Sketch080 [N_Axis]
  Reversed = true
  Suppressed = false
  Type = 1
FEATURE [PartDesign::Mirrored] Mirrored008
  BaseFeature = -> Pocket046
  MirrorPlane = -> Sketch080 [H_Axis]
  Originals = -> [Pocket046]
  Placement = pos=(0,0,0) rot=(1,0,0;1.5708rad)
  Suppressed = false
  TransformMode = 0
FEATURE [PartDesign::Body] Body017  label="devidoire002"
  AllowCompound = false
  Group = -> [Sketch065,Pad030,Sketch066,Pocket034,PolarPattern006,Sketch067,Groove004,Sketch068,Pocket035,Sketch078,Pocket045,Sketch080,Pocket046,Mirrored008]
  Origin = -> Origin029
  Placement = pos=(0,0,2.5) rot=(1,0,0;4.71239rad)
  Tip = -> Mirrored008
FEATURE [App::Part] Part009  label="servo_1"
  Group = -> [Part007,Body011,Body017,Body018,Body020]
  Origin = -> Origin023
  Placement = pos=(-11,9e-16,0) rot=(0,0,1;3.14159rad)
FEATURE [App::Part] Part008  label="CanMover_Enrouleur001"
  Group = -> [Body012,Body013,Part009,Part010]
  Origin = -> Origin019
  Placement = pos=(0,-65,46.5) rot=(0,0,1;1.5708rad)
